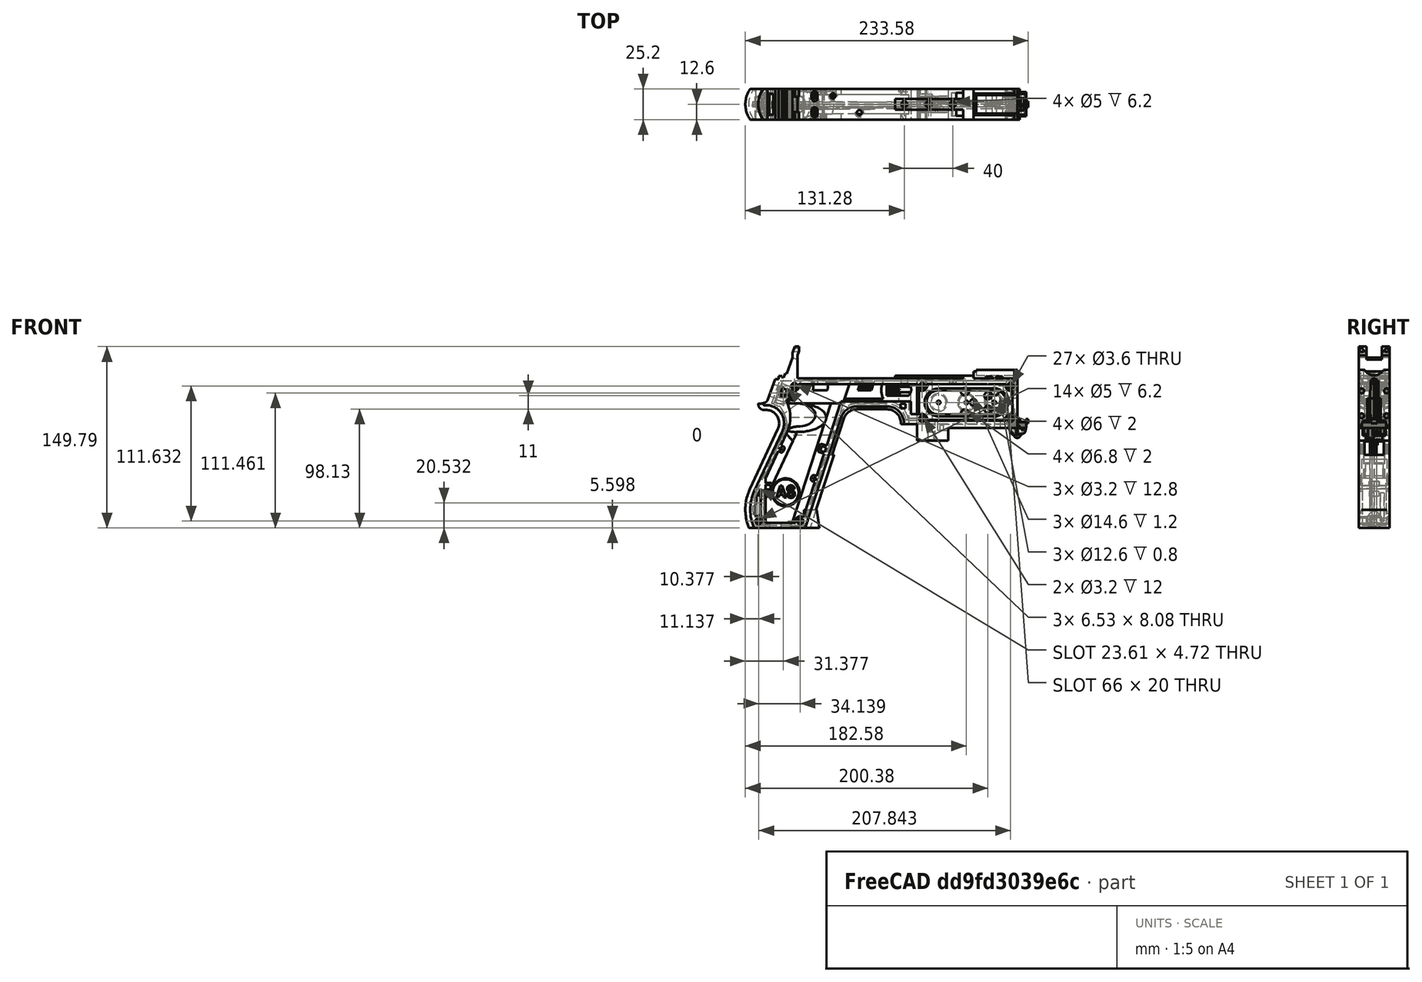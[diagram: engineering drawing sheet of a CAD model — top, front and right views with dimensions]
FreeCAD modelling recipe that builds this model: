
FCSTD DOCUMENT  (FreeCAD 1.0R39319 (Git))
Label: PICON-OF_ver_34
License: All rights reserved
LicenseURL: https://en.wikipedia.org/wiki/All_rights_reserved
objects: Sketcher::SketchObject×119, Part::Extrusion×75, Part::Cut×47, PartDesign::Pad×19, PartDesign::Pocket×14, PartDesign::Chamfer×14, PartDesign::Body×8, Part::MultiFuse×6, PartDesign::Fillet×6, PartDesign::SubtractivePipe×4, Part::Part2DObjectPython×4, PartDesign::SubtractiveLoft×4, PartDesign::Plane×2, PartDesign::SubShapeBinder×2, Part::Sweep×1, PartDesign::ShapeBinder×1, PartDesign::FeatureBase×1, Part::Cone×1, Part::Chamfer×1, Mesh::Feature×1, +1 more types
note: 572 computed .brp shape members not serialized (recipe doc carries the construction recipe); baked Part::Feature solids carry a one-line shape summary decoded from their .brp

FEATURE [Sketcher::SketchObject] Sketch  label="corpo principale"
  ArcFitTolerance = 1e-06
  AttacherType = Attacher::AttachEngine3D
  AttachmentSupport = -> [XZ_Plane]
  FullyConstrained = true
  MakeInternals = false
  MapMode = 5
  Placement = pos=(0,0,0) rot=(1,0,0;1.5708rad)
  sketch-geometry (65):
    g0: LineSegment StartX=0 StartY=0 StartZ=0 EndX=-57.2 EndY=0 EndZ=0
    g1: LineSegment StartX=-57.2 StartY=0 StartZ=0 EndX=-57.2 EndY=-10.4 EndZ=0
    g2: LineSegment StartX=-57.2 StartY=-10.4 StartZ=0 EndX=-82.8 EndY=-10.4 EndZ=0
    g3: LineSegment StartX=-82.8 StartY=-10.4 StartZ=0 EndX=-82.8 EndY=3.2 EndZ=0
    g4: LineSegment StartX=-82.8 StartY=3.2 StartZ=0 EndX=-93.6 EndY=3.2 EndZ=0
    g5: LineSegment StartX=-93.6 StartY=3.2 StartZ=0 EndX=-93.6 EndY=4 EndZ=0
    g6: LineSegment StartX=-107.6 StartY=18 StartZ=0 EndX=-132.428 EndY=18 EndZ=0
    g7: LineSegment StartX=-145.743 StartY=8.32624 StartZ=0 EndX=-175.232 EndY=-82.4316 EndZ=0
    g8: LineSegment StartX=-175.232 StartY=-82.4316 StartZ=0 EndX=-217.232 EndY=-82.4316 EndZ=0
    g9: LineSegment StartX=-217.232 StartY=-52.1862 StartZ=0 EndX=-193.988 EndY=-2.33927 EndZ=0
    g10: LineSegment StartX=-206.196 StartY=23.0857 StartZ=0 EndX=-199.861 EndY=40.4914 EndZ=0
    g11: LineSegment StartX=-199.861 StartY=40.4914 StartZ=0 EndX=-197.061 EndY=40.4914 EndZ=0
    g12: LineSegment StartX=-197.061 StartY=40.4914 StartZ=0 EndX=-197.061 EndY=42.8914 EndZ=0
    g13: LineSegment StartX=-197.061 StartY=42.8914 StartZ=0 EndX=-194.261 EndY=42.8914 EndZ=0
    g14: LineSegment StartX=-194.261 StartY=42.8914 StartZ=0 EndX=-194.535 EndY=42.1397 EndZ=0
    g15: LineSegment StartX=-194.535 StartY=42.1397 StartZ=0 EndX=-193.031 EndY=41.5924 EndZ=0
    g16: LineSegment StartX=-193.031 StartY=41.5924 StartZ=0 EndX=-191.663 EndY=45.3512 EndZ=0
    g17: LineSegment StartX=-191.663 StartY=45.3512 StartZ=0 EndX=-190.536 EndY=44.9408 EndZ=0
    g18: LineSegment StartX=-190.536 StartY=44.9408 StartZ=0 EndX=-185.747 EndY=58.0965 EndZ=0
    g19: LineSegment StartX=-185.747 StartY=58.0965 StartZ=0 EndX=-185.747 EndY=62.0965 EndZ=0
    g20: LineSegment StartX=-185.747 StartY=62.0965 StartZ=0 EndX=-183.832 EndY=67.3588 EndZ=0
    g21: LineSegment StartX=-183.832 StartY=67.3588 StartZ=0 EndX=-180.232 EndY=67.3588 EndZ=0
    g22: LineSegment StartX=-180.232 StartY=67.3588 StartZ=0 EndX=-180.232 EndY=63.7588 EndZ=0
    g23: LineSegment StartX=-180.232 StartY=63.7588 StartZ=0 EndX=-181.6 EndY=60 EndZ=0
    g24: LineSegment StartX=-181.6 StartY=60 StartZ=0 EndX=-181.6 EndY=41.2 EndZ=0
    g25: LineSegment StartX=-181.6 StartY=41.2 StartZ=0 EndX=-100.8 EndY=41.2 EndZ=0
    g26: LineSegment StartX=-36 StartY=43.2 StartZ=0 EndX=-36 EndY=41.2 EndZ=0
    g27: LineSegment StartX=0 StartY=48 StartZ=0 EndX=0 EndY=0 EndZ=0
    g28: LineSegment StartX=-209.901 StartY=19.85 StartZ=0 EndX=-209.901 EndY=20.1 EndZ=0
    g29: LineSegment StartX=-208.001 StartY=22 StartZ=0 EndX=-207.747 EndY=22 EndZ=0
    g30: LineSegment StartX=-207.583 StartY=19 StartZ=0 EndX=-209.051 EndY=19 EndZ=0
    g31: ArcOfCircle CenterX=-208.001 CenterY=20.1 CenterZ=0 NormalX=0 NormalY=0 NormalZ=1 AngleXU=0 Radius=1.9 StartAngle=1.5708 EndAngle=3.14159
    g32: GeomPoint [constr] X=-209.901 Y=22 Z=0
    g33: ArcOfCircle CenterX=-209.051 CenterY=19.85 CenterZ=0 NormalX=0 NormalY=0 NormalZ=1 AngleXU=0 Radius=0.85 StartAngle=3.14159 EndAngle=4.71239
    g34: GeomPoint [constr] X=-209.901 Y=19 Z=0
    g35: ArcOfCircle CenterX=-207.747 CenterY=23.65 CenterZ=0 NormalX=0 NormalY=0 NormalZ=1 AngleXU=0 Radius=1.65 StartAngle=4.71239 EndAngle=5.93412
    g36: GeomPoint [constr] X=-206.591 Y=22 Z=0
    g37: LineSegment StartX=-4 StartY=6 StartZ=0 EndX=-4 EndY=36.4 EndZ=0
    g38: LineSegment StartX=-4 StartY=36.4 StartZ=0 EndX=-185.2 EndY=36.4 EndZ=0
    g39: LineSegment StartX=-185.2 StartY=36.4 StartZ=0 EndX=-190.441 EndY=22 EndZ=0
    g40: LineSegment StartX=-214.575 StartY=-78.4316 StartZ=0 EndX=-178.142 EndY=-78.4316 EndZ=0
    g41: LineSegment StartX=-178.142 StartY=-78.4316 StartZ=0 EndX=-145.51 EndY=22 EndZ=0
    g42: LineSegment StartX=-145.51 StartY=22 StartZ=0 EndX=-87.91 EndY=22 EndZ=0
    g43: LineSegment StartX=-87.91 StartY=22 StartZ=0 EndX=-87.91 EndY=11.6 EndZ=0
    g44: LineSegment StartX=-87.91 StartY=11.6 StartZ=0 EndX=-80.11 EndY=11.6 EndZ=0
    g45: LineSegment StartX=-80.11 StartY=11.6 StartZ=0 EndX=-80.11 EndY=6 EndZ=0
    g46: LineSegment StartX=-80.11 StartY=6 StartZ=0 EndX=-4 EndY=6 EndZ=0
    g47: LineSegment StartX=-190.363 StartY=-4.02975 StartZ=0 EndX=-213.607 EndY=-53.8767 EndZ=0
    g48: ArcOfCircle CenterX=-132.428 CenterY=4 CenterZ=0 NormalX=0 NormalY=0 NormalZ=1 AngleXU=0 Radius=14 StartAngle=1.5708 EndAngle=2.82743
    g49: GeomPoint [constr] X=-142.6 Y=18 Z=0
    g50: ArcOfCircle CenterX=-107.6 CenterY=4 CenterZ=0 NormalX=0 NormalY=0 NormalZ=1 AngleXU=0 Radius=14 StartAngle=0 EndAngle=1.5708
    g51: GeomPoint [constr] X=-93.6 Y=18 Z=0
    g52: ArcOfCircle CenterX=-184.801 CenterY=-67.3089 CenterZ=0 NormalX=0 NormalY=0 NormalZ=1 AngleXU=0 Radius=35.7833 StartAngle=2.70526 EndAngle=3.57792
    g53: ArcOfCircle CenterX=-207.583 CenterY=4 CenterZ=0 NormalX=0 NormalY=0 NormalZ=1 AngleXU=0 Radius=15 StartAngle=5.84685 EndAngle=7.85398
    g54: LineSegment [constr] StartX=-213.607 StartY=-53.8767 StartZ=0 EndX=-217.232 EndY=-52.1862 EndZ=0
    g55: ArcOfCircle CenterX=-184.801 CenterY=-67.3089 CenterZ=0 NormalX=0 NormalY=0 NormalZ=1 AngleXU=0 Radius=31.7833 StartAngle=2.70526 EndAngle=3.49911
    g56: ArcOfCircle CenterX=-218.095 CenterY=8.90192 CenterZ=0 NormalX=0 NormalY=0 NormalZ=1 AngleXU=0 Radius=30.5989 StartAngle=5.84685 EndAngle=6.72553
    g57: LineSegment StartX=-44.6 StartY=43.2 StartZ=0 EndX=-36 EndY=43.2 EndZ=0
    g58: LineSegment StartX=-100.8 StartY=41.2 StartZ=0 EndX=-44.6 EndY=41.2 EndZ=0
    g59: LineSegment StartX=-44.6 StartY=41.2 StartZ=0 EndX=-44.6 EndY=43.2 EndZ=0
    g60: LineSegment StartX=-2.4 StartY=48 StartZ=0 EndX=0 EndY=48 EndZ=0
    g61: LineSegment StartX=-36 StartY=41.2 StartZ=0 EndX=-2.4 EndY=41.2 EndZ=0
    g62: LineSegment StartX=-2.4 StartY=41.2 StartZ=0 EndX=-2.4 EndY=48 EndZ=0
    g63: LineSegment [constr] StartX=-181.6 StartY=36.4 StartZ=0 EndX=-152.209 EndY=36.4 EndZ=0
    g64: LineSegment [constr] StartX=-181.6 StartY=36.4 StartZ=0 EndX=-130.41 EndY=36.4 EndZ=0
  constraints (183):
    c: Coincident(g-1,g0)
    c: PointOnObject(g0,g-1)
    c: Coincident(g0,g1)
    c: Vertical(g1)
    c: Coincident(g1,g2)
    c: Horizontal(g2)
    c: Coincident(g2,g3)
    c: Vertical(g3)
    c: Coincident(g3,g4)
    c: Coincident(g4,g5)
    c: Vertical(g5)
    c: Horizontal(g6)
    c: Coincident(g7,g8)
    c: Horizontal(g8)
    c: Coincident(g10,g11)
    c: Horizontal(g11)
    c: Coincident(g11,g12)
    c: Vertical(g12)
    c: Coincident(g12,g13)
    c: Horizontal(g13)
    c: Coincident(g13,g14)
    c: Coincident(g14,g15)
    c: Coincident(g15,g16)
    c: Coincident(g16,g17)
    c: Coincident(g17,g18)
    c: Coincident(g18,g19)
    c: Vertical(g19)
    c: Coincident(g19,g20)
    c: Coincident(g20,g21)
    c: Horizontal(g21)
    c: Coincident(g21,g22)
    c: Vertical(g22)
    c: Coincident(g22,g23)
    c: Coincident(g23,g24)
    c: Vertical(g24)
    c: Coincident(g24,g25)
    c: Horizontal(g25)
    c: Coincident(g57,g26)
    c: Vertical(g26)
    c: Coincident(g26,g61)
    c: PointOnObject(g60,g-2)
    c: Coincident(g60,g27)
    c: Coincident(g27,g0)
    c: DistanceY(g27,g27) = 48
    c: DistanceY(g1,g1) = 10.4
    c: DistanceX(g0,g0) = 57.2
    c: DistanceX(g2,g2) = 25.6
    c: Horizontal(g4)
    c: DistanceY(g3,g3) = 13.6
    c: DistanceX(g4,g4) = 10.8
    c: DistanceY(g5,g51) = 14.8
    c: DistanceX(g49,g51) = 49
    c: Distance(g7,g49) = 105.6
    c: DistanceX(g61,g60) = 36
    c: DistanceX(g25,g25) = 80.8
    c: DistanceY(g24,g24) = 18.8
    c: DistanceY(g22,g22) = 3.6
    c: Distance(g23) = 4
    c: Angle(g-1,g23) = 1.22173
    c: DistanceX(g21,g21) = 3.6
    c: Distance(g20) = 5.6
    c: Angle(g-1,g20) = 1.22173
    c: DistanceY(g19,g19) = 4
    c: Distance(g18) = 14
    c: Angle(g-1,g18) = 1.22173
    c: Distance(g17) = 1.2
    c: Distance(g16) = 4
    c: Angle(g16) = 1.22173
    c: Perpendicular(g18,g17)
    c: Distance(g15) = 1.6
    c: Perpendicular(g16,g15)
    c: Distance(g14) = 0.8
    c: DistanceX(g13,g13) = 2.8
    c: Perpendicular(g15,g14)
    c: DistanceY(g12,g12) = 2.4
    c: DistanceX(g11,g11) = 2.8
    c: Distance(g9) = 55
    c: Angle(g9,g-1) = 2.00713
    c: Horizontal(g29)
    c: Vertical(g28)
    c: Horizontal(g30)
    c: PointOnObject(g32,g29)
    c: PointOnObject(g32,g28)
    c: Tangent(g29,g31) = 1.5708
    c: Tangent(g28,g31) = 1.5708
    c: PointOnObject(g34,g28)
    c: PointOnObject(g34,g30)
    c: Tangent(g28,g33) = 1.5708
    c: Tangent(g30,g33) = 1.5708
    c: PointOnObject(g36,g29)
    c: PointOnObject(g36,g10)
    c: Tangent(g29,g35) = -1.5708
    c: Tangent(g10,g35) = -1.5708
    c: Angle(g-1,g10) = 1.22173
    c: Radius(g35) = 1.65
    c: Vertical(g37)
    c: Coincident(g37,g38)
    c: Horizontal(g38)
    c: Coincident(g38,g39)
    c: Horizontal(g40)
    c: Coincident(g40,g41)
    c: Coincident(g41,g42)
    c: Horizontal(g42)
    c: Coincident(g42,g43)
    c: Vertical(g43)
    c: Coincident(g43,g44)
    c: Horizontal(g44)
    c: Coincident(g44,g45)
    c: Vertical(g45)
    c: Coincident(g45,g46)
    c: Coincident(g46,g37)
    c: Horizontal(g46)
    c: DistanceY(g0,g37) = 6
    c: DistanceX(g37,g0) = 4
    c: DistanceY(g37,g25) = 4.8
    c: DistanceX(g38,g38) = 181.2
    c: DistanceX(g42,g42) = 57.6
    c: DistanceY(g49,g41) = 4
    c: DistanceX(g41,g49) = 2.91
    c: DistanceY(g43,g43) = 10.4
    c: DistanceX(g44,g44) = 7.8
    c: DistanceY(g7,g40) = 4
    c: Distance(g47) = 55
    c: Angle(g-1,g39) = 1.22173
    c: PointOnObject(g49,g7)
    c: PointOnObject(g49,g6)
    c: Tangent(g7,g48) = -1.5708
    c: Tangent(g6,g48) = -1.5708
    c: PointOnObject(g51,g5)
    c: PointOnObject(g51,g6)
    c: Tangent(g5,g50) = -1.5708
    c: Tangent(g6,g50) = -1.5708
    c: Radius(g50) = 14
    c: Radius(g48) = 14
    c: DistanceX(g8,g8) = 42
    c: Angle(g7,g-1) = 1.88496
    c: Parallel(g41,g7)
    c: Parallel(g47,g9)
    c: Coincident(g52,g8)
    c: Tangent(g52,g9) = 1.5708
    c: DistanceX(g9,g8) = 0
    c: Tangent(g53,g9) = -1.5708
    c: Tangent(g53,g30) = -1.5708
    c: Diameter(g53) = 30
    c: DistanceY(g53,g0) = -4
    c: Coincident(g54,g47)
    c: Distance(g54) = 4
    c: Coincident(g54,g9)
    c: Coincident(g55,g40)
    c: Tangent(g55,g47) = -1.5708
    c: Coincident(g52,g55)
    c: Coincident(g56,g39)
    c: Tangent(g56,g47) = 1.5708
    c: Horizontal(g57)
    c: DistanceX(g57,g57) = 8.6
    c: Coincident(g58,g25)
    c: Horizontal(g58)
    c: Coincident(g59,g58)
    c: Vertical(g59)
    c: DistanceY(g58,g57) = 2
    c: DistanceX(g58,g58) = 56.2
    c: Coincident(g59,g57)
    c: DistanceY(g41,g36) = 0
    c: DistanceY(g36,g39) = 0
    c: DistanceY(g28,g28) = 0.25
    c: DistanceX(g30,g36) = 2.46
    c: DistanceX(g28,g29) = 1.9
    c: Coincident(g62,g60)
    c: Horizontal(g60)
    c: DistanceX(g62,g27) = 2.4
    c: Coincident(g61,g62)
    c: DistanceY(g26,g26) = 2
    c: Vertical(g62)
    c: DistanceY(g61,g60) = 6.8
    c: Horizontal(g61)
    c: Distance(g63) = 29.391
    c: PointOnObject(g63,g38)
    c: PointOnObject(g63,g38)
    c: Distance(g64) = 51.19
    c: PointOnObject(g64,g38)
    c: PointOnObject(g64,g38)
    c: DistanceX(g24,g63) = 0
    c: DistanceX(g24,g64) = 0
FEATURE [Part::Extrusion] Extrude  label="Extrude corpo principale"
  Base = -> Sketch
  Dir = (0,-1,2e-16)
  DirMode = 2
  FaceMakerClass = Part::FaceMakerBullseye
  FaceMakerMode = 3
  LengthFwd = 25.2
  LengthRev = 12.6
  Solid = true
  Symmetric = true
FEATURE [Sketcher::SketchObject] Sketch002  label="scavo grilletto"
  ArcFitTolerance = 1e-06
  AttachmentSupport = -> [XZ_Plane]
  ExternalGeometry = -> [Sketch]
  FullyConstrained = true
  MakeInternals = false
  MapMode = 5
  Placement = pos=(0,0,0) rot=(1,0,0;1.5708rad)
  sketch-geometry (4):
    g0: LineSegment StartX=-89.51 StartY=22 StartZ=0 EndX=-152.71 EndY=22 EndZ=0
    g1: LineSegment StartX=-152.71 StartY=22 StartZ=0 EndX=-167.006 EndY=-22 EndZ=0
    g2: LineSegment StartX=-167.006 StartY=-22 StartZ=0 EndX=-89.51 EndY=-22 EndZ=0
    g3: LineSegment StartX=-89.51 StartY=-22 StartZ=0 EndX=-89.51 EndY=22 EndZ=0
  constraints (12):
    c: Horizontal(g0)
    c: Coincident(g0,g1)
    c: Coincident(g1,g2)
    c: Horizontal(g2)
    c: Coincident(g2,g3)
    c: Coincident(g3,g0)
    c: Vertical(g3)
    c: Angle(g1,g0) = 1.88496
    c: DistanceY(g3,g3) = 44
    c: DistanceX(g0,g0) = 63.2
    c: DistanceX(g0,g-3) = 1.6
    c: DistanceY(g-3,g0) = 0
FEATURE [Sketcher::SketchObject] Sketch004  label="traiettoria arrotondamento impugnatura anteriore"
  ArcFitTolerance = 1e-06
  AttachmentSupport = -> [XZ_Plane]
  ExternalGeometry = -> [Sketch]
  FullyConstrained = true
  MakeInternals = false
  MapMode = 5
  Placement = pos=(0,0,0) rot=(1,0,0;1.5708rad)
  sketch-geometry (13):
    g0: LineSegment StartX=-175.232 StartY=-82.4316 StartZ=0 EndX=-145.743 EndY=8.32624 EndZ=0
    g1: LineSegment StartX=-93.6 StartY=3.2 StartZ=0 EndX=-93.6 EndY=4 EndZ=0
    g2: LineSegment StartX=-132.428 StartY=18 StartZ=0 EndX=-107.6 EndY=18 EndZ=0
    g3: ArcOfCircle CenterX=-132.428 CenterY=4 CenterZ=0 NormalX=0 NormalY=0 NormalZ=1 AngleXU=0 Radius=14 StartAngle=1.5708 EndAngle=2.82743
    g4: ArcOfCircle CenterX=-107.6 CenterY=4 CenterZ=0 NormalX=0 NormalY=0 NormalZ=1 AngleXU=0 Radius=14 StartAngle=0 EndAngle=1.5708
    g5: LineSegment StartX=-175.232 StartY=-82.4316 StartZ=0 EndX=-217.232 EndY=-82.4316 EndZ=0
    g6: LineSegment StartX=-217.232 StartY=-52.1862 StartZ=0 EndX=-193.988 EndY=-2.33927 EndZ=0
    g7: LineSegment StartX=-209.051 StartY=19 StartZ=0 EndX=-207.583 EndY=19 EndZ=0
    g8: LineSegment StartX=-209.901 StartY=20.1 StartZ=0 EndX=-209.901 EndY=19.85 EndZ=0
    g9: ArcOfCircle CenterX=-184.801 CenterY=-67.3089 CenterZ=0 NormalX=0 NormalY=0 NormalZ=1 AngleXU=0 Radius=35.7833 StartAngle=2.70526 EndAngle=3.57792
    g10: ArcOfCircle CenterX=-207.583 CenterY=4 CenterZ=0 NormalX=0 NormalY=0 NormalZ=1 AngleXU=0 Radius=15 StartAngle=5.84685 EndAngle=7.85398
    g11: ArcOfCircle CenterX=-209.051 CenterY=19.85 CenterZ=0 NormalX=0 NormalY=0 NormalZ=1 AngleXU=0 Radius=0.85 StartAngle=3.14159 EndAngle=4.71239
    g12: ArcOfCircle CenterX=-208.001 CenterY=20.1 CenterZ=0 NormalX=0 NormalY=0 NormalZ=1 AngleXU=0 Radius=1.9 StartAngle=1.5708 EndAngle=3.14159
  constraints (26):
    c: Coincident(g0,g-3)
    c: Coincident(g0,g-6)
    c: Coincident(g1,g-8)
    c: Coincident(g1,g-7)
    c: Coincident(g2,g-5)
    c: Coincident(g2,g-4)
    c: Coincident(g3,g2)
    c: Tangent(g3,g0) = 1.5708
    c: Coincident(g4,g1)
    c: Tangent(g4,g2) = 1.5708
    c: Coincident(g5,g0)
    c: Coincident(g5,g-9)
    c: Coincident(g6,g-12)
    c: Coincident(g6,g-11)
    c: Coincident(g7,g-15)
    c: Coincident(g7,g-14)
    c: Coincident(g8,g-16)
    c: Coincident(g8,g-17)
    c: Tangent(g9,g6) = 1.5708
    c: Coincident(g9,g5)
    c: Coincident(g10,g7)
    c: Tangent(g10,g6) = -1.5708
    c: Tangent(g11,g7) = -1.5708
    c: Coincident(g11,g8)
    c: Tangent(g12,g8) = -1.5708
    c: Coincident(g12,g-17)
FEATURE [PartDesign::Plane] DatumPlane  label="Piano per disegno arrotondamento impugnatura"
  AttachmentSupport = -> [Sketch]
  Length = 68.5841
  MapMode = 7
  Placement = pos=(-145.743,1.8e-15,8.32624) rot=(0.154555,0.154555,0.97582;1.59527rad)
  ResizeMode = 0
  Width = 191.269
FEATURE [Sketcher::SketchObject] Sketch005  label="forma arrotondamento impugnatura anteriore"
  ArcFitTolerance = 1e-06
  AttachmentSupport = -> [DatumPlane]
  FullyConstrained = true
  MakeInternals = false
  MapMode = 5
  Placement = pos=(-145.743,1.8e-15,8.32624) rot=(0.154555,0.154555,0.97582;1.59527rad)
  sketch-geometry (5):
    g0: GeomPoint [constr] X=0 Y=-4 Z=0
    g1: GeomPoint [constr] X=-12.6 Y=7.1e-15 Z=0
    g2: GeomPoint [constr] X=12.6 Y=4.97e-14 Z=0
    g3: LineSegment StartX=-12.6 StartY=7.1e-15 StartZ=0 EndX=12.6 EndY=4.97e-14 EndZ=0
    g4: ArcOfCircle CenterX=-3.88e-14 CenterY=17.845 CenterZ=0 NormalX=0 NormalY=0 NormalZ=1 AngleXU=0 Radius=21.845 StartAngle=4.09759 EndAngle=5.32718
  constraints (11):
    c: DistanceY(g0,g-1) = 4
    c: DistanceX(g-1,g0) = 0
    c: DistanceX(g1,g-1) = 12.6
    c: DistanceX(g-1,g2) = 12.6
    c: DistanceY(g-1,g2) = 0
    c: DistanceY(g-1,g1) = 0
    c: Coincident(g3,g1)
    c: Coincident(g3,g2)
    c: Coincident(g4,g1)
    c: Coincident(g4,g2)
    c: PointOnObject(g0,g4)
FEATURE [Part::Sweep] Sweep  label="Sweep impugnatura"
  Frenet = true
  Sections = -> [Sketch005]
  Solid = true
  Spine = -> Sketch [Edge32,Edge33,Edge34,Edge35,Edge36,Edge37,Edge38,Edge39,Edge40,Edge41,Edge42,Edge43,Edge44]
  Transition = 1
FEATURE [Sketcher::SketchObject] Sketch008  label="buchi e pulizie varie"
  ArcFitTolerance = 1e-06
  AttachmentSupport = -> [XZ_Plane]
  ExternalGeometry = -> [Sketch]
  FullyConstrained = true
  MakeInternals = false
  MapMode = 5
  Placement = pos=(0,0,0) rot=(1,0,0;1.5708rad)
  sketch-geometry (26):
    g0: LineSegment StartX=-96.278 StartY=20.155 StartZ=0 EndX=-92.278 EndY=20.155 EndZ=0
    g1: LineSegment StartX=-92.278 StartY=20.155 StartZ=0 EndX=-92.278 EndY=16.155 EndZ=0
    g2: LineSegment StartX=-92.278 StartY=16.155 StartZ=0 EndX=-96.278 EndY=16.155 EndZ=0
    g3: LineSegment StartX=-96.278 StartY=16.155 StartZ=0 EndX=-96.278 EndY=20.155 EndZ=0
    g4: LineSegment StartX=-222.232 StartY=-82.4316 StartZ=0 EndX=-170.232 EndY=-82.4316 EndZ=0
    g5: LineSegment StartX=-170.232 StartY=-82.4316 StartZ=0 EndX=-170.232 EndY=-86.4316 EndZ=0
    g6: LineSegment StartX=-170.232 StartY=-86.4316 StartZ=0 EndX=-222.232 EndY=-86.4316 EndZ=0
    g7: LineSegment StartX=-222.232 StartY=-86.4316 StartZ=0 EndX=-222.232 EndY=-82.4316 EndZ=0
    g8: LineSegment StartX=-213.901 StartY=20.1 StartZ=0 EndX=-213.901 EndY=26 EndZ=0
    g9: LineSegment StartX=-213.901 StartY=26 StartZ=0 EndX=-206.196 EndY=26 EndZ=0
    g10: LineSegment StartX=-17.4 StartY=42.8 StartZ=0 EndX=-12.4 EndY=42.8 EndZ=0
    g11: LineSegment StartX=-12.4 StartY=42.8 StartZ=0 EndX=-12.4 EndY=41.2 EndZ=0
    g12: LineSegment StartX=-12.4 StartY=41.2 StartZ=0 EndX=-17.4 EndY=41.2 EndZ=0
    g13: LineSegment StartX=-17.4 StartY=41.2 StartZ=0 EndX=-17.4 EndY=42.8 EndZ=0
    g14: LineSegment StartX=-25.9 StartY=42.8 StartZ=0 EndX=-20.9 EndY=42.8 EndZ=0
    g15: LineSegment StartX=-20.9 StartY=42.8 StartZ=0 EndX=-20.9 EndY=41.2 EndZ=0
    g16: LineSegment StartX=-20.9 StartY=41.2 StartZ=0 EndX=-25.9 EndY=41.2 EndZ=0
    g17: LineSegment StartX=-25.9 StartY=41.2 StartZ=0 EndX=-25.9 EndY=42.8 EndZ=0
    g18: GeomPoint [constr] X=-206.196 Y=23.0857 Z=0
    g19: GeomPoint [constr] X=-213.901 Y=20.1 Z=0
    g20: BSplineCurve PolesCount=4 KnotsCount=2 Degree=3 IsPeriodic=0
    g21-g24: Circle [constr] x4 (B-spline internal-alignment scaffolding for g20; pole/knot coordinates omitted)
    g25: LineSegment StartX=-206.196 StartY=26 StartZ=0 EndX=-206.196 EndY=23.0857 EndZ=0
  constraints (73):
    c: Horizontal(g0)
    c: Coincident(g1,g0)
    c: Vertical(g1)
    c: Coincident(g2,g1)
    c: Horizontal(g2)
    c: Coincident(g3,g2)
    c: Coincident(g3,g0)
    c: Vertical(g3)
    c: DistanceX(g0,g-4) = 4.368
    c: DistanceY(g0,g-4) = 1.845
    c: DistanceY(g1,g1) = 4
    c: DistanceX(g2,g2) = 4
    c: Horizontal(g4)
    c: Coincident(g5,g4)
    c: Vertical(g5)
    c: Coincident(g6,g5)
    c: Horizontal(g6)
    c: Coincident(g7,g6)
    c: Coincident(g7,g4)
    c: Vertical(g7)
    c: DistanceY(g7,g7) = 4
    c: DistanceX(g4,g-5) = 5
    c: DistanceX(g-5,g4) = 5
    c: DistanceY(g4,g-5) = 0
    c: Coincident(g9,g8)
    c: Parallel(g9,g-6)
    c: DistanceX(g8,g-8) = 4
    c: Horizontal(g10)
    c: Coincident(g11,g10)
    c: Vertical(g11)
    c: Coincident(g12,g11)
    c: Horizontal(g12)
    c: Coincident(g13,g12)
    c: Coincident(g13,g10)
    c: Vertical(g13)
    c: Horizontal(g14)
    c: Coincident(g15,g14)
    c: Vertical(g15)
    c: Coincident(g16,g15)
    c: Horizontal(g16)
    c: Coincident(g17,g16)
    c: Coincident(g17,g14)
    c: Vertical(g17)
    c: DistanceY(g11,g10) = 1.6
    c: DistanceX(g10,g10) = 5
    c: DistanceY(g15,g14) = 1.6
    c: DistanceX(g14,g14) = 5
    c: DistanceX(g15,g12) = 3.5
    c: DistanceX(g11,g-9) = 10
    c: DistanceY(g-9,g11) = 0
    c: DistanceY(g-9,g15) = 0
    c: Perpendicular(g8,g9)
    c: DistanceY(g-7,g9) = 4
    c: DistanceY(g8,g-8) = 0
    c: InternalAlignment(g18,g20)
    c: InternalAlignment(g19,g20)
    c: InternalAlignment(g21,g20)
    c: Weight(g21) = 1
    c: InternalAlignment(g22,g20)
    c: Equal(g22,g21)
    c: InternalAlignment(g23,g20)
    c: Equal(g23,g21)
    c: InternalAlignment(g24,g20)
    c: Equal(g24,g21)
    c: Coincident(g18,g-12)
    c: Coincident(g19,g8)
    c: Coincident(g25,g9)
    c: Coincident(g25,g20)
    c: Vertical(g25)
    c: DistanceY(g20,g23) = 0
    c: DistanceY(g22,g18) = 2.26
    c: DistanceX(g22,g18) = 0.93
    c: DistanceX(g20,g23) = 2.9
FEATURE [Part::Extrusion] Extrude004  label="Extrude Buchi e pulizie varie"
  Base = -> Sketch008
  Dir = (0,-1,2e-16)
  DirMode = 2
  FaceMakerClass = Part::FaceMakerBullseye
  FaceMakerMode = 3
  LengthFwd = 25.2
  LengthRev = 0
  Solid = true
  Symmetric = true
FEATURE [Sketcher::SketchObject] Sketch009  label="rinforzi"
  ArcFitTolerance = 1e-06
  AttachmentSupport = -> [XZ_Plane]
  ExternalGeometry = -> [Sketch]
  FullyConstrained = true
  MakeInternals = false
  MapMode = 5
  Placement = pos=(0,0,0) rot=(1,0,0;1.5708rad)
  sketch-geometry (9):
    g0: LineSegment StartX=-87.91 StartY=22 StartZ=0 EndX=-87.91 EndY=36.4 EndZ=0
    g1: LineSegment StartX=-87.91 StartY=36.4 StartZ=0 EndX=-97.91 EndY=36.4 EndZ=0
    g2: LineSegment StartX=-97.91 StartY=36.4 StartZ=0 EndX=-97.91 EndY=22 EndZ=0
    g3: LineSegment StartX=-97.91 StartY=22 StartZ=0 EndX=-87.91 EndY=22 EndZ=0
    g4: LineSegment StartX=-149.713 StartY=9.06563 StartZ=0 EndX=-154.586 EndY=-5.93437 EndZ=0
    g5: LineSegment StartX=-154.586 StartY=-5.93437 StartZ=0 EndX=-191.863 EndY=-5.93437 EndZ=0
    g6: LineSegment StartX=-191.863 StartY=-5.93437 StartZ=0 EndX=-191.863 EndY=9.06563 EndZ=0
    g7: LineSegment StartX=-191.863 StartY=9.06563 StartZ=0 EndX=-149.713 EndY=9.06563 EndZ=0
    g8: LineSegment [constr] StartX=-145.51 StartY=22 StartZ=0 EndX=-149.713 EndY=9.06563 EndZ=0
  constraints (25):
    c: Vertical(g0)
    c: Coincident(g1,g0)
    c: Horizontal(g1)
    c: Coincident(g2,g1)
    c: Vertical(g2)
    c: Coincident(g3,g2)
    c: Coincident(g3,g0)
    c: Horizontal(g3)
    c: Coincident(g0,g-4)
    c: DistanceX(g3,g3) = 10
    c: DistanceY(g0,g-3) = 0
    c: Coincident(g5,g4)
    c: Horizontal(g5)
    c: Coincident(g6,g5)
    c: Vertical(g6)
    c: Coincident(g7,g6)
    c: Coincident(g7,g4)
    c: Horizontal(g7)
    c: Distance(g8) = 13.6
    c: Parallel(g-6,g8)
    c: Coincident(g-6,g8)
    c: Parallel(g4,g-6)
    c: DistanceY(g4,g4) = 15
    c: Coincident(g4,g8)
    c: DistanceX(g-5,g5) = -1.5
FEATURE [Part::Extrusion] Extrude001  label="Extrude scavo grilletto"
  Base = -> Sketch002
  Dir = (0,-1,2e-16)
  DirMode = 2
  FaceMakerClass = Part::FaceMakerBullseye
  FaceMakerMode = 3
  LengthFwd = 16
  LengthRev = 0
  Solid = true
  Symmetric = true
FEATURE [Part::Extrusion] Extrude005  label="Extrude Rinforzi"
  Base = -> Sketch009
  Dir = (0,-1,2e-16)
  DirMode = 2
  FaceMakerClass = Part::FaceMakerBullseye
  FaceMakerMode = 3
  LengthFwd = 2
  LengthRev = 0
  Placement = pos=(0,12.6,0) rot=(0,0,1;0rad)
  Solid = true
  Symmetric = false
FEATURE [PartDesign::ShapeBinder] CopyCut
  TraceSupport = false
FEATURE [PartDesign::Plane] DatumPlane001
  AttachmentSupport = -> [CopyCut]
  Length = 60
  MapMode = 5
  Placement = pos=(0,12.6,0) rot=(0,0.707107,0.707107;3.14159rad)
  ResizeMode = 0
  Width = 60
FEATURE [Sketcher::SketchObject] Sketch010  label="buco neopixel"
  ArcFitTolerance = 1e-06
  AttachmentSupport = -> [XZ_Plane]
  ExternalGeometry = -> [Sketch]
  FullyConstrained = true
  MakeInternals = false
  MapMode = 5
  Placement = pos=(0,0,0) rot=(1,0,0;1.5708rad)
  sketch-geometry (5):
    g0: LineSegment [constr] StartX=-199.861 StartY=40.4914 StartZ=0 EndX=-201.368 EndY=36.3521 EndZ=0
    g1: LineSegment StartX=-201.368 StartY=36.3521 StartZ=0 EndX=-204.932 EndY=26.5605 EndZ=0
    g2: LineSegment StartX=-201.368 StartY=36.3521 StartZ=0 EndX=-180.2 EndY=28.6477 EndZ=0
    g3: LineSegment StartX=-180.2 StartY=28.6477 StartZ=0 EndX=-183.764 EndY=18.8561 EndZ=0
    g4: LineSegment StartX=-183.764 StartY=18.8561 StartZ=0 EndX=-204.932 EndY=26.5605 EndZ=0
  constraints (14):
    c: Parallel(g0,g-3)
    c: Distance(g0) = 4.405
    c: Coincident(g0,g-3)
    c: Coincident(g2,g1)
    c: Coincident(g3,g2)
    c: Coincident(g4,g3)
    c: Coincident(g4,g1)
    c: Parallel(g1,g-3)
    c: Distance(g1) = 10.42
    c: Coincident(g1,g0)
    c: Parallel(g2,g4)
    c: Perpendicular(g1,g2)
    c: DistanceX(g-4,g2) = 5
    c: Parallel(g3,g1)
FEATURE [Part::Extrusion] Extrude006  label="Extrude buco neopixel"
  Base = -> Sketch010
  Dir = (0,-1,2e-16)
  DirMode = 2
  FaceMakerClass = Part::FaceMakerBullseye
  FaceMakerMode = 3
  LengthFwd = 17.2
  LengthRev = 0
  Solid = true
  Symmetric = true
FEATURE [Sketcher::SketchObject] Sketch011  label="fermo grilletto"
  ArcFitTolerance = 1e-06
  AttachmentSupport = -> [XZ_Plane]
  ExternalGeometry = -> [Sketch]
  FullyConstrained = true
  MakeInternals = false
  MapMode = 5
  Placement = pos=(0,0,0) rot=(1,0,0;1.5708rad)
  sketch-geometry (18):
    g0: LineSegment [constr] StartX=-145.51 StartY=22 StartZ=0 EndX=-157.347 EndY=-14.4293 EndZ=0
    g1: LineSegment [constr] StartX=-157.347 StartY=-14.4293 StartZ=0 EndX=-157.841 EndY=-15.951 EndZ=0
    g2: LineSegment StartX=-161.151 StartY=-13.1932 StartZ=0 EndX=-155.825 EndY=-14.9237 EndZ=0
    g3: LineSegment StartX=-163.167 StartY=-14.2205 StartZ=0 EndX=-164.403 EndY=-18.0247 EndZ=0
    g4: LineSegment StartX=-163.376 StartY=-20.0408 StartZ=0 EndX=-158.05 EndY=-21.7713 EndZ=0
    g5: LineSegment StartX=-158.05 StartY=-21.7713 StartZ=0 EndX=-155.825 EndY=-14.9237 EndZ=0
    g6: LineSegment StartX=-161.645 StartY=-14.7149 StartZ=0 EndX=-157.841 EndY=-15.951 EndZ=0
    g7: LineSegment StartX=-157.841 StartY=-15.951 StartZ=0 EndX=-159.077 EndY=-19.7552 EndZ=0
    g8: LineSegment StartX=-159.077 StartY=-19.7552 StartZ=0 EndX=-162.881 EndY=-18.5191 EndZ=0
    g9: LineSegment StartX=-162.881 StartY=-18.5191 StartZ=0 EndX=-161.645 EndY=-14.7149 EndZ=0
    g10: LineSegment [constr] StartX=-161.645 StartY=-14.7149 StartZ=0 EndX=-161.151 EndY=-13.1932 EndZ=0
    g11: LineSegment [constr] StartX=-159.077 StartY=-19.7552 StartZ=0 EndX=-157.555 EndY=-20.2496 EndZ=0
    g12: LineSegment [constr] StartX=-159.077 StartY=-19.7552 StartZ=0 EndX=-159.572 EndY=-21.2769 EndZ=0
    g13: LineSegment [constr] StartX=-161.645 StartY=-14.7149 StartZ=0 EndX=-163.167 EndY=-14.2205 EndZ=0
    g14: ArcOfCircle CenterX=-161.645 CenterY=-14.7149 CenterZ=0 NormalX=0 NormalY=0 NormalZ=1 AngleXU=0 Radius=1.6 StartAngle=1.25664 EndAngle=2.82743
    g15: GeomPoint [constr] X=-162.673 Y=-12.6988 Z=0
    g16: ArcOfCircle CenterX=-162.881 CenterY=-18.5191 CenterZ=0 NormalX=0 NormalY=0 NormalZ=1 AngleXU=0 Radius=1.6 StartAngle=2.82743 EndAngle=4.39823
    g17: GeomPoint [constr] X=-164.897 Y=-19.5464 Z=0
  constraints (48):
    c: Parallel(g0,g-3)
    c: Distance(g0) = 38.304
    c: Coincident(g0,g-3)
    c: Parallel(g1,g-3)
    c: Distance(g1) = 1.6
    c: Coincident(g1,g0)
    c: Coincident(g5,g4)
    c: Coincident(g5,g2)
    c: Coincident(g7,g6)
    c: Coincident(g8,g7)
    c: Coincident(g9,g8)
    c: Coincident(g9,g6)
    c: Parallel(g7,g-3)
    c: Parallel(g9,g7)
    c: Perpendicular(g6,g7)
    c: Parallel(g6,g8)
    c: Distance(g6) = 4
    c: Distance(g9) = 4
    c: Parallel(g5,g7)
    c: Parallel(g9,g3)
    c: Parallel(g2,g6)
    c: Parallel(g4,g8)
    c: Parallel(g13,g6)
    c: Parallel(g10,g9)
    c: Parallel(g11,g8)
    c: Parallel(g12,g7)
    c: Distance(g10) = 1.6
    c: Distance(g13) = 1.6
    c: Distance(g12) = 1.6
    c: Distance(g11) = 1.6
    c: Coincident(g10,g6)
    c: Coincident(g13,g6)
    c: Coincident(g12,g7)
    c: Coincident(g11,g7)
    c: Distance(g10,g15) = 1.6
    c: Distance(g15,g13) = 1.6
    c: Distance(g4,g12) = 1.6
    c: Distance(g4,g11) = 1.6
    c: PointOnObject(g15,g2)
    c: Tangent(g3,g14) = -1.5708
    c: Tangent(g2,g14) = 1.5708
    c: PointOnObject(g17,g4)
    c: PointOnObject(g17,g3)
    c: Tangent(g4,g16) = -1.5708
    c: Tangent(g3,g16) = -1.5708
    c: Equal(g16,g14)
    c: Coincident(g16,g8)
    c: Coincident(g6,g1)
FEATURE [Part::Extrusion] Extrude007  label="Extrude fermo grilletto"
  Base = -> Sketch011
  Dir = (0,-1,2e-16)
  DirMode = 2
  FaceMakerClass = Part::FaceMakerBullseye
  FaceMakerMode = 3
  LengthFwd = 25.2
  LengthRev = 0
  Solid = true
  Symmetric = true
FEATURE [Sketcher::SketchObject] Sketch012  label="buco oled"
  ArcFitTolerance = 1e-06
  AttachmentSupport = -> [XZ_Plane]
  ExternalGeometry = -> [Sketch]
  FullyConstrained = true
  MakeInternals = false
  MapMode = 5
  Placement = pos=(0,0,0) rot=(1,0,0;1.5708rad)
  sketch-geometry (4):
    g0: LineSegment StartX=-185.747 StartY=58.0965 StartZ=0 EndX=-180.232 EndY=56.0891 EndZ=0
    g1: LineSegment StartX=-185.747 StartY=58.0965 StartZ=0 EndX=-185.747 EndY=67.3588 EndZ=0
    g2: LineSegment StartX=-185.747 StartY=67.3588 StartZ=0 EndX=-180.232 EndY=67.3588 EndZ=0
    g3: LineSegment StartX=-180.232 StartY=67.3588 StartZ=0 EndX=-180.232 EndY=56.0891 EndZ=0
  constraints (10):
    c: Coincident(g1,g0)
    c: Coincident(g2,g1)
    c: Coincident(g3,g2)
    c: Coincident(g3,g0)
    c: Parallel(g1,g-5)
    c: Perpendicular(g-3,g0)
    c: Parallel(g2,g-6)
    c: Parallel(g3,g-4)
    c: Coincident(g0,g-5)
    c: Coincident(g2,g-6)
FEATURE [Part::Extrusion] Extrude008  label="Extrude buco oled"
  Base = -> Sketch012
  Dir = (0,-1,2e-16)
  DirMode = 2
  FaceMakerClass = Part::FaceMakerBullseye
  FaceMakerMode = 3
  LengthFwd = 12.8
  LengthRev = 0
  Solid = true
  Symmetric = true
FEATURE [Sketcher::SketchObject] Sketch013  label="buco pompa"
  ArcFitTolerance = 1e-06
  AttachmentSupport = -> [XZ_Plane]
  ExternalGeometry = -> [Sketch]
  FullyConstrained = true
  MakeInternals = false
  MapMode = 5
  Placement = pos=(0,0,0) rot=(1,0,0;1.5708rad)
  sketch-geometry (8):
    g0: LineSegment StartX=-82.8 StartY=-10.4 StartZ=0 EndX=-82.8 EndY=-9.6 EndZ=0
    g1: LineSegment StartX=-82.8 StartY=-9.6 StartZ=0 EndX=-67.9 EndY=-9.6 EndZ=0
    g2: LineSegment StartX=-67.9 StartY=-9.6 StartZ=0 EndX=-67.9 EndY=6 EndZ=0
    g3: LineSegment StartX=-67.9 StartY=6 StartZ=0 EndX=-65.9 EndY=6 EndZ=0
    g4: LineSegment StartX=-65.9 StartY=6 StartZ=0 EndX=-65.9 EndY=-1.7 EndZ=0
    g5: LineSegment StartX=-65.9 StartY=-1.7 StartZ=0 EndX=-57.2 EndY=-1.7 EndZ=0
    g6: LineSegment StartX=-57.2 StartY=-1.7 StartZ=0 EndX=-57.2 EndY=-10.4 EndZ=0
    g7: LineSegment StartX=-57.2 StartY=-10.4 StartZ=0 EndX=-82.8 EndY=-10.4 EndZ=0
  constraints (22):
    c: Vertical(g0)
    c: Coincident(g1,g0)
    c: Horizontal(g1)
    c: Coincident(g2,g1)
    c: Vertical(g2)
    c: Coincident(g3,g2)
    c: Horizontal(g3)
    c: Coincident(g4,g3)
    c: Vertical(g4)
    c: Coincident(g5,g4)
    c: Horizontal(g5)
    c: Coincident(g6,g5)
    c: Vertical(g6)
    c: Coincident(g7,g6)
    c: Coincident(g7,g0)
    c: DistanceY(g0,g0) = 0.8
    c: DistanceY(g6,g6) = 8.7
    c: DistanceX(g1,g1) = 14.9
    c: DistanceX(g3,g3) = 2
    c: Coincident(g0,g-4)
    c: DistanceY(g2,g-6) = 0
    c: Coincident(g6,g-5)
FEATURE [Part::Extrusion] Extrude009  label="Extrude buco pompa"
  Base = -> Sketch013
  Dir = (0,-1,2e-16)
  DirMode = 2
  FaceMakerClass = Part::FaceMakerBullseye
  FaceMakerMode = 3
  LengthFwd = 13.2
  LengthRev = 0
  Solid = true
  Symmetric = true
FEATURE [Sketcher::SketchObject] Sketch014  label="buco frontale"
  ArcFitTolerance = 1e-06
  AttachmentSupport = -> [XZ_Plane]
  ExternalGeometry = -> [Sketch]
  FullyConstrained = true
  MakeInternals = false
  MapMode = 5
  Placement = pos=(0,0,0) rot=(1,0,0;1.5708rad)
  sketch-geometry (10):
    g0: LineSegment StartX=0 StartY=0 StartZ=0 EndX=0 EndY=24.671 EndZ=0
    g1: LineSegment StartX=0 StartY=24.671 StartZ=0 EndX=-4 EndY=24.671 EndZ=0
    g2: LineSegment StartX=-4 StartY=24.671 StartZ=0 EndX=-4 EndY=16 EndZ=0
    g3: LineSegment StartX=-4 StartY=16 StartZ=0 EndX=-2.4 EndY=16 EndZ=0
    g4: LineSegment StartX=-2.4 StartY=16 StartZ=0 EndX=-2.4 EndY=10 EndZ=0
    g5: LineSegment StartX=-2.4 StartY=10 StartZ=0 EndX=-12 EndY=10 EndZ=0
    g6: LineSegment StartX=-12 StartY=10 StartZ=0 EndX=-12 EndY=6 EndZ=0
    g7: LineSegment StartX=-12 StartY=6 StartZ=0 EndX=-2.4 EndY=6 EndZ=0
    g8: LineSegment StartX=-2.4 StartY=6 StartZ=0 EndX=-2.4 EndY=0 EndZ=0
    g9: LineSegment StartX=-2.4 StartY=0 StartZ=0 EndX=0 EndY=0 EndZ=0
  constraints (29):
    c: Vertical(g0)
    c: Coincident(g1,g0)
    c: Horizontal(g1)
    c: Coincident(g2,g1)
    c: Vertical(g2)
    c: Coincident(g3,g2)
    c: Horizontal(g3)
    c: Coincident(g4,g3)
    c: Vertical(g4)
    c: Coincident(g5,g4)
    c: Horizontal(g5)
    c: Coincident(g6,g5)
    c: Vertical(g6)
    c: Coincident(g7,g6)
    c: Coincident(g8,g7)
    c: Vertical(g8)
    c: Coincident(g9,g8)
    c: Coincident(g9,g0)
    c: Horizontal(g9)
    c: DistanceY(g0,g0) = 24.671
    c: Horizontal(g7)
    c: DistanceY(g6,g6) = 4
    c: DistanceY(g4,g4) = 6
    c: DistanceX(g9,g9) = 2.4
    c: Coincident(g0,g-1)
    c: DistanceY(g-3,g7) = 0
    c: DistanceX(g8,g4) = 0
    c: DistanceX(g-3,g1) = 0
    c: DistanceX(g6,g-3) = 8
FEATURE [Part::Extrusion] Extrude010  label="Extrude buco frontale"
  Base = -> Sketch014
  Dir = (0,-1,2e-16)
  DirMode = 2
  FaceMakerClass = Part::FaceMakerBullseye
  FaceMakerMode = 3
  LengthFwd = 11.2
  LengthRev = 0
  Solid = true
  Symmetric = true
FEATURE [Sketcher::SketchObject] Sketch015  label="guida rail"
  ArcFitTolerance = 1e-06
  AttachmentSupport = -> [XZ_Plane]
  ExternalGeometry = -> [Sketch]
  FullyConstrained = true
  MakeInternals = false
  MapMode = 5
  Placement = pos=(0,0,0) rot=(1,0,0;1.5708rad)
  sketch-geometry (4):
    g0: LineSegment StartX=-100.8 StartY=43.2 StartZ=0 EndX=-44.6 EndY=43.2 EndZ=0
    g1: LineSegment StartX=-44.6 StartY=43.2 StartZ=0 EndX=-44.6 EndY=41.2 EndZ=0
    g2: LineSegment StartX=-44.6 StartY=41.2 StartZ=0 EndX=-100.8 EndY=41.2 EndZ=0
    g3: LineSegment StartX=-100.8 StartY=41.2 StartZ=0 EndX=-100.8 EndY=43.2 EndZ=0
  constraints (9):
    c: Horizontal(g0)
    c: Coincident(g1,g0)
    c: Coincident(g2,g1)
    c: Coincident(g3,g2)
    c: Coincident(g3,g0)
    c: Vertical(g3)
    c: Coincident(g2,g-3)
    c: Coincident(g1,g-3)
    c: Coincident(g0,g-4)
FEATURE [Part::Extrusion] Extrude011  label="Extrude guida rail"
  Base = -> Sketch015
  Dir = (0,-1,2e-16)
  DirMode = 2
  FaceMakerClass = Part::FaceMakerBullseye
  FaceMakerMode = 3
  LengthFwd = 9
  LengthRev = 0
  Solid = true
  Symmetric = true
FEATURE [Sketcher::SketchObject] Sketch016  label="guide per coperture laterali"
  ArcFitTolerance = 1e-06
  AttachmentSupport = -> [XZ_Plane]
  ExternalGeometry = -> [Sketch]
  FullyConstrained = true
  MakeInternals = false
  MapMode = 5
  Placement = pos=(0,0,0) rot=(1,0,0;1.5708rad)
  sketch-geometry (14):
    g0: Circle CenterX=-5.6 CenterY=7.6 CenterZ=0 NormalX=0 NormalY=0 NormalZ=1 AngleXU=0 Radius=1.6
    g1: Circle CenterX=-5.6 CenterY=7.6 CenterZ=0 NormalX=0 NormalY=0 NormalZ=1 AngleXU=0 Radius=4
    g2: Circle CenterX=-5.6 CenterY=34.8 CenterZ=0 NormalX=0 NormalY=0 NormalZ=1 AngleXU=0 Radius=1.6
    g3: Circle CenterX=-5.6 CenterY=34.8 CenterZ=0 NormalX=0 NormalY=0 NormalZ=1 AngleXU=0 Radius=4
    g4: Circle CenterX=-184.08 CenterY=34.8 CenterZ=0 NormalX=0 NormalY=0 NormalZ=1 AngleXU=0 Radius=1.6
    g5: Circle CenterX=-184.08 CenterY=34.8 CenterZ=0 NormalX=0 NormalY=0 NormalZ=1 AngleXU=0 Radius=4
    g6: Circle CenterX=-179.305 CenterY=-76.8316 CenterZ=0 NormalX=0 NormalY=0 NormalZ=1 AngleXU=0 Radius=1.6
    g7: Circle CenterX=-179.305 CenterY=-76.8316 CenterZ=0 NormalX=0 NormalY=0 NormalZ=1 AngleXU=0 Radius=4
    g8: Circle CenterX=-213.443 CenterY=-76.8316 CenterZ=0 NormalX=0 NormalY=0 NormalZ=1 AngleXU=0 Radius=1.6
    g9: Circle CenterX=-213.443 CenterY=-76.8316 CenterZ=0 NormalX=0 NormalY=0 NormalZ=1 AngleXU=0 Radius=4
    g10: Circle CenterX=-78.51 CenterY=7.6 CenterZ=0 NormalX=0 NormalY=0 NormalZ=1 AngleXU=0 Radius=1.6
    g11: Circle CenterX=-78.51 CenterY=7.6 CenterZ=0 NormalX=0 NormalY=0 NormalZ=1 AngleXU=0 Radius=4
    g12: Circle CenterX=-78.51 CenterY=34.8 CenterZ=0 NormalX=0 NormalY=0 NormalZ=1 AngleXU=0 Radius=1.6
    g13: Circle CenterX=-78.51 CenterY=34.8 CenterZ=0 NormalX=0 NormalY=0 NormalZ=1 AngleXU=0 Radius=4
  constraints (35):
    c: Diameter(g0) = 3.2
    c: Diameter(g1) = 8
    c: Coincident(g0,g1)
    c: Diameter(g2) = 3.2
    c: Diameter(g3) = 8
    c: Coincident(g3,g2)
    c: Tangent(g2,g-7)
    c: Diameter(g4) = 3.2
    c: Diameter(g5) = 8
    c: Coincident(g5,g4)
    c: Tangent(g4,g-7)
    c: Tangent(g4,g-8)
    c: Diameter(g6) = 3.2
    c: Diameter(g7) = 8
    c: Coincident(g7,g6)
    c: Tangent(g6,g-9)
    c: Tangent(g6,g-10)
    c: Diameter(g8) = 3.2
    c: Diameter(g9) = 8
    c: Coincident(g9,g8)
    c: Tangent(g8,g-10)
    c: Tangent(g8,g-11)
    c: Diameter(g10) = 3.2
    c: Diameter(g11) = 8
    c: Diameter(g12) = 3.2
    c: Diameter(g13) = 8
    c: Coincident(g12,g13)
    c: Coincident(g10,g11)
    c: Tangent(g12,g-7)
    c: DistanceX(g12,g10) = 0
    c: Tangent(g2,g-6)
    c: Tangent(g0,g-6)
    c: Tangent(g0,g-3)
    c: Tangent(g10,g-3)
    c: Tangent(g10,g-4)
FEATURE [Part::Extrusion] Extrude012  label="extrude guide per coperture laterali"
  Base = -> Sketch016
  Dir = (0,-1,2e-16)
  DirMode = 2
  FaceMakerClass = Part::FaceMakerBullseye
  FaceMakerMode = 3
  LengthFwd = 25.2
  LengthRev = 0
  Solid = true
  Symmetric = true
FEATURE [Sketcher::SketchObject] Sketch017  label="supporto CAM"
  ArcFitTolerance = 1e-06
  AttachmentSupport = -> [XZ_Plane]
  ExternalGeometry = -> [Sketch]
  FullyConstrained = true
  MakeInternals = false
  MapMode = 5
  Placement = pos=(0,0,0) rot=(1,0,0;1.5708rad)
  sketch-geometry (6):
    g0: LineSegment StartX=-2.4 StartY=48 StartZ=0 EndX=-2.4 EndY=41.2 EndZ=0
    g1: LineSegment StartX=-2.4 StartY=48 StartZ=0 EndX=-34 EndY=48 EndZ=0
    g2: LineSegment StartX=-34 StartY=48 StartZ=0 EndX=-34 EndY=46.72 EndZ=0
    g3: LineSegment StartX=-34 StartY=46.72 StartZ=0 EndX=-36 EndY=46.72 EndZ=0
    g4: LineSegment StartX=-36 StartY=46.72 StartZ=0 EndX=-36 EndY=41.2 EndZ=0
    g5: LineSegment StartX=-36 StartY=41.2 StartZ=0 EndX=-2.4 EndY=41.2 EndZ=0
  constraints (15):
    c: Coincident(g1,g0)
    c: Horizontal(g1)
    c: Coincident(g2,g1)
    c: Vertical(g2)
    c: Coincident(g3,g2)
    c: Horizontal(g3)
    c: Coincident(g4,g3)
    c: Coincident(g5,g4)
    c: DistanceX(g1,g0) = 31.6
    c: Coincident(g5,g0)
    c: Vertical(g4)
    c: DistanceY(g2,g1) = 1.28
    c: Coincident(g0,g-3)
    c: Coincident(g0,g-3)
    c: Coincident(g4,g-4)
FEATURE [Part::Extrusion] Extrude013  label="Extrude supporto CAM"
  Base = -> Sketch017
  Dir = (0,-1,2e-16)
  DirMode = 2
  FaceMakerClass = Part::FaceMakerBullseye
  FaceMakerMode = 3
  LengthFwd = 17.8
  LengthRev = 0
  Solid = true
  Symmetric = true
FEATURE [Sketcher::SketchObject] Sketch018  label="Scavo CAM"
  ArcFitTolerance = 1e-06
  AttachmentSupport = -> [YZ_Plane]
  ExternalGeometry = -> [Sketch]
  FullyConstrained = true
  MakeInternals = false
  MapMode = 5
  Placement = pos=(0,0,0) rot=(0.57735,0.57735,0.57735;2.0944rad)
  sketch-geometry (4):
    g0: LineSegment StartX=-7.73 StartY=48 StartZ=0 EndX=7.73 EndY=48 EndZ=0
    g1: LineSegment [constr] StartX=1.07e-14 StartY=48 StartZ=0 EndX=0 EndY=43.5155 EndZ=0
    g2: ArcOfCircle CenterX=9e-15 CenterY=52.42 CenterZ=0 NormalX=0 NormalY=0 NormalZ=1 AngleXU=0 Radius=8.90445 StartAngle=3.66102 EndAngle=5.76376
    g3: Circle [constr] CenterX=9e-15 CenterY=52.42 CenterZ=0 NormalX=0 NormalY=0 NormalZ=1 AngleXU=0 Radius=8.9
  constraints (13):
    c: Horizontal(g0)
    c: DistanceY(g-3,g0) = 0
    c: DistanceX(g0,g0) = 15.46
    c: DistanceX(g0,g-3) = 7.73
    c: DistanceX(g-3) = 0
    c: Coincident(g1,g-3)
    c: PointOnObject(g1,g-2)
    c: Coincident(g2,g0)
    c: Coincident(g2,g0)
    c: PointOnObject(g1,g2)
    c: Diameter(g3) = 17.8
    c: DistanceY(g1,g3) = 4.42
    c: Coincident(g2,g3)
FEATURE [Part::Extrusion] Extrude014  label="Extrude Scavo CAM"
  Base = -> Sketch018
  Dir = (1,0,0)
  DirMode = 2
  FaceMakerClass = Part::FaceMakerBullseye
  FaceMakerMode = 3
  LengthFwd = -34
  LengthRev = 0
  Solid = true
  Symmetric = false
FEATURE [Sketcher::SketchObject] Sketch019  label="scavo rumble"
  ArcFitTolerance = 1e-06
  AttachmentSupport = -> [XZ_Plane]
  ExternalGeometry = -> [Sketch]
  FullyConstrained = true
  MakeInternals = false
  MapMode = 5
  Placement = pos=(0,0,0) rot=(1,0,0;1.5708rad)
  sketch-geometry (6):
    g0: LineSegment StartX=-164.575 StartY=-24.3786 StartZ=0 EndX=-159.439 EndY=-26.0473 EndZ=0
    g1: LineSegment StartX=-159.439 StartY=-26.0473 StartZ=0 EndX=-166.547 EndY=-47.9216 EndZ=0
    g2: LineSegment StartX=-166.547 StartY=-47.9216 StartZ=0 EndX=-171.682 EndY=-46.2529 EndZ=0
    g3: LineSegment StartX=-171.682 StartY=-46.2529 StartZ=0 EndX=-164.575 EndY=-24.3786 EndZ=0
    g4: LineSegment [constr] StartX=-145.51 StartY=22 StartZ=0 EndX=-160.961 EndY=-25.5528 EndZ=0
    g5: LineSegment [constr] StartX=-159.439 StartY=-26.0473 StartZ=0 EndX=-160.961 EndY=-25.5528 EndZ=0
  constraints (17):
    c: Coincident(g1,g0)
    c: Coincident(g2,g1)
    c: Coincident(g3,g2)
    c: Coincident(g3,g0)
    c: Parallel(g3,g-3)
    c: Parallel(g3,g1)
    c: Perpendicular(g3,g0)
    c: Perpendicular(g2,g3)
    c: Distance(g2,g0) = 23
    c: Parallel(g4,g-3)
    c: Distance(g4) = 50
    c: Coincident(g4,g-3)
    c: Parallel(g5,g0)
    c: Distance(g5) = 1.6
    c: Coincident(g5,g0)
    c: Distance(g5,g0) = 3.8
    c: Coincident(g5,g4)
FEATURE [Part::Extrusion] Extrude015  label="scavo rumble001"
  Base = -> Sketch019
  Dir = (0,-1,2e-16)
  DirMode = 2
  FaceMakerClass = Part::FaceMakerBullseye
  FaceMakerMode = 3
  LengthFwd = 21
  LengthRev = 0
  Solid = true
  Symmetric = true
FEATURE [Sketcher::SketchObject] Sketch020  label="fermo rumble"
  ArcFitTolerance = 1e-06
  AttachmentSupport = -> [XZ_Plane]
  ExternalGeometry = -> [Sketch019,Sketch]
  FullyConstrained = true
  MakeInternals = false
  MapMode = 5
  Placement = pos=(0,0,0) rot=(1,0,0;1.5708rad)
  sketch-geometry (16):
    g0: LineSegment [constr] StartX=-166.709 StartY=-43.2425 StartZ=0 EndX=-168.068 EndY=-47.4271 EndZ=0
    g1: LineSegment [constr] StartX=-168.068 StartY=-47.4271 StartZ=0 EndX=-166.547 EndY=-47.9216 EndZ=0
    g2: LineSegment StartX=-168.121 StartY=-40.4703 StartZ=0 EndX=-166.029 EndY=-41.1502 EndZ=0
    g3: LineSegment StartX=-166.029 StartY=-41.1502 StartZ=0 EndX=-166.709 EndY=-43.2425 EndZ=0
    g4: LineSegment StartX=-166.709 StartY=-43.2425 StartZ=0 EndX=-168.801 EndY=-42.5626 EndZ=0
    g5: LineSegment StartX=-168.801 StartY=-42.5626 StartZ=0 EndX=-168.121 EndY=-40.4703 EndZ=0
    g6: LineSegment StartX=-167.627 StartY=-38.9486 StartZ=0 EndX=-164.203 EndY=-40.0611 EndZ=0
    g7: LineSegment StartX=-164.203 StartY=-40.0611 StartZ=0 EndX=-165.81 EndY=-45.0066 EndZ=0
    g8: LineSegment StartX=-165.81 StartY=-45.0066 StartZ=0 EndX=-169.234 EndY=-43.8941 EndZ=0
    g9: LineSegment StartX=-170.261 StartY=-41.878 StartZ=0 EndX=-169.643 EndY=-39.9759 EndZ=0
    g10: LineSegment [constr] StartX=-169.643 StartY=-39.9759 StartZ=0 EndX=-169.148 EndY=-38.4542 EndZ=0
    g11: LineSegment [constr] StartX=-169.148 StartY=-38.4542 StartZ=0 EndX=-167.627 EndY=-38.9486 EndZ=0
    g12: ArcOfCircle CenterX=-168.739 CenterY=-42.3724 CenterZ=0 NormalX=0 NormalY=0 NormalZ=1 AngleXU=0 Radius=1.6 StartAngle=2.82743 EndAngle=4.39823
    g13: GeomPoint [constr] X=-170.755 Y=-43.3997 Z=0
    g14: ArcOfCircle CenterX=-168.121 CenterY=-40.4703 CenterZ=0 NormalX=0 NormalY=0 NormalZ=1 AngleXU=0 Radius=1.6 StartAngle=1.25664 EndAngle=2.82743
    g15: GeomPoint [constr] X=-169.148 Y=-38.4542 Z=0
  constraints (42):
    c: Parallel(g0,g-4)
    c: Distance(g0) = 4.4
    c: Coincident(g1,g0)
    c: Perpendicular(g0,g1)
    c: Distance(g1) = 1.6
    c: Coincident(g1,g-5)
    c: Coincident(g3,g2)
    c: Coincident(g4,g3)
    c: Coincident(g5,g4)
    c: Coincident(g5,g2)
    c: Parallel(g3,g-4)
    c: Parallel(g3,g5)
    c: Perpendicular(g2,g3)
    c: Parallel(g4,g2)
    c: Distance(g2) = 2.2
    c: Distance(g3) = 2.2
    c: Coincident(g7,g6)
    c: Coincident(g8,g7)
    c: Parallel(g7,g-4)
    c: Parallel(g7,g9)
    c: Perpendicular(g6,g7)
    c: Parallel(g6,g8)
    c: Distance(g6,g15) = 5.2
    c: Distance(g7) = 5.2
    c: Coincident(g11,g10)
    c: Parallel(g10,g9)
    c: Parallel(g11,g6)
    c: Distance(g10) = 1.6
    c: Distance(g11) = 1.6
    c: Coincident(g10,g15)
    c: Distance(g11,g2) = 1.6
    c: Distance(g2,g10) = 1.6
    c: PointOnObject(g13,g8)
    c: PointOnObject(g13,g9)
    c: Tangent(g8,g12) = 1.5708
    c: Tangent(g9,g12) = 1.5708
    c: PointOnObject(g15,g9)
    c: Tangent(g6,g14) = 1.5708
    c: Tangent(g9,g14) = 1.5708
    c: Equal(g12,g14)
    c: Coincident(g6,g11)
    c: Coincident(g3,g0)
FEATURE [Part::Extrusion] Extrude016  label="Extrude fermo rumble"
  Base = -> Sketch020
  Dir = (0,-1,2e-16)
  DirMode = 2
  FaceMakerClass = Part::FaceMakerBullseye
  FaceMakerMode = 3
  LengthFwd = 25.2
  LengthRev = 0
  Solid = true
  Symmetric = true
FEATURE [Sketcher::SketchObject] Sketch021  label="perno fermo rumble001"
  ArcFitTolerance = 1e-06
  AttachmentSupport = -> [XZ_Plane001]
  FullyConstrained = true
  MakeInternals = false
  MapMode = 5
  Placement = pos=(0,0,0) rot=(1,0,0;1.5708rad)
  sketch-geometry (16):
    g0: LineSegment StartX=0 StartY=0.45 StartZ=0 EndX=0 EndY=1.55 EndZ=0
    g1: LineSegment StartX=0.45 StartY=2 StartZ=0 EndX=1.55 EndY=2 EndZ=0
    g2: LineSegment StartX=2 StartY=1.55 StartZ=0 EndX=2 EndY=0.45 EndZ=0
    g3: LineSegment StartX=1.55 StartY=0 StartZ=0 EndX=0.45 EndY=0 EndZ=0
    g4: ArcOfCircle [constr] CenterX=0.45 CenterY=1.55 CenterZ=0 NormalX=0 NormalY=0 NormalZ=1 AngleXU=0 Radius=0.45 StartAngle=1.5708 EndAngle=3.14159
    g5: GeomPoint [constr] X=0 Y=2 Z=0
    g6: LineSegment StartX=0.45 StartY=2 StartZ=0 EndX=0 EndY=1.55 EndZ=0
    g7: ArcOfCircle [constr] CenterX=1.55 CenterY=1.55 CenterZ=0 NormalX=0 NormalY=0 NormalZ=1 AngleXU=0 Radius=0.45 StartAngle=0 EndAngle=1.5708
    g8: GeomPoint [constr] X=2 Y=2 Z=0
    g9: LineSegment StartX=2 StartY=1.55 StartZ=0 EndX=1.55 EndY=2 EndZ=0
    g10: ArcOfCircle [constr] CenterX=1.55 CenterY=0.45 CenterZ=0 NormalX=0 NormalY=0 NormalZ=1 AngleXU=0 Radius=0.45 StartAngle=4.71239 EndAngle=6.28319
    g11: GeomPoint [constr] X=2 Y=0 Z=0
    g12: LineSegment StartX=1.55 StartY=0 StartZ=0 EndX=2 EndY=0.45 EndZ=0
    g13: ArcOfCircle [constr] CenterX=0.45 CenterY=0.45 CenterZ=0 NormalX=0 NormalY=0 NormalZ=1 AngleXU=0 Radius=0.45 StartAngle=3.14159 EndAngle=4.71239
    g14: GeomPoint [constr] X=0 Y=0 Z=0
    g15: LineSegment StartX=0 StartY=0.45 StartZ=0 EndX=0.45 EndY=0 EndZ=0
  constraints (35):
    c: Coincident(g14,g-1)
    c: PointOnObject(g5,g-2)
    c: Horizontal(g1)
    c: Vertical(g2)
    c: Horizontal(g3)
    c: DistanceX(g5,g8) = 2
    c: DistanceY(g11,g8) = 2
    c: PointOnObject(g5,g0)
    c: PointOnObject(g5,g1)
    c: Tangent(g0,g4) = 1.5708
    c: Tangent(g1,g4) = 1.5708
    c: Coincident(g6,g0)
    c: Coincident(g6,g1)
    c: PointOnObject(g8,g2)
    c: PointOnObject(g8,g1)
    c: Tangent(g2,g7) = 1.5708
    c: Tangent(g1,g7) = 1.5708
    c: Coincident(g9,g2)
    c: Coincident(g9,g1)
    c: PointOnObject(g11,g2)
    c: PointOnObject(g11,g3)
    c: Tangent(g2,g10) = 1.5708
    c: Tangent(g3,g10) = 1.5708
    c: Coincident(g12,g2)
    c: Coincident(g12,g3)
    c: PointOnObject(g14,g0)
    c: PointOnObject(g14,g3)
    c: Tangent(g0,g13) = 1.5708
    c: Tangent(g3,g13) = 1.5708
    c: Coincident(g15,g0)
    c: Coincident(g15,g3)
    c: Equal(g6,g9)
    c: Equal(g9,g12)
    c: Equal(g12,g15)
    c: DistanceX(g14,g3) = 0.45
FEATURE [Part::Extrusion] Extrude017  label="Extrude perno fermo rumble"
  Base = -> Sketch021
  Dir = (0,-1,2e-16)
  DirMode = 2
  FaceMakerClass = Part::FaceMakerBullseye
  FaceMakerMode = 3
  LengthFwd = 25.2
  LengthRev = 0
  Solid = true
  Symmetric = true
FEATURE [Sketcher::SketchObject] Sketch022  label="fori per M3x5(OD)x6(L)"
  ArcFitTolerance = 1e-06
  AttachmentSupport = -> [XZ_Plane]
  ExternalGeometry = -> [Sketch016]
  FullyConstrained = true
  MakeInternals = false
  MapMode = 5
  Placement = pos=(0,0,0) rot=(1,0,0;1.5708rad)
  sketch-geometry (7):
    g0: Circle CenterX=-5.6 CenterY=34.8 CenterZ=0 NormalX=0 NormalY=0 NormalZ=1 AngleXU=0 Radius=2.5
    g1: Circle CenterX=-5.6 CenterY=7.6 CenterZ=0 NormalX=0 NormalY=0 NormalZ=1 AngleXU=0 Radius=2.5
    g2: Circle CenterX=-78.51 CenterY=34.8 CenterZ=0 NormalX=0 NormalY=0 NormalZ=1 AngleXU=0 Radius=2.5
    g3: Circle CenterX=-78.51 CenterY=7.6 CenterZ=0 NormalX=0 NormalY=0 NormalZ=1 AngleXU=0 Radius=2.5
    g4: Circle CenterX=-184.08 CenterY=34.8 CenterZ=0 NormalX=0 NormalY=0 NormalZ=1 AngleXU=0 Radius=2.5
    g5: Circle CenterX=-179.305 CenterY=-76.8316 CenterZ=0 NormalX=0 NormalY=0 NormalZ=1 AngleXU=0 Radius=2.5
    g6: Circle CenterX=-213.443 CenterY=-76.8316 CenterZ=0 NormalX=0 NormalY=0 NormalZ=1 AngleXU=0 Radius=2.5
  constraints (14):
    c: Diameter(g0) = 5
    c: Diameter(g1) = 5
    c: Diameter(g2) = 5
    c: Diameter(g3) = 5
    c: Diameter(g4) = 5
    c: Diameter(g5) = 5
    c: Diameter(g6) = 5
    c: Coincident(g0,g-8)
    c: Coincident(g1,g-9)
    c: Coincident(g2,g-6)
    c: Coincident(g3,g-7)
    c: Coincident(g4,g-5)
    c: Coincident(g5,g-4)
    c: Coincident(g6,g-3)
FEATURE [Part::Extrusion] Extrude018  label="Extrude fori M3x5x6 - dx"
  Base = -> Sketch022
  Dir = (0,-1,2e-16)
  DirMode = 2
  FaceMakerClass = Part::FaceMakerBullseye
  FaceMakerMode = 3
  LengthFwd = 6.2
  LengthRev = 0
  Placement = pos=(0,-9.5,0) rot=(0,0,1;0rad)
  Solid = true
  Symmetric = true
FEATURE [Part::Extrusion] Extrude019  label="Extrude fori M3x5x6 - sx"
  Base = -> Sketch022
  Dir = (0,-1,2e-16)
  DirMode = 2
  FaceMakerClass = Part::FaceMakerBullseye
  FaceMakerMode = 3
  LengthFwd = 6.2
  LengthRev = 0
  Placement = pos=(0,9.5,0) rot=(0,0,1;0rad)
  Solid = true
  Symmetric = true
FEATURE [Sketcher::SketchObject] Sketch023  label="foro anteriore M3x5x6"
  ArcFitTolerance = 1e-06
  AttachmentSupport = -> [YZ_Plane]
  FullyConstrained = true
  MakeInternals = false
  MapMode = 5
  Placement = pos=(0,0,0) rot=(0.57735,0.57735,0.57735;2.0944rad)
  sketch-geometry (2):
    g0: LineSegment [constr] StartX=0 StartY=0 StartZ=0 EndX=0 EndY=38.6 EndZ=0
    g1: Circle CenterX=0 CenterY=38.6 CenterZ=0 NormalX=0 NormalY=0 NormalZ=1 AngleXU=0 Radius=2.5
  constraints (5):
    c: Coincident(g0,g-1)
    c: PointOnObject(g0,g-2)
    c: DistanceY(g0,g0) = 38.6
    c: Diameter(g1) = 5
    c: Coincident(g1,g0)
FEATURE [Part::Extrusion] Extrude020  label="Extrude foro anteriore M3x5x6"
  Base = -> Sketch023
  Dir = (1,0,0)
  DirMode = 2
  FaceMakerClass = Part::FaceMakerBullseye
  FaceMakerMode = 3
  LengthFwd = -6.2
  LengthRev = 0
  Solid = true
  Symmetric = false
FEATURE [Sketcher::SketchObject] Sketch024  label="fori per viti frontale"
  ArcFitTolerance = 1e-06
  AttachmentSupport = -> [YZ_Plane]
  FullyConstrained = true
  MakeInternals = false
  MapMode = 5
  Placement = pos=(0,0,0) rot=(0.57735,0.57735,0.57735;2.0944rad)
  sketch-geometry (9):
    g0: LineSegment [constr] StartX=-10.3 StartY=30.721 StartZ=0 EndX=10.3 EndY=30.721 EndZ=0
    g1: LineSegment [constr] StartX=10.3 StartY=30.721 StartZ=0 EndX=10.3 EndY=10.121 EndZ=0
    g2: LineSegment [constr] StartX=10.3 StartY=10.121 StartZ=0 EndX=-10.3 EndY=10.121 EndZ=0
    g3: LineSegment [constr] StartX=-10.3 StartY=10.121 StartZ=0 EndX=-10.3 EndY=30.721 EndZ=0
    g4: LineSegment [constr] StartX=0 StartY=0 StartZ=0 EndX=0 EndY=10.121 EndZ=0
    g5: Circle CenterX=-10.3 CenterY=30.721 CenterZ=0 NormalX=0 NormalY=0 NormalZ=1 AngleXU=0 Radius=2
    g6: Circle CenterX=10.3 CenterY=30.721 CenterZ=0 NormalX=0 NormalY=0 NormalZ=1 AngleXU=0 Radius=2
    g7: Circle CenterX=-10.3 CenterY=10.121 CenterZ=0 NormalX=0 NormalY=0 NormalZ=1 AngleXU=0 Radius=2
    g8: Circle CenterX=10.3 CenterY=10.121 CenterZ=0 NormalX=0 NormalY=0 NormalZ=1 AngleXU=0 Radius=2
  constraints (22):
    c: Horizontal(g0)
    c: Coincident(g1,g0)
    c: Vertical(g1)
    c: Coincident(g2,g1)
    c: Horizontal(g2)
    c: Coincident(g3,g2)
    c: Coincident(g3,g0)
    c: Vertical(g3)
    c: DistanceX(g0,g0) = 20.6
    c: DistanceY(g3,g3) = 20.6
    c: Coincident(g4,g-1)
    c: PointOnObject(g4,g-2)
    c: DistanceY(g4,g4) = 10.121
    c: Symmetric(g2,g2,g4)
    c: Diameter(g5) = 4
    c: Diameter(g6) = 4
    c: Diameter(g7) = 4
    c: Diameter(g8) = 4
    c: Coincident(g5,g0)
    c: Coincident(g6,g0)
    c: Coincident(g7,g2)
    c: Coincident(g8,g1)
FEATURE [Part::Extrusion] Extrude021  label="Extrude fori per viti frontale"
  Base = -> Sketch024
  Dir = (1,0,0)
  DirMode = 2
  FaceMakerClass = Part::FaceMakerBullseye
  FaceMakerMode = 3
  LengthFwd = -2.4
  LengthRev = 0
  Solid = true
  Symmetric = false
FEATURE [Sketcher::SketchObject] Sketch025  label="foro per filo CAM"
  ArcFitTolerance = 1e-06
  AttachmentSupport = -> [XZ_Plane]
  ExternalGeometry = -> [Sketch]
  FullyConstrained = true
  MakeInternals = false
  MapMode = 5
  Placement = pos=(0,0,0) rot=(1,0,0;1.5708rad)
  sketch-geometry (4):
    g0: LineSegment StartX=-44.6 StartY=41.2 StartZ=0 EndX=-44.6 EndY=36.4 EndZ=0
    g1: LineSegment StartX=-44.6 StartY=36.4 StartZ=0 EndX=-54.6 EndY=36.4 EndZ=0
    g2: LineSegment StartX=-54.6 StartY=36.4 StartZ=0 EndX=-50.4 EndY=41.2 EndZ=0
    g3: LineSegment StartX=-50.4 StartY=41.2 StartZ=0 EndX=-44.6 EndY=41.2 EndZ=0
  constraints (11):
    c: Vertical(g0)
    c: Coincident(g1,g0)
    c: Horizontal(g1)
    c: Coincident(g2,g1)
    c: Coincident(g3,g2)
    c: Coincident(g3,g0)
    c: Horizontal(g3)
    c: Coincident(g0,g-3)
    c: DistanceY(g0,g-4) = 0
    c: DistanceX(g3,g3) = 5.8
    c: DistanceX(g1,g1) = 10
FEATURE [Part::Extrusion] Extrude022  label="Extrude foro per filo CAM dx"
  Base = -> Sketch025
  Dir = (0,-1,2e-16)
  DirMode = 2
  FaceMakerClass = Part::FaceMakerBullseye
  FaceMakerMode = 3
  LengthFwd = 4.9
  LengthRev = 0
  Placement = pos=(0,6.95,0) rot=(0,0,1;0rad)
  Solid = true
  Symmetric = true
FEATURE [Part::Extrusion] Extrude023  label="Extrude foro per filo CAM sx"
  Base = -> Sketch025
  Dir = (0,-1,2e-16)
  DirMode = 2
  FaceMakerClass = Part::FaceMakerBullseye
  FaceMakerMode = 3
  LengthFwd = 4.9
  LengthRev = 0
  Placement = pos=(0,-6.95,0) rot=(0,0,1;0rad)
  Solid = true
  Symmetric = true
FEATURE [Sketcher::SketchObject] Sketch026  label="foro sotto anteriore M3x5x6"
  ArcFitTolerance = 1e-06
  AttachmentSupport = -> [XY_Plane]
  FullyConstrained = true
  MakeInternals = false
  MapMode = 5
  sketch-geometry (2):
    g0: LineSegment [constr] StartX=0 StartY=0 StartZ=0 EndX=-16.5 EndY=0 EndZ=0
    g1: Circle CenterX=-16.5 CenterY=0 CenterZ=0 NormalX=0 NormalY=0 NormalZ=1 AngleXU=0 Radius=2.5
  constraints (5):
    c: Distance(g0) = 16.5
    c: Coincident(g0,g-1)
    c: PointOnObject(g0,g-1)
    c: Diameter(g1) = 5
    c: Coincident(g0,g1)
FEATURE [Sketcher::SketchObject] Sketch027  label="foro sotto posteriore M3x5x6"
  ArcFitTolerance = 1e-06
  AttachmentSupport = -> [XY_Plane]
  ExternalGeometry = -> [Sketch]
  FullyConstrained = true
  MakeInternals = false
  MapMode = 5
  sketch-geometry (2):
    g0: LineSegment [constr] StartX=-82.8 StartY=2e-16 StartZ=0 EndX=-71.3 EndY=2e-16 EndZ=0
    g1: Circle CenterX=-71.3 CenterY=2e-16 CenterZ=0 NormalX=0 NormalY=0 NormalZ=1 AngleXU=0 Radius=2.5
  constraints (5):
    c: Distance(g0) = 11.5
    c: Coincident(g0,g-3)
    c: PointOnObject(g0,g-3)
    c: Diameter(g1) = 5
    c: Coincident(g1,g0)
FEATURE [Sketcher::SketchObject] Sketch029  label="fori sotto impugnatura"
  ArcFitTolerance = 1e-06
  AttachmentSupport = -> [XY_Plane]
  ExternalGeometry = -> [Sketch]
  FullyConstrained = true
  MakeInternals = false
  MapMode = 5
  sketch-geometry (15):
    g0: LineSegment [constr] StartX=-175.232 StartY=-1.83e-14 StartZ=0 EndX=-191.232 EndY=0 EndZ=0
    g1: Circle CenterX=-191.232 CenterY=0 CenterZ=0 NormalX=0 NormalY=0 NormalZ=1 AngleXU=0 Radius=3.95
    g2: LineSegment [constr] StartX=-175.232 StartY=-1.83e-14 StartZ=0 EndX=-204.275 EndY=0 EndZ=0
    g3: LineSegment StartX=-204.275 StartY=3.525 StartZ=0 EndX=-204.275 EndY=-3.525 EndZ=0
    g4: LineSegment StartX=-205.4 StartY=-4.65 StartZ=0 EndX=-206.65 EndY=-4.65 EndZ=0
    g5: LineSegment StartX=-207.775 StartY=-3.525 StartZ=0 EndX=-207.775 EndY=3.525 EndZ=0
    g6: LineSegment StartX=-206.65 StartY=4.65 StartZ=0 EndX=-205.4 EndY=4.65 EndZ=0
    g7: ArcOfCircle CenterX=-206.65 CenterY=3.525 CenterZ=0 NormalX=0 NormalY=0 NormalZ=1 AngleXU=0 Radius=1.125 StartAngle=1.5708 EndAngle=3.14159
    g8: GeomPoint [constr] X=-207.775 Y=4.65 Z=0
    g9: ArcOfCircle CenterX=-205.4 CenterY=3.525 CenterZ=0 NormalX=0 NormalY=0 NormalZ=1 AngleXU=0 Radius=1.125 StartAngle=0 EndAngle=1.5708
    g10: GeomPoint [constr] X=-204.275 Y=4.65 Z=0
    g11: ArcOfCircle CenterX=-205.4 CenterY=-3.525 CenterZ=0 NormalX=0 NormalY=0 NormalZ=1 AngleXU=0 Radius=1.125 StartAngle=4.71239 EndAngle=6.28319
    g12: GeomPoint [constr] X=-204.275 Y=-4.65 Z=0
    g13: ArcOfCircle CenterX=-206.65 CenterY=-3.525 CenterZ=0 NormalX=0 NormalY=0 NormalZ=1 AngleXU=0 Radius=1.125 StartAngle=3.14159 EndAngle=4.71239
    g14: GeomPoint [constr] X=-207.775 Y=-4.65 Z=0
  constraints (35):
    c: Distance(g0) = 16
    c: Coincident(g0,g-3)
    c: PointOnObject(g0,g-1)
    c: Diameter(g1) = 7.9
    c: Coincident(g1,g0)
    c: Coincident(g2,g0)
    c: PointOnObject(g2,g-1)
    c: Vertical(g3)
    c: Horizontal(g4)
    c: Vertical(g5)
    c: Horizontal(g6)
    c: DistanceY(g12,g10) = 9.3
    c: DistanceX(g8,g10) = 3.5
    c: Symmetric(g10,g12,g2)
    c: PointOnObject(g8,g5)
    c: PointOnObject(g8,g6)
    c: Tangent(g5,g7) = 1.5708
    c: Tangent(g6,g7) = 1.5708
    c: PointOnObject(g10,g3)
    c: PointOnObject(g10,g6)
    c: Tangent(g3,g9) = 1.5708
    c: Tangent(g6,g9) = 1.5708
    c: PointOnObject(g12,g3)
    c: PointOnObject(g12,g4)
    c: Tangent(g3,g11) = 1.5708
    c: Tangent(g4,g11) = 1.5708
    c: PointOnObject(g14,g4)
    c: PointOnObject(g14,g5)
    c: Tangent(g4,g13) = 1.5708
    c: Tangent(g5,g13) = 1.5708
    c: Equal(g7,g9)
    c: Equal(g9,g11)
    c: Equal(g11,g13)
    c: DistanceX(g6,g6) = 1.25
    c: DistanceX(g-5,g5) = 6.8
FEATURE [Sketcher::SketchObject] Sketch030  label="fori superiori per solenoide e oled"
  ArcFitTolerance = 1e-06
  AttachmentSupport = -> [XY_Plane]
  ExternalGeometry = -> [Sketch]
  FullyConstrained = true
  MakeInternals = false
  MapMode = 5
  sketch-geometry (33):
    g0: LineSegment [constr] StartX=-181.6 StartY=1.12e-14 StartZ=0 EndX=-169.91 EndY=0 EndZ=0
    g1: LineSegment [constr] StartX=-169.91 StartY=0 StartZ=0 EndX=-169.91 EndY=-2.6 EndZ=0
    g2: LineSegment [constr] StartX=-169.91 StartY=0 StartZ=0 EndX=-169.91 EndY=2.6 EndZ=0
    g3: LineSegment StartX=-169.91 StartY=4.975 StartZ=0 EndX=-169.91 EndY=8.225 EndZ=0
    g4: LineSegment StartX=-167.535 StartY=10.6 StartZ=0 EndX=-167.285 EndY=10.6 EndZ=0
    g5: LineSegment StartX=-164.91 StartY=8.225 StartZ=0 EndX=-164.91 EndY=4.975 EndZ=0
    g6: LineSegment StartX=-167.285 StartY=2.6 StartZ=0 EndX=-167.535 EndY=2.6 EndZ=0
    g7: LineSegment StartX=-169.91 StartY=-4.975 StartZ=0 EndX=-169.91 EndY=-8.225 EndZ=0
    g8: LineSegment StartX=-167.535 StartY=-10.6 StartZ=0 EndX=-167.285 EndY=-10.6 EndZ=0
    g9: LineSegment StartX=-164.91 StartY=-8.225 StartZ=0 EndX=-164.91 EndY=-4.975 EndZ=0
    g10: LineSegment StartX=-167.285 StartY=-2.6 StartZ=0 EndX=-167.535 EndY=-2.6 EndZ=0
    g11: ArcOfCircle CenterX=-167.535 CenterY=8.225 CenterZ=0 NormalX=0 NormalY=0 NormalZ=1 AngleXU=0 Radius=2.375 StartAngle=1.5708 EndAngle=3.14159
    g12: GeomPoint [constr] X=-169.91 Y=10.6 Z=0
    g13: ArcOfCircle CenterX=-167.285 CenterY=8.225 CenterZ=0 NormalX=0 NormalY=0 NormalZ=1 AngleXU=0 Radius=2.375 StartAngle=0 EndAngle=1.5708
    g14: GeomPoint [constr] X=-164.91 Y=10.6 Z=0
    g15: ArcOfCircle CenterX=-167.285 CenterY=4.975 CenterZ=0 NormalX=0 NormalY=0 NormalZ=1 AngleXU=0 Radius=2.375 StartAngle=4.71239 EndAngle=6.28319
    g16: GeomPoint [constr] X=-164.91 Y=2.6 Z=0
    g17: ArcOfCircle CenterX=-167.535 CenterY=4.975 CenterZ=0 NormalX=0 NormalY=0 NormalZ=1 AngleXU=0 Radius=2.375 StartAngle=3.14159 EndAngle=4.71239
    g18: GeomPoint [constr] X=-169.91 Y=2.6 Z=0
    g19: ArcOfCircle CenterX=-167.535 CenterY=-4.975 CenterZ=0 NormalX=0 NormalY=0 NormalZ=1 AngleXU=0 Radius=2.375 StartAngle=1.5708 EndAngle=3.14159
    g20: GeomPoint [constr] X=-169.91 Y=-2.6 Z=0
    g21: ArcOfCircle CenterX=-167.285 CenterY=-4.975 CenterZ=0 NormalX=0 NormalY=0 NormalZ=1 AngleXU=0 Radius=2.375 StartAngle=0 EndAngle=1.5708
    g22: GeomPoint [constr] X=-164.91 Y=-2.6 Z=0
    g23: ArcOfCircle CenterX=-167.285 CenterY=-8.225 CenterZ=0 NormalX=0 NormalY=0 NormalZ=1 AngleXU=0 Radius=2.375 StartAngle=4.71239 EndAngle=6.28319
    g24: GeomPoint [constr] X=-164.91 Y=-10.6 Z=0
    g25: ArcOfCircle CenterX=-167.535 CenterY=-8.225 CenterZ=0 NormalX=0 NormalY=0 NormalZ=1 AngleXU=0 Radius=2.375 StartAngle=3.14159 EndAngle=4.71239
    g26: GeomPoint [constr] X=-169.91 Y=-10.6 Z=0
    g27: LineSegment [constr] StartX=-181.6 StartY=1.12e-14 StartZ=0 EndX=-152.209 EndY=0 EndZ=0
    g28: LineSegment [constr] StartX=-181.6 StartY=1.12e-14 StartZ=0 EndX=-130.41 EndY=0 EndZ=0
    g29: LineSegment [constr] StartX=-152.209 StartY=0 StartZ=0 EndX=-152.209 EndY=6.95 EndZ=0
    g30: LineSegment [constr] StartX=-130.41 StartY=0 StartZ=0 EndX=-130.41 EndY=-6.95 EndZ=0
    g31: Circle CenterX=-152.209 CenterY=6.95 CenterZ=0 NormalX=0 NormalY=0 NormalZ=1 AngleXU=0 Radius=2.1
    g32: Circle CenterX=-130.41 CenterY=-6.95 CenterZ=0 NormalX=0 NormalY=0 NormalZ=1 AngleXU=0 Radius=2.1
  constraints (79):
    c: Distance(g0) = 11.69
    c: PointOnObject(g0,g-1)
    c: Coincident(g-4,g0)
    c: Distance(g1) = 2.6
    c: Coincident(g1,g0)
    c: Vertical(g1)
    c: Distance(g2) = 2.6
    c: Coincident(g2,g0)
    c: Vertical(g2)
    c: Distance(g18,g12) = 8
    c: Coincident(g18,g2)
    c: Vertical(g3)
    c: Distance(g14,g12) = 5
    c: Horizontal(g4)
    c: Distance(g16,g14) = 8
    c: Vertical(g5)
    c: Distance(g26,g20) = 8
    c: Coincident(g20,g1)
    c: Vertical(g7)
    c: Distance(g26,g24) = 5
    c: Horizontal(g8)
    c: Distance(g24,g22) = 8
    c: Vertical(g9)
    c: PointOnObject(g12,g3)
    c: PointOnObject(g12,g4)
    c: Tangent(g3,g11) = 1.5708
    c: Tangent(g4,g11) = 1.5708
    c: PointOnObject(g14,g5)
    c: PointOnObject(g14,g4)
    c: Tangent(g5,g13) = 1.5708
    c: Tangent(g4,g13) = 1.5708
    c: PointOnObject(g16,g5)
    c: PointOnObject(g16,g6)
    c: Tangent(g5,g15) = 1.5708
    c: Tangent(g6,g15) = 1.5708
    c: PointOnObject(g18,g3)
    c: PointOnObject(g18,g6)
    c: Tangent(g3,g17) = 1.5708
    c: Tangent(g6,g17) = 1.5708
    c: Equal(g11,g13)
    c: Equal(g13,g15)
    c: Equal(g15,g17)
    c: DistanceX(g4,g4) = 0.25
    c: PointOnObject(g20,g7)
    c: PointOnObject(g20,g10)
    c: Tangent(g7,g19) = -1.5708
    c: Tangent(g10,g19) = -1.5708
    c: PointOnObject(g22,g9)
    c: PointOnObject(g22,g10)
    c: Tangent(g9,g21) = -1.5708
    c: Tangent(g10,g21) = -1.5708
    c: PointOnObject(g24,g9)
    c: PointOnObject(g24,g8)
    c: Tangent(g9,g23) = -1.5708
    c: Tangent(g8,g23) = -1.5708
    c: PointOnObject(g26,g8)
    c: PointOnObject(g26,g7)
    c: Tangent(g8,g25) = -1.5708
    c: Tangent(g7,g25) = -1.5708
    c: Equal(g19,g21)
    c: Equal(g21,g23)
    c: Equal(g23,g25)
    c: DistanceX(g10,g10) = 0.25
    c: Distance(g27) = 29.391
    c: Coincident(g27,g0)
    c: PointOnObject(g27,g-1)
    c: Distance(g28) = 51.19
    c: Coincident(g28,g0)
    c: PointOnObject(g28,g-1)
    c: Distance(g29) = 6.95
    c: Coincident(g29,g27)
    c: Vertical(g29)
    c: Distance(g30) = 6.95
    c: Coincident(g30,g28)
    c: Vertical(g30)
    c: Diameter(g31) = 4.2
    c: Diameter(g32) = 4.2
    c: Coincident(g32,g30)
    c: Coincident(g31,g29)
FEATURE [Sketcher::SketchObject] Sketch031  label="fori inferiori switch pompa"
  ArcFitTolerance = 1e-06
  AttachmentSupport = -> [XY_Plane]
  ExternalGeometry = -> [Sketch]
  FullyConstrained = true
  MakeInternals = false
  MapMode = 5
  sketch-geometry (4):
    g0: LineSegment [constr] StartX=-57.2 StartY=1.9e-15 StartZ=0 EndX=-62.45 EndY=1.9e-15 EndZ=0
    g1: LineSegment [constr] StartX=-62.45 StartY=3.25 StartZ=0 EndX=-62.45 EndY=-3.25 EndZ=0
    g2: Circle CenterX=-62.45 CenterY=3.25 CenterZ=0 NormalX=0 NormalY=0 NormalZ=1 AngleXU=0 Radius=1.6
    g3: Circle CenterX=-62.45 CenterY=-3.25 CenterZ=0 NormalX=0 NormalY=0 NormalZ=1 AngleXU=0 Radius=1.6
  constraints (10):
    c: Distance(g0) = 5.25
    c: Coincident(g0,g-3)
    c: PointOnObject(g0,g-3)
    c: Vertical(g1)
    c: DistanceY(g1,g1) = 6.5
    c: Symmetric(g1,g1,g0)
    c: Diameter(g2) = 3.2
    c: Diameter(g3) = 3.2
    c: Coincident(g2,g1)
    c: Coincident(g3,g1)
FEATURE [Sketcher::SketchObject] Sketch032  label="spazio per PILA 18650"
  ArcFitTolerance = 1e-06
  AttachmentSupport = -> [XY_Plane]
  ExternalGeometry = -> [Sketch]
  FullyConstrained = true
  MakeInternals = false
  MapMode = 5
  sketch-geometry (2):
    g0: LineSegment [constr] StartX=-178.142 StartY=-1.74e-14 StartZ=0 EndX=-190.142 EndY=-1.83e-14 EndZ=0
    g1: Circle CenterX=-190.142 CenterY=-1.83e-14 CenterZ=0 NormalX=0 NormalY=0 NormalZ=1 AngleXU=0 Radius=9.25
  constraints (5):
    c: Distance(g0) = 12
    c: Coincident(g0,g-3)
    c: PointOnObject(g0,g-4)
    c: Diameter(g1) = 18.5
    c: Coincident(g1,g0)
FEATURE [Part::Extrusion] Extrude030  label="Extrude spazio per PILA 18650"
  Base = -> Sketch032
  Dir = (0,0,1)
  DirLink = -> Sketch [Edge45]
  DirMode = 2
  FaceMakerClass = Part::FaceMakerBullseye
  FaceMakerMode = 3
  LengthFwd = 68
  LengthRev = 0
  Placement = pos=(6,0,-72.7) rot=(0,0,1;0rad)
  Solid = true
  Symmetric = false
FEATURE [Sketcher::SketchObject] Sketch033  label="fermo per scheda micro"
  ArcFitTolerance = 1e-06
  AttachmentSupport = -> [XZ_Plane]
  ExternalGeometry = -> [Sketch]
  FullyConstrained = true
  MakeInternals = false
  MapMode = 5
  Placement = pos=(0,0,0) rot=(1,0,0;1.5708rad)
  sketch-geometry (12):
    g0: LineSegment StartX=-11.6 StartY=6 StartZ=0 EndX=-4 EndY=6 EndZ=0
    g1: LineSegment StartX=-4 StartY=6 StartZ=0 EndX=-4 EndY=36.4 EndZ=0
    g2: LineSegment StartX=-4 StartY=36.4 StartZ=0 EndX=-11.6 EndY=36.4 EndZ=0
    g3: LineSegment StartX=-11.6 StartY=36.4 StartZ=0 EndX=-11.6 EndY=6 EndZ=0
    g4: LineSegment StartX=-80.11 StartY=11.6 StartZ=0 EndX=-70.51 EndY=11.6 EndZ=0
    g5: LineSegment StartX=-70.51 StartY=11.6 StartZ=0 EndX=-70.51 EndY=6 EndZ=0
    g6: LineSegment StartX=-70.51 StartY=6 StartZ=0 EndX=-80.11 EndY=6 EndZ=0
    g7: LineSegment StartX=-80.11 StartY=6 StartZ=0 EndX=-80.11 EndY=11.6 EndZ=0
    g8: LineSegment StartX=-78.51 StartY=36.4 StartZ=0 EndX=-70.51 EndY=36.4 EndZ=0
    g9: LineSegment StartX=-70.51 StartY=36.4 StartZ=0 EndX=-70.51 EndY=30.8 EndZ=0
    g10: LineSegment StartX=-70.51 StartY=30.8 StartZ=0 EndX=-78.51 EndY=30.8 EndZ=0
    g11: LineSegment StartX=-78.51 StartY=30.8 StartZ=0 EndX=-78.51 EndY=36.4 EndZ=0
  constraints (33):
    c: Horizontal(g0)
    c: Coincident(g1,g0)
    c: Coincident(g2,g1)
    c: Horizontal(g2)
    c: Coincident(g3,g2)
    c: Coincident(g3,g0)
    c: Vertical(g3)
    c: DistanceX(g2,g2) = 7.6
    c: Coincident(g1,g-3)
    c: Coincident(g0,g-3)
    c: Horizontal(g4)
    c: Coincident(g5,g4)
    c: Vertical(g5)
    c: Coincident(g6,g5)
    c: Horizontal(g6)
    c: Coincident(g7,g6)
    c: Coincident(g7,g4)
    c: Vertical(g7)
    c: DistanceY(g5,g5) = 5.6
    c: DistanceX(g4,g4) = 9.6
    c: Coincident(g9,g8)
    c: Vertical(g9)
    c: Coincident(g10,g9)
    c: Horizontal(g10)
    c: Coincident(g11,g10)
    c: Coincident(g11,g8)
    c: Vertical(g11)
    c: DistanceY(g9,g9) = 5.6
    c: DistanceX(g10,g10) = 8
    c: Coincident(g4,g-4)
    c: DistanceX(g4,g10) = 1.6
    c: Horizontal(g8)
    c: DistanceY(g8,g1) = 0
FEATURE [Sketcher::SketchObject] Sketch034  label="buchi guida rail"
  ArcFitTolerance = 1e-06
  AttachmentSupport = -> [XY_Plane]
  ExternalGeometry = -> [Sketch]
  FullyConstrained = true
  MakeInternals = false
  MapMode = 5
  sketch-geometry (6):
    g0: LineSegment [constr] StartX=-100.8 StartY=9.1e-15 StartZ=0 EndX=-93.3 EndY=0 EndZ=0
    g1: LineSegment [constr] StartX=-93.3 StartY=0 StartZ=0 EndX=-73.3 EndY=0 EndZ=0
    g2: LineSegment [constr] StartX=-73.3 StartY=0 StartZ=0 EndX=-53.3 EndY=0 EndZ=0
    g3: Circle CenterX=-93.3 CenterY=0 CenterZ=0 NormalX=0 NormalY=0 NormalZ=1 AngleXU=0 Radius=2.5
    g4: Circle CenterX=-73.3 CenterY=0 CenterZ=0 NormalX=0 NormalY=0 NormalZ=1 AngleXU=0 Radius=2.5
    g5: Circle CenterX=-53.3 CenterY=0 CenterZ=0 NormalX=0 NormalY=0 NormalZ=1 AngleXU=0 Radius=2.5
  constraints (15):
    c: Distance(g0) = 7.5
    c: Coincident(g0,g-3)
    c: PointOnObject(g0,g-1)
    c: Distance(g1) = 20
    c: Coincident(g1,g0)
    c: PointOnObject(g1,g-1)
    c: Distance(g2) = 20
    c: Coincident(g2,g1)
    c: PointOnObject(g2,g-1)
    c: Diameter(g3) = 5
    c: Diameter(g4) = 5
    c: Diameter(g5) = 5
    c: Coincident(g3,g0)
    c: Coincident(g4,g1)
    c: Coincident(g5,g2)
FEATURE [PartDesign::FeatureBase] BaseFeature
  BaseFeature = -> Extrude017
  Suppressed = false
FEATURE [PartDesign::Body] Body001  label="perno fermo rumble"
  AllowCompound = false
  BaseFeature = -> Extrude017
  Group = -> [BaseFeature,Sketch021]
  Origin = -> Origin001
  Tip = -> BaseFeature
FEATURE [Part::Extrusion] Extrude032  label="Extrude buchi guida rail"
  Base = -> Sketch034
  Dir = (0,0,1)
  DirMode = 2
  FaceMakerClass = Part::FaceMakerBullseye
  FaceMakerMode = 3
  LengthFwd = -6.2
  LengthRev = 0
  Placement = pos=(0,0,43.2) rot=(0,0,1;0rad)
  Solid = true
  Symmetric = false
FEATURE [Part::Extrusion] Extrude033  label="Extrude fori superiori per solenoide e oled001"
  Base = -> Sketch030
  Dir = (0,0,1)
  DirMode = 2
  FaceMakerClass = Part::FaceMakerBullseye
  FaceMakerMode = 3
  LengthFwd = -4.8
  LengthRev = 0
  Placement = pos=(0,0,41.2) rot=(0,0,1;0rad)
  Solid = true
  Symmetric = false
FEATURE [Part::Extrusion] Extrude034  label="Extrude fori sotto impugnatura001"
  Base = -> Sketch029
  Dir = (0,0,1)
  DirMode = 2
  FaceMakerClass = Part::FaceMakerBullseye
  FaceMakerMode = 3
  LengthFwd = 5
  LengthRev = 0
  Placement = pos=(0,0,-83) rot=(0,0,1;0rad)
  Solid = true
  Symmetric = false
FEATURE [Part::Extrusion] Extrude035  label="Extrude fori inferiori switch pompa001"
  Base = -> Sketch031
  Dir = (0,0,1)
  DirMode = 2
  FaceMakerClass = Part::FaceMakerBullseye
  FaceMakerMode = 3
  LengthFwd = 4
  LengthRev = 0
  Placement = pos=(0,0,-1.7) rot=(0,0,1;0rad)
  Solid = true
  Symmetric = false
FEATURE [Part::Extrusion] Extrude036  label="Extrude foro sotto posteriore M3x5x007"
  Base = -> Sketch027
  Dir = (0,0,1)
  DirMode = 2
  FaceMakerClass = Part::FaceMakerBullseye
  FaceMakerMode = 3
  LengthFwd = 6.2
  LengthRev = 0
  Placement = pos=(0,0,-9.6) rot=(0,0,1;0rad)
  Solid = true
  Symmetric = false
FEATURE [Part::Extrusion] Extrude037  label="Extrude foro sotto anteriore M3x5x007"
  Base = -> Sketch026
  Dir = (0,0,1)
  DirMode = 2
  FaceMakerClass = Part::FaceMakerBullseye
  FaceMakerMode = 3
  LengthFwd = 6.2
  LengthRev = 0
  Solid = true
  Symmetric = false
FEATURE [Sketcher::SketchObject] Sketch035  label="foro per fissaggio micro"
  ArcFitTolerance = 1e-06
  AttachmentSupport = -> [XZ_Plane]
  ExternalGeometry = -> [Sketch,Sketch033]
  FullyConstrained = true
  MakeInternals = false
  MapMode = 5
  Placement = pos=(0,0,0) rot=(1,0,0;1.5708rad)
  sketch-geometry (3):
    g0: Circle CenterX=-7.8 CenterY=21.2 CenterZ=0 NormalX=0 NormalY=0 NormalZ=1 AngleXU=0 Radius=1.6
    g1: GeomPoint [constr] X=-4 Y=21.2 Z=0
    g2: LineSegment [constr] StartX=-4 StartY=21.2 StartZ=0 EndX=-11.6 EndY=21.2 EndZ=0
  constraints (6):
    c: Diameter(g0) = 3.2
    c: Symmetric(g-3,g-3,g1)
    c: Coincident(g2,g1)
    c: Horizontal(g2)
    c: DistanceX(g-4,g2) = 0
    c: Symmetric(g2,g1,g0)
FEATURE [Part::Extrusion] Extrude038  label="Extrude foro per fissaggio micro"
  Base = -> Sketch035
  Dir = (0,-1,2e-16)
  DirMode = 2
  FaceMakerClass = Part::FaceMakerBullseye
  FaceMakerMode = 3
  LengthFwd = 3
  LengthRev = 0
  Placement = pos=(0,8.6,0) rot=(0,0,1;0rad)
  Solid = true
  Symmetric = false
FEATURE [Sketcher::SketchObject] Sketch036  label="supporto per alimentatore"
  ArcFitTolerance = 1e-06
  AttachmentSupport = -> [XZ_Plane]
  ExternalGeometry = -> [Sketch,Sketch016,Sketch022]
  FullyConstrained = true
  MakeInternals = false
  MapMode = 5
  Placement = pos=(0,0,0) rot=(1,0,0;1.5708rad)
  sketch-geometry (5):
    g0: LineSegment StartX=-211.843 StartY=-50.0944 StartZ=0 EndX=-211.843 EndY=-80.4316 EndZ=0
    g1: LineSegment StartX=-211.843 StartY=-50.0944 StartZ=0 EndX=-207.775 EndY=-41.3701 EndZ=0
    g2: LineSegment [constr] StartX=-209.443 StartY=-50.0944 StartZ=0 EndX=-209.443 EndY=-80.4316 EndZ=0
    g3: LineSegment StartX=-207.775 StartY=-41.3701 StartZ=0 EndX=-207.775 EndY=-80.4316 EndZ=0
    g4: LineSegment StartX=-211.843 StartY=-80.4316 StartZ=0 EndX=-207.775 EndY=-80.4316 EndZ=0
  constraints (15):
    c: Vertical(g0)
    c: Coincident(g1,g0)
    c: Vertical(g2)
    c: Tangent(g2,g-5)
    c: Coincident(g3,g1)
    c: Vertical(g3)
    c: DistanceY(g-3,g3) = -2
    c: Tangent(g1,g-8)
    c: DistanceY(g-3,g0) = -2
    c: Coincident(g4,g0)
    c: Coincident(g4,g3)
    c: Tangent(g0,g-6)
    c: DistanceY(g-3,g2) = -2
    c: DistanceY(g2,g0) = 0
    c: DistanceX(g-3,g3) = 6.8
FEATURE [Part::Extrusion] Extrude039  label="Extrude039 supporto alimentatore"
  Base = -> Sketch036
  Dir = (0,-1,2e-16)
  DirMode = 2
  FaceMakerClass = Part::FaceMakerBullseye
  FaceMakerMode = 3
  LengthFwd = 25.2
  LengthRev = 0
  Solid = true
  Symmetric = true
FEATURE [Sketcher::SketchObject] Sketch037  label="scavo per alimentatore"
  ArcFitTolerance = 1e-06
  AttachmentSupport = -> [XZ_Plane]
  ExternalGeometry = -> [Sketch036]
  FullyConstrained = true
  MakeInternals = false
  MapMode = 5
  Placement = pos=(0,0,0) rot=(1,0,0;1.5708rad)
  sketch-geometry (4):
    g0: LineSegment StartX=-209.575 StartY=-50.4316 StartZ=0 EndX=-209.575 EndY=-80.4316 EndZ=0
    g1: LineSegment StartX=-209.575 StartY=-50.4316 StartZ=0 EndX=-207.775 EndY=-50.4316 EndZ=0
    g2: LineSegment StartX=-207.775 StartY=-50.4316 StartZ=0 EndX=-207.775 EndY=-80.4316 EndZ=0
    g3: LineSegment StartX=-207.775 StartY=-80.4316 StartZ=0 EndX=-209.575 EndY=-80.4316 EndZ=0
  constraints (11):
    c: Vertical(g0)
    c: Coincident(g1,g0)
    c: Horizontal(g1)
    c: Coincident(g2,g1)
    c: Vertical(g2)
    c: Coincident(g3,g2)
    c: Coincident(g3,g0)
    c: Horizontal(g3)
    c: DistanceX(g1,g1) = 1.8
    c: Coincident(g2,g-3)
    c: DistanceY(g2,g2) = 30
FEATURE [Part::Extrusion] Extrude040  label="Extrude040 scavo alimentatore"
  Base = -> Sketch037
  Dir = (0,-1,2e-16)
  DirMode = 2
  FaceMakerClass = Part::FaceMakerBullseye
  FaceMakerMode = 3
  LengthFwd = 19.5
  LengthRev = 0
  Solid = true
  Symmetric = true
FEATURE [Part::Extrusion] Extrude031  label="Extrude fermo per scheda micro"
  Base = -> Sketch033
  Dir = (0,-1,2e-16)
  DirMode = 2
  FaceMakerClass = Part::FaceMakerBullseye
  FaceMakerMode = 3
  LengthFwd = 3
  LengthRev = 0
  Placement = pos=(0,8.6,0) rot=(0,0,1;0rad)
  Solid = true
  Symmetric = false
FEATURE [Sketcher::SketchObject] Sketch038  label="scavo driver solenoide"
  ArcFitTolerance = 1e-06
  AttachmentSupport = -> [XZ_Plane]
  ExternalGeometry = -> [Sketch,Sketch036]
  FullyConstrained = true
  MakeInternals = false
  MapMode = 5
  Placement = pos=(0,0,0) rot=(1,0,0;1.5708rad)
  sketch-geometry (7):
    g0: LineSegment StartX=-193.66 StartY=-11.0994 StartZ=0 EndX=-195.11 EndY=-10.4232 EndZ=0
    g1: LineSegment StartX=-195.11 StartY=-10.4232 StartZ=0 EndX=-209.225 EndY=-40.6939 EndZ=0
    g2: LineSegment StartX=-193.66 StartY=-11.0994 StartZ=0 EndX=-190.216 EndY=-12.7054 EndZ=0
    g3: LineSegment StartX=-190.216 StartY=-12.7054 StartZ=0 EndX=-204.331 EndY=-42.9761 EndZ=0
    g4: LineSegment StartX=-204.331 StartY=-42.9761 StartZ=0 EndX=-207.775 EndY=-41.3701 EndZ=0
    g5: LineSegment [constr] StartX=-209.225 StartY=-40.6939 StartZ=0 EndX=-207.775 EndY=-41.3701 EndZ=0
    g6: LineSegment StartX=-209.225 StartY=-40.6939 StartZ=0 EndX=-207.775 EndY=-41.3701 EndZ=0
  constraints (19):
    c: Coincident(g1,g0)
    c: Coincident(g3,g2)
    c: Coincident(g4,g3)
    c: Distance(g2) = 3.8
    c: Distance(g1) = 33.4
    c: Coincident(g5,g1)
    c: Distance(g5) = 1.6
    c: Coincident(g-4,g5)
    c: Perpendicular(g5,g-3)
    c: Parallel(g1,g-3)
    c: Perpendicular(g1,g0)
    c: Distance(g0) = 1.6
    c: Coincident(g6,g1)
    c: Coincident(g6,g5)
    c: Parallel(g3,g-3)
    c: Perpendicular(g3,g4)
    c: Perpendicular(g2,g3)
    c: Coincident(g2,g0)
    c: Coincident(g4,g5)
FEATURE [Part::Extrusion] Extrude041  label="Extrude scavo driver solenoide"
  Base = -> Sketch038
  Dir = (0,-1,2e-16)
  DirMode = 2
  FaceMakerClass = Part::FaceMakerBullseye
  FaceMakerMode = 3
  LengthFwd = 17
  LengthRev = 0
  Solid = true
  Symmetric = true
FEATURE [Sketcher::SketchObject] Sketch039  label="scavo per cavo usb per micro"
  ArcFitTolerance = 1e-06
  AttachmentSupport = -> [XZ_Plane]
  ExternalGeometry = -> [Sketch,Sketch016]
  FullyConstrained = true
  MakeInternals = false
  MapMode = 5
  Placement = pos=(0,0,0) rot=(1,0,0;1.5708rad)
  sketch-geometry (4):
    g0: LineSegment StartX=-82.51 StartY=36.4 StartZ=0 EndX=-74.51 EndY=36.4 EndZ=0
    g1: LineSegment StartX=-74.51 StartY=36.4 StartZ=0 EndX=-74.51 EndY=30.8 EndZ=0
    g2: LineSegment StartX=-74.51 StartY=30.8 StartZ=0 EndX=-82.51 EndY=30.8 EndZ=0
    g3: LineSegment StartX=-82.51 StartY=30.8 StartZ=0 EndX=-82.51 EndY=36.4 EndZ=0
  constraints (11):
    c: Coincident(g1,g0)
    c: Vertical(g1)
    c: Coincident(g2,g1)
    c: Horizontal(g2)
    c: Coincident(g3,g2)
    c: Coincident(g3,g0)
    c: Vertical(g3)
    c: Tangent(g0,g-3)
    c: Tangent(g2,g-4)
    c: Tangent(g3,g-4)
    c: Tangent(g1,g-4)
FEATURE [Part::Extrusion] Extrude042  label="Extrude scavo per cavo usb per micro"
  Base = -> Sketch039
  Dir = (0,-1,2e-16)
  DirMode = 2
  FaceMakerClass = Part::FaceMakerBullseye
  FaceMakerMode = 3
  LengthFwd = 11.2
  LengthRev = 0
  Solid = true
  Symmetric = true
FEATURE [Sketcher::SketchObject] Sketch040  label="scavo saldature alimentatore connettore 5v"
  ArcFitTolerance = 1e-06
  AttachmentSupport = -> [XZ_Plane]
  ExternalGeometry = -> [Sketch037]
  FullyConstrained = true
  MakeInternals = false
  MapMode = 5
  Placement = pos=(0,0,0) rot=(1,0,0;1.5708rad)
  sketch-geometry (4):
    g0: LineSegment StartX=-211.175 StartY=-52.4316 StartZ=0 EndX=-211.175 EndY=-56.4316 EndZ=0
    g1: LineSegment StartX=-211.175 StartY=-52.4316 StartZ=0 EndX=-209.575 EndY=-52.4316 EndZ=0
    g2: LineSegment StartX=-209.575 StartY=-52.4316 StartZ=0 EndX=-209.575 EndY=-56.4316 EndZ=0
    g3: LineSegment StartX=-209.575 StartY=-56.4316 StartZ=0 EndX=-211.175 EndY=-56.4316 EndZ=0
  constraints (11):
    c: Vertical(g0)
    c: Coincident(g1,g0)
    c: Horizontal(g1)
    c: Coincident(g2,g1)
    c: Coincident(g3,g2)
    c: Coincident(g3,g0)
    c: Horizontal(g3)
    c: DistanceX(g1,g1) = 1.6
    c: DistanceY(g2,g2) = 4
    c: Tangent(g2,g-3)
    c: DistanceY(g1,g-3) = 2
FEATURE [Part::Extrusion] Extrude043  label="Extrude scavo saldature alimentatore connettore 5v"
  Base = -> Sketch040
  Dir = (0,-1,2e-16)
  DirMode = 2
  FaceMakerClass = Part::FaceMakerBullseye
  FaceMakerMode = 3
  LengthFwd = 8
  LengthRev = 0
  Solid = true
  Symmetric = true
FEATURE [Sketcher::SketchObject] Sketch041  label="scavo saldature alimentatore connettore 5v verticali"
  ArcFitTolerance = 1e-06
  AttachmentSupport = -> [XZ_Plane]
  ExternalGeometry = -> [Sketch037]
  FullyConstrained = true
  MakeInternals = false
  MapMode = 5
  Placement = pos=(0,0,0) rot=(1,0,0;1.5708rad)
  sketch-geometry (4):
    g0: LineSegment StartX=-211.175 StartY=-53.6316 StartZ=0 EndX=-209.575 EndY=-53.6316 EndZ=0
    g1: LineSegment StartX=-209.575 StartY=-53.6316 StartZ=0 EndX=-209.575 EndY=-76.6316 EndZ=0
    g2: LineSegment StartX=-209.575 StartY=-76.6316 StartZ=0 EndX=-211.175 EndY=-76.6316 EndZ=0
    g3: LineSegment StartX=-211.175 StartY=-76.6316 StartZ=0 EndX=-211.175 EndY=-53.6316 EndZ=0
  constraints (11):
    c: Horizontal(g0)
    c: Coincident(g1,g0)
    c: Coincident(g2,g1)
    c: Horizontal(g2)
    c: Coincident(g3,g2)
    c: Coincident(g3,g0)
    c: Vertical(g3)
    c: DistanceY(g3,g3) = 23
    c: DistanceX(g0,g0) = 1.6
    c: Tangent(g1,g-3)
    c: DistanceY(g0,g-3) = 3.2
FEATURE [Part::Extrusion] Extrude044  label="Extrude scavo saldature alimentatore connettore 5v verticali"
  Base = -> Sketch041
  Dir = (0,-1,2e-16)
  DirMode = 2
  FaceMakerClass = Part::FaceMakerBullseye
  FaceMakerMode = 3
  LengthFwd = 3.2
  LengthRev = 0
  Placement = pos=(0,8.3,0) rot=(0,0,1;0rad)
  Solid = true
  Symmetric = false
FEATURE [Sketcher::SketchObject] Sketch042  label="fermi per driver solenoide e alimentatore"
  ArcFitTolerance = 1e-06
  AttachmentSupport = -> [XZ_Plane]
  ExternalGeometry = -> [Sketch036,Sketch037,Sketch,Sketch038]
  FullyConstrained = true
  MakeInternals = false
  MapMode = 5
  Placement = pos=(0,0,0) rot=(1,0,0;1.5708rad)
  sketch-geometry (27):
    g0: LineSegment StartX=-195.773 StartY=-15.631 StartZ=0 EndX=-196.702 EndY=-17.6249 EndZ=0
    g1: LineSegment StartX=-196.702 StartY=-17.6249 StartZ=0 EndX=-194.709 EndY=-18.5546 EndZ=0
    g2: LineSegment StartX=-194.709 StartY=-18.5546 StartZ=0 EndX=-193.779 EndY=-16.5607 EndZ=0
    g3: LineSegment StartX=-193.779 StartY=-16.5607 StartZ=0 EndX=-195.773 EndY=-15.631 EndZ=0
    g4: LineSegment StartX=-196.547 StartY=-13.5047 StartZ=0 EndX=-198.829 EndY=-18.3988 EndZ=0
    g5: LineSegment StartX=-198.829 StartY=-18.3988 StartZ=0 EndX=-195.385 EndY=-20.0047 EndZ=0
    g6: LineSegment StartX=-193.258 StartY=-19.2308 StartZ=0 EndX=-192.329 EndY=-17.2369 EndZ=0
    g7: LineSegment StartX=-193.103 StartY=-15.1106 StartZ=0 EndX=-196.547 EndY=-13.5047 EndZ=0
    g8: LineSegment [constr] StartX=-193.935 StartY=-20.6809 StartZ=0 EndX=-193.258 EndY=-19.2308 EndZ=0
    g9: LineSegment [constr] StartX=-193.935 StartY=-20.6809 StartZ=0 EndX=-195.385 EndY=-20.0047 EndZ=0
    g10: ArcOfCircle CenterX=-193.779 CenterY=-16.5607 CenterZ=0 NormalX=0 NormalY=0 NormalZ=1 AngleXU=0 Radius=1.6 StartAngle=5.84685 EndAngle=7.41765
    g11: GeomPoint [constr] X=-191.653 Y=-15.7868 Z=0
    g12: ArcOfCircle CenterX=-194.709 CenterY=-18.5546 CenterZ=0 NormalX=0 NormalY=0 NormalZ=1 AngleXU=0 Radius=1.6 StartAngle=4.27606 EndAngle=5.84685
    g13: GeomPoint [constr] X=-193.935 Y=-20.6809 Z=0
    g14: LineSegment StartX=-207.775 StartY=-46.8316 StartZ=0 EndX=-207.775 EndY=-50.8316 EndZ=0
    g15: LineSegment StartX=-207.775 StartY=-46.8316 StartZ=0 EndX=-203.775 EndY=-46.8316 EndZ=0
    g16: LineSegment StartX=-203.775 StartY=-46.8316 StartZ=0 EndX=-203.775 EndY=-50.8316 EndZ=0
    g17: LineSegment StartX=-207.775 StartY=-50.8316 StartZ=0 EndX=-203.775 EndY=-50.8316 EndZ=0
    g18: LineSegment StartX=-209.375 StartY=-52.4316 StartZ=0 EndX=-203.775 EndY=-52.4316 EndZ=0
    g19: LineSegment StartX=-202.175 StartY=-50.8316 StartZ=0 EndX=-202.175 EndY=-46.8316 EndZ=0
    g20: LineSegment StartX=-203.775 StartY=-45.2316 StartZ=0 EndX=-209.375 EndY=-45.2316 EndZ=0
    g21: LineSegment StartX=-209.375 StartY=-45.2316 StartZ=0 EndX=-209.375 EndY=-52.4316 EndZ=0
    g22: ArcOfCircle CenterX=-203.775 CenterY=-46.8316 CenterZ=0 NormalX=0 NormalY=0 NormalZ=1 AngleXU=0 Radius=1.6 StartAngle=1.8e-15 EndAngle=1.5708
    g23: GeomPoint [constr] X=-202.175 Y=-45.2316 Z=0
    g24: ArcOfCircle CenterX=-203.775 CenterY=-50.8316 CenterZ=0 NormalX=0 NormalY=0 NormalZ=1 AngleXU=0 Radius=1.6 StartAngle=4.71239 EndAngle=6.28319
    g25: GeomPoint [constr] X=-202.175 Y=-52.4316 Z=0
    g26: LineSegment [constr] StartX=-207.775 StartY=-50.4316 StartZ=0 EndX=-207.775 EndY=-50.8316 EndZ=0
  constraints (69):
    c: Coincident(g1,g0)
    c: Coincident(g2,g1)
    c: Coincident(g3,g2)
    c: Coincident(g3,g0)
    c: Parallel(g0,g2)
    c: Perpendicular(g3,g0)
    c: Perpendicular(g1,g0)
    c: Coincident(g5,g4)
    c: Coincident(g7,g4)
    c: Distance(g3) = 2.2
    c: Distance(g2) = 2.2
    c: Parallel(g6,g2)
    c: Parallel(g6,g4)
    c: Perpendicular(g5,g6)
    c: Perpendicular(g7,g6)
    c: Distance(g13,g11) = 5.4
    c: Distance(g5,g13) = 5.4
    c: Coincident(g9,g8)
    c: Distance(g8) = 1.6
    c: Distance(g9) = 1.6
    c: Perpendicular(g9,g8)
    c: Parallel(g8,g6)
    c: Coincident(g8,g13)
    c: Distance(g8,g1) = 1.6
    c: Distance(g9,g1) = 1.6
    c: Tangent(g0,g-5)
    c: Distance(g0,g-6) = 26.2
    c: PointOnObject(g11,g7)
    c: PointOnObject(g11,g6)
    c: Tangent(g7,g10) = -1.5708
    c: Tangent(g6,g10) = -1.5708
    c: PointOnObject(g13,g5)
    c: Tangent(g5,g12) = -1.5708
    c: Tangent(g6,g12) = -1.5708
    c: Equal(g10,g12)
    c: Coincident(g10,g2)
    c: Vertical(g14)
    c: Coincident(g15,g14)
    c: Horizontal(g15)
    c: Coincident(g16,g15)
    c: Vertical(g16)
    c: Coincident(g17,g14)
    c: Coincident(g17,g16)
    c: Horizontal(g17)
    c: Distance(g16) = 4
    c: Distance(g15) = 4
    c: Horizontal(g18)
    c: Vertical(g19)
    c: Horizontal(g20)
    c: Coincident(g21,g20)
    c: Coincident(g21,g18)
    c: Vertical(g21)
    c: Distance(g20,g23) = 7.2
    c: Distance(g25,g23) = 7.2
    c: DistanceY(g18,g14) = 1.6
    c: DistanceX(g18,g14) = 1.6
    c: PointOnObject(g23,g20)
    c: PointOnObject(g23,g19)
    c: Tangent(g20,g22) = -1.5708
    c: Tangent(g19,g22) = -1.5708
    c: PointOnObject(g25,g19)
    c: Tangent(g18,g24) = -1.5708
    c: Tangent(g19,g24) = -1.5708
    c: Equal(g22,g24)
    c: Coincident(g22,g15)
    c: Vertical(g26)
    c: Distance(g26) = 0.4
    c: Coincident(g26,g-4)
    c: Coincident(g14,g26)
FEATURE [Part::Extrusion] Extrude045  label="Extrude fermi per driver solenoide e alimentatore"
  Base = -> Sketch042
  Dir = (0,-1,2e-16)
  DirMode = 2
  FaceMakerClass = Part::FaceMakerBullseye
  FaceMakerMode = 3
  LengthFwd = 25.2
  LengthRev = 0
  Solid = true
  Symmetric = true
FEATURE [Sketcher::SketchObject] Sketch043  label="scavo pulizia fermo alimentatore"
  ArcFitTolerance = 1e-06
  AttachmentSupport = -> [XZ_Plane]
  ExternalGeometry = -> [Sketch042,Sketch036,Sketch037]
  FullyConstrained = true
  MakeInternals = false
  MapMode = 5
  Placement = pos=(0,0,0) rot=(1,0,0;1.5708rad)
  sketch-geometry (6):
    g0: LineSegment StartX=-209.375 StartY=-52.4316 StartZ=0 EndX=-209.375 EndY=-50.4316 EndZ=0
    g1: LineSegment StartX=-209.375 StartY=-50.4316 StartZ=0 EndX=-207.775 EndY=-50.4316 EndZ=0
    g2: LineSegment StartX=-207.775 StartY=-50.4316 StartZ=0 EndX=-207.775 EndY=-45.2316 EndZ=0
    g3: LineSegment StartX=-207.775 StartY=-45.2316 StartZ=0 EndX=-202.175 EndY=-45.2316 EndZ=0
    g4: LineSegment StartX=-202.175 StartY=-45.2316 StartZ=0 EndX=-202.175 EndY=-52.4316 EndZ=0
    g5: LineSegment StartX=-202.175 StartY=-52.4316 StartZ=0 EndX=-209.375 EndY=-52.4316 EndZ=0
  constraints (13):
    c: Vertical(g0)
    c: Coincident(g1,g0)
    c: Coincident(g2,g1)
    c: Coincident(g3,g2)
    c: Coincident(g4,g3)
    c: Coincident(g5,g4)
    c: Coincident(g5,g0)
    c: Horizontal(g5)
    c: Coincident(g0,g-6)
    c: Tangent(g1,g-8)
    c: Tangent(g2,g-4)
    c: Tangent(g3,g-7)
    c: Tangent(g4,g-3)
FEATURE [Part::Extrusion] Extrude046  label="Extrude scavo pulizia fermo alimentatore"
  Base = -> Sketch043
  Dir = (0,-1,2e-16)
  DirMode = 2
  FaceMakerClass = Part::FaceMakerBullseye
  FaceMakerMode = 3
  LengthFwd = 19.5
  LengthRev = 0
  Solid = true
  Symmetric = true
FEATURE [Sketcher::SketchObject] Sketch044  label="buchini per fissaggio oled"
  ArcFitTolerance = 1e-06
  AttachmentSupport = -> [YZ_Plane]
  ExternalGeometry = -> [Sketch]
  FullyConstrained = true
  MakeInternals = false
  MapMode = 5
  Placement = pos=(0,0,0) rot=(0.57735,0.57735,0.57735;2.0944rad)
  sketch-geometry (5):
    g0: LineSegment [constr] StartX=1.5e-14 StartY=67.3588 StartZ=0 EndX=0 EndY=64.3588 EndZ=0
    g1: LineSegment [constr] StartX=0 StartY=64.3588 StartZ=0 EndX=10.4 EndY=64.3588 EndZ=0
    g2: LineSegment [constr] StartX=0 StartY=64.3588 StartZ=0 EndX=-10.4 EndY=64.3588 EndZ=0
    g3: Circle CenterX=10.4 CenterY=64.3588 CenterZ=0 NormalX=0 NormalY=0 NormalZ=1 AngleXU=0 Radius=1.5
    g4: Circle CenterX=-10.4 CenterY=64.3588 CenterZ=0 NormalX=0 NormalY=0 NormalZ=1 AngleXU=0 Radius=1.5
  constraints (13):
    c: Distance(g0) = 3
    c: PointOnObject(g0,g-2)
    c: Coincident(g1,g0)
    c: Horizontal(g1)
    c: Coincident(g2,g0)
    c: Horizontal(g2)
    c: DistanceX(g1,g1) = 10.4
    c: Coincident(g3,g1)
    c: Diameter(g4) = 3
    c: Coincident(g4,g2)
    c: Coincident(g0,g-7)
    c: Equal(g1,g2)
    c: Equal(g4,g3)
FEATURE [Part::Extrusion] Extrude047  label="Extrude buchini per fissaggio oled"
  Base = -> Sketch044
  Dir = (1,0,0)
  DirMode = 2
  FaceMakerClass = Part::FaceMakerBullseye
  FaceMakerMode = 3
  LengthFwd = 10
  LengthRev = 0
  Placement = pos=(-186,0,0) rot=(0,0,1;0rad)
  Solid = true
  Symmetric = false
FEATURE [Sketcher::SketchObject] Sketch046  label="scavo 5x5 neopixel"
  ArcFitTolerance = 1e-06
  AttachmentSupport = -> [YZ_Plane002]
  FullyConstrained = true
  MakeInternals = false
  MapMode = 5
  Placement = pos=(0,0,0) rot=(0.57735,0.57735,0.57735;2.0944rad)
  sketch-geometry (4):
    g0: LineSegment StartX=-2.7 StartY=2.7 StartZ=0 EndX=2.7 EndY=2.7 EndZ=0
    g1: LineSegment StartX=2.7 StartY=2.7 StartZ=0 EndX=2.7 EndY=-2.7 EndZ=0
    g2: LineSegment StartX=2.7 StartY=-2.7 StartZ=0 EndX=-2.7 EndY=-2.7 EndZ=0
    g3: LineSegment StartX=-2.7 StartY=-2.7 StartZ=0 EndX=-2.7 EndY=2.7 EndZ=0
  constraints (11):
    c: Horizontal(g0)
    c: Coincident(g1,g0)
    c: Vertical(g1)
    c: Coincident(g2,g1)
    c: Horizontal(g2)
    c: Coincident(g3,g2)
    c: Coincident(g3,g0)
    c: Vertical(g3)
    c: DistanceX(g0,g0) = 5.4
    c: DistanceY(g1,g1) = 5.4
    c: Symmetric(g0,g1,g-1)
FEATURE [Part::Extrusion] Extrude049  label="Extrude scavo 5x5 neopixel"
  Base = -> Sketch046
  Dir = (1,0,0)
  DirMode = 2
  FaceMakerClass = Part::FaceMakerBullseye
  FaceMakerMode = 3
  LengthFwd = 1
  LengthRev = 0
  Solid = true
  Symmetric = false
FEATURE [Sketcher::SketchObject] Sketch047  label="scavo 10x10 neopixel corpo"
  ArcFitTolerance = 1e-06
  AttachmentSupport = -> [YZ_Plane002]
  FullyConstrained = true
  MakeInternals = false
  MapMode = 5
  Placement = pos=(0,0,0) rot=(0.57735,0.57735,0.57735;2.0944rad)
  sketch-geometry (4):
    g0: LineSegment StartX=-5 StartY=5.1 StartZ=0 EndX=5 EndY=5.1 EndZ=0
    g1: LineSegment StartX=5 StartY=5.1 StartZ=0 EndX=5 EndY=-5.1 EndZ=0
    g2: LineSegment StartX=5 StartY=-5.1 StartZ=0 EndX=-5 EndY=-5.1 EndZ=0
    g3: LineSegment StartX=-5 StartY=-5.1 StartZ=0 EndX=-5 EndY=5.1 EndZ=0
  constraints (11):
    c: Horizontal(g0)
    c: Coincident(g1,g0)
    c: Vertical(g1)
    c: Coincident(g2,g1)
    c: Horizontal(g2)
    c: Coincident(g3,g2)
    c: Coincident(g3,g0)
    c: Vertical(g3)
    c: DistanceX(g0,g0) = 10
    c: DistanceY(g1,g1) = 10.2
    c: Symmetric(g0,g2,g-1)
FEATURE [Part::Extrusion] Extrude050  label="Extrude scavo 10x10 neopixel corpo"
  Base = -> Sketch047
  Dir = (1,0,0)
  DirMode = 2
  FaceMakerClass = Part::FaceMakerBullseye
  FaceMakerMode = 3
  LengthFwd = 8
  LengthRev = 0
  Placement = pos=(1,0,0) rot=(0,0,1;0rad)
  Solid = true
  Symmetric = false
FEATURE [Sketcher::SketchObject] Sketch048  label="buco per perno blocco neopixel"
  ArcFitTolerance = 1e-06
  AttachmentSupport = -> [XZ_Plane002]
  FullyConstrained = true
  MakeInternals = false
  MapMode = 5
  Placement = pos=(0,0,0) rot=(1,0,0;1.5708rad)
  sketch-geometry (4):
    g0: LineSegment StartX=3 StartY=1.2 StartZ=0 EndX=3 EndY=-1.2 EndZ=0
    g1: LineSegment StartX=3 StartY=-1.2 StartZ=0 EndX=5.4 EndY=-1.2 EndZ=0
    g2: LineSegment StartX=5.4 StartY=-1.2 StartZ=0 EndX=5.4 EndY=1.2 EndZ=0
    g3: LineSegment StartX=5.4 StartY=1.2 StartZ=0 EndX=3 EndY=1.2 EndZ=0
  constraints (11):
    c: Coincident(g1,g0)
    c: Horizontal(g1)
    c: Coincident(g2,g1)
    c: Vertical(g2)
    c: Coincident(g3,g2)
    c: Coincident(g3,g0)
    c: Horizontal(g3)
    c: DistanceX(g1,g1) = 2.4
    c: DistanceY(g2,g2) = 2.4
    c: Symmetric(g0,g0,g-1)
    c: DistanceX(g-1,g0) = 3
FEATURE [Sketcher::SketchObject] Sketch045  label="blocco principale per neopixel"
  ArcFitTolerance = 1e-06
  AttachmentSupport = -> [XZ_Plane002]
  ExternalGeometry = -> [Sketch048]
  FullyConstrained = true
  MakeInternals = false
  MapMode = 5
  Placement = pos=(0,0,0) rot=(1,0,0;1.5708rad)
  sketch-geometry (6):
    g0: LineSegment StartX=0 StartY=5.1 StartZ=0 EndX=0 EndY=-5.1 EndZ=0
    g1: LineSegment StartX=0 StartY=-5.1 StartZ=0 EndX=3 EndY=-5.1 EndZ=0
    g2: LineSegment StartX=7 StartY=-1.1 StartZ=0 EndX=7 EndY=5.1 EndZ=0
    g3: LineSegment StartX=7 StartY=5.1 StartZ=0 EndX=0 EndY=5.1 EndZ=0
    g4: ArcOfCircle CenterX=3 CenterY=-1.1 CenterZ=0 NormalX=0 NormalY=0 NormalZ=1 AngleXU=0 Radius=4 StartAngle=4.71239 EndAngle=6.28319
    g5: GeomPoint [constr] X=7 Y=-5.1 Z=0
  constraints (15):
    c: Vertical(g0)
    c: Coincident(g1,g0)
    c: Horizontal(g1)
    c: Vertical(g2)
    c: Coincident(g3,g2)
    c: Coincident(g3,g0)
    c: Horizontal(g3)
    c: DistanceY(g0,g0) = 10.2
    c: Symmetric(g0,g0,g-1)
    c: DistanceX(g3,g3) = 7
    c: PointOnObject(g5,g2)
    c: PointOnObject(g5,g1)
    c: Tangent(g2,g4) = -1.5708
    c: Tangent(g1,g4) = -1.5708
    c: DistanceX(g-3,g1) = 0
FEATURE [Part::Extrusion] Extrude048  label="Extrude blocco principale per neopixel"
  Base = -> Sketch045
  Dir = (0,-1,2e-16)
  DirMode = 2
  FaceMakerClass = Part::FaceMakerBullseye
  FaceMakerMode = 3
  LengthFwd = 17
  LengthRev = 0
  Solid = true
  Symmetric = true
FEATURE [Part::Extrusion] Extrude051  label="Extrude buco per perno blocco neopixel"
  Base = -> Sketch048
  Dir = (0,-1,2e-16)
  DirMode = 2
  FaceMakerClass = Part::FaceMakerBullseye
  FaceMakerMode = 3
  LengthFwd = 17
  LengthRev = 0
  Solid = true
  Symmetric = true
FEATURE [Sketcher::SketchObject] Sketch049  label="rinforzi esterni per corpo neopoixel"
  ArcFitTolerance = 1e-06
  AttachmentSupport = -> [XZ_Plane002]
  ExternalGeometry = -> [Sketch045]
  FullyConstrained = true
  MakeInternals = false
  MapMode = 5
  Placement = pos=(0,0,0) rot=(1,0,0;1.5708rad)
  sketch-geometry (8):
    g0: LineSegment StartX=1 StartY=-4.1 StartZ=0 EndX=2 EndY=-4.1 EndZ=0
    g1: LineSegment StartX=2 StartY=-4.1 StartZ=0 EndX=2 EndY=-5.1 EndZ=0
    g2: LineSegment StartX=2 StartY=-5.1 StartZ=0 EndX=1 EndY=-5.1 EndZ=0
    g3: LineSegment StartX=1 StartY=-5.1 StartZ=0 EndX=1 EndY=-4.1 EndZ=0
    g4: LineSegment StartX=1 StartY=5.1 StartZ=0 EndX=2 EndY=5.1 EndZ=0
    g5: LineSegment StartX=2 StartY=5.1 StartZ=0 EndX=2 EndY=4.1 EndZ=0
    g6: LineSegment StartX=2 StartY=4.1 StartZ=0 EndX=1 EndY=4.1 EndZ=0
    g7: LineSegment StartX=1 StartY=4.1 StartZ=0 EndX=1 EndY=5.1 EndZ=0
  constraints (24):
    c: Horizontal(g0)
    c: Coincident(g1,g0)
    c: Vertical(g1)
    c: Coincident(g2,g1)
    c: Horizontal(g2)
    c: Coincident(g3,g2)
    c: Coincident(g3,g0)
    c: Vertical(g3)
    c: Horizontal(g4)
    c: Coincident(g5,g4)
    c: Vertical(g5)
    c: Coincident(g6,g5)
    c: Horizontal(g6)
    c: Coincident(g7,g6)
    c: Coincident(g7,g4)
    c: Vertical(g7)
    c: DistanceX(g4,g4) = 1
    c: DistanceY(g5,g5) = 1
    c: DistanceX(g0,g0) = 1
    c: DistanceY(g1,g1) = 1
    c: DistanceX(g-3,g4) = 1
    c: DistanceY(g-3,g4) = 0
    c: DistanceX(g-4,g2) = 1
    c: DistanceY(g2,g-4) = 0
FEATURE [Part::Extrusion] Extrude052  label="Extrude rinforzi esterni per corpo neopoixel"
  Base = -> Sketch049
  Dir = (0,-1,2e-16)
  DirMode = 2
  FaceMakerClass = Part::FaceMakerBullseye
  FaceMakerMode = 3
  LengthFwd = 17
  LengthRev = 0
  Solid = true
  Symmetric = true
FEATURE [Part::Cut] Cut030
  Base = -> Extrude048
  Refine = true
  Tool = -> Extrude050
FEATURE [Part::Cut] Cut031
  Base = -> Cut030
  Refine = true
  Tool = -> Extrude049
FEATURE [Part::Cut] Cut032
  Base = -> Cut031
  Refine = true
  Tool = -> Extrude051
FEATURE [Part::MultiFuse] Fusion001  label="fusion neopixel"
  Refine = true
  Shapes = -> [Cut032,Extrude052]
FEATURE [Sketcher::SketchObject] Sketch052  label="scavo saldature driver solenoide"
  ArcFitTolerance = 1e-06
  AttachmentSupport = -> [XZ_Plane]
  ExternalGeometry = -> [Sketch038]
  FullyConstrained = true
  MakeInternals = false
  MapMode = 5
  Placement = pos=(0,0,0) rot=(1,0,0;1.5708rad)
  sketch-geometry (4):
    g0: LineSegment StartX=-196.56 StartY=-9.74706 StartZ=0 EndX=-198.25 EndY=-13.3723 EndZ=0
    g1: LineSegment StartX=-198.25 StartY=-13.3723 StartZ=0 EndX=-196.8 EndY=-14.0485 EndZ=0
    g2: LineSegment StartX=-196.8 StartY=-14.0485 StartZ=0 EndX=-195.11 EndY=-10.4232 EndZ=0
    g3: LineSegment StartX=-195.11 StartY=-10.4232 StartZ=0 EndX=-196.56 EndY=-9.74706 EndZ=0
  constraints (11):
    c: Coincident(g1,g0)
    c: Coincident(g2,g1)
    c: Coincident(g3,g2)
    c: Coincident(g3,g0)
    c: Parallel(g2,g0)
    c: Perpendicular(g2,g3)
    c: Perpendicular(g1,g2,g1) = 1.5708
    c: Parallel(g2,g-3)
    c: Distance(g2) = 4
    c: Distance(g3) = 1.6
    c: Coincident(g2,g-3)
FEATURE [Part::Extrusion] Extrude055  label="Extrude scavo saldature driver solenoide"
  Base = -> Sketch052
  Dir = (0,-1,2e-16)
  DirMode = 2
  FaceMakerClass = Part::FaceMakerBullseye
  FaceMakerMode = 3
  LengthFwd = 6
  LengthRev = 0
  Solid = true
  Symmetric = true
FEATURE [Sketcher::SketchObject] Sketch053  label="scavo saldature rumble"
  ArcFitTolerance = 1e-06
  AttachmentSupport = -> [XZ_Plane]
  ExternalGeometry = -> [Sketch019]
  FullyConstrained = true
  MakeInternals = false
  MapMode = 5
  Placement = pos=(0,0,0) rot=(1,0,0;1.5708rad)
  sketch-geometry (4):
    g0: LineSegment StartX=-165.31 StartY=-44.1173 StartZ=0 EndX=-166.547 EndY=-47.9216 EndZ=0
    g1: LineSegment StartX=-166.547 StartY=-47.9216 StartZ=0 EndX=-165.405 EndY=-48.2924 EndZ=0
    g2: LineSegment StartX=-165.405 StartY=-48.2924 StartZ=0 EndX=-164.169 EndY=-44.4881 EndZ=0
    g3: LineSegment StartX=-164.169 StartY=-44.4881 StartZ=0 EndX=-165.31 EndY=-44.1173 EndZ=0
  constraints (11):
    c: Coincident(g1,g0)
    c: Coincident(g2,g1)
    c: Coincident(g3,g2)
    c: Coincident(g3,g0)
    c: Parallel(g0,g2)
    c: Perpendicular(g3,g0)
    c: Perpendicular(g1,g0)
    c: Parallel(g0,g-3)
    c: Distance(g0) = 4
    c: Distance(g1) = 1.2
    c: Coincident(g0,g-3)
FEATURE [Part::Extrusion] Extrude056  label="Extrude scavo saldature rumble"
  Base = -> Sketch053
  Dir = (0,-1,2e-16)
  DirMode = 2
  FaceMakerClass = Part::FaceMakerBullseye
  FaceMakerMode = 3
  LengthFwd = 8.4
  LengthRev = 0
  Solid = true
  Symmetric = true
FEATURE [Part::Cone] Cone  label="Cono"
  Angle = 180
  AttacherType = Attacher::AttachEngine3D
  Height = 15
  Placement = pos=(-176,0,-82.43) rot=(0,0,1;-1.5708rad)
  Radius1 = 12.6
  Radius2 = 10.5
FEATURE [Sketcher::SketchObject] Sketch054  label="scavo saldature alimentatore connettore USB"
  ArcFitTolerance = 1e-06
  AttachmentSupport = -> [XZ_Plane]
  ExternalGeometry = -> [Sketch037]
  FullyConstrained = true
  MakeInternals = false
  MapMode = 5
  Placement = pos=(0,0,0) rot=(1,0,0;1.5708rad)
  sketch-geometry (4):
    g0: LineSegment StartX=-209.575 StartY=-80.4316 StartZ=0 EndX=-210.375 EndY=-80.4316 EndZ=0
    g1: LineSegment StartX=-210.375 StartY=-80.4316 StartZ=0 EndX=-210.375 EndY=-72.4316 EndZ=0
    g2: LineSegment StartX=-210.375 StartY=-72.4316 StartZ=0 EndX=-209.575 EndY=-72.4316 EndZ=0
    g3: LineSegment StartX=-209.575 StartY=-72.4316 StartZ=0 EndX=-209.575 EndY=-80.4316 EndZ=0
  constraints (11):
    c: Horizontal(g0)
    c: Coincident(g1,g0)
    c: Vertical(g1)
    c: Coincident(g2,g1)
    c: Horizontal(g2)
    c: Coincident(g3,g2)
    c: Coincident(g3,g0)
    c: Vertical(g3)
    c: DistanceX(g0,g0) = 0.8
    c: DistanceY(g3,g3) = 8
    c: Coincident(g0,g-4)
FEATURE [Part::Extrusion] Extrude057  label="Extrude scavo saldature alimentatore connettore USB"
  Base = -> Sketch054
  Dir = (0,-1,2e-16)
  DirMode = 2
  FaceMakerClass = Part::FaceMakerBullseye
  FaceMakerMode = 3
  LengthFwd = 11
  LengthRev = 0
  Solid = true
  Symmetric = true
FEATURE [Sketcher::SketchObject] Sketch055  label="buco interno per micro switch"
  ArcFitTolerance = 1e-06
  AttachmentSupport = -> [XZ_Plane]
  ExternalGeometry = -> [Sketch]
  FullyConstrained = true
  MakeInternals = false
  MapMode = 5
  Placement = pos=(0,0,0) rot=(1,0,0;1.5708rad)
  sketch-geometry (11):
    g0: LineSegment [constr] StartX=-194.483 StartY=34.2854 StartZ=0 EndX=-196.022 EndY=30.0568 EndZ=0
    g1: LineSegment [constr] StartX=-196.022 StartY=30.0568 StartZ=0 EndX=-197.561 EndY=25.8282 EndZ=0
    g2: LineSegment [constr] StartX=-196.022 StartY=30.0568 StartZ=0 EndX=-194.143 EndY=29.3727 EndZ=0
    g3: LineSegment [constr] StartX=-196.022 StartY=30.0568 StartZ=0 EndX=-197.902 EndY=30.7408 EndZ=0
    g4: LineSegment StartX=-196.362 StartY=34.9694 StartZ=0 EndX=-192.604 EndY=33.6014 EndZ=0
    g5: LineSegment StartX=-199.441 StartY=26.5122 StartZ=0 EndX=-195.682 EndY=25.1441 EndZ=0
    g6: LineSegment StartX=-192.604 StartY=33.6014 StartZ=0 EndX=-195.682 EndY=25.1441 EndZ=0
    g7: LineSegment StartX=-196.362 StartY=34.9694 StartZ=0 EndX=-199.441 EndY=26.5122 EndZ=0
    g8: GeomPoint [constr] X=-187.821 Y=29.2 Z=0
    g9: LineSegment [constr] StartX=-188.505 StartY=27.3206 StartZ=0 EndX=-196.022 EndY=30.0568 EndZ=0
    g10: LineSegment [constr] StartX=-187.821 StartY=29.2 StartZ=0 EndX=-188.505 EndY=27.3206 EndZ=0
  constraints (27):
    c: Coincident(g2,g0)
    c: Parallel(g0,g-3)
    c: Tangent(g1,g0) = -1.5708
    c: Perpendicular(g0,g2)
    c: Tangent(g2,g3)
    c: Distance(g0,g1) = 9
    c: Equal(g0,g1)
    c: Distance(g3,g2) = 4
    c: Equal(g2,g3)
    c: Parallel(g3,g4)
    c: Symmetric(g4,g4,g0)
    c: Parallel(g6,g1)
    c: Parallel(g7,g1)
    c: Symmetric(g6,g6,g2)
    c: Symmetric(g5,g5,g1)
    c: Symmetric(g7,g7,g3)
    c: Coincident(g7,g4)
    c: Coincident(g6,g4)
    c: Coincident(g5,g6)
    c: Symmetric(g-3,g-3,g8)
    c: Perpendicular(g-3,g9)
    c: Distance(g9) = 8
    c: Coincident(g3,g9)
    c: Coincident(g10,g8)
    c: Parallel(g10,g-3)
    c: Distance(g10) = 2
    c: Coincident(g10,g9)
FEATURE [Part::Extrusion] Extrude058  label="Extrude buco interno per micro switch sinistro"
  Base = -> Sketch055
  Dir = (0,-1,2e-16)
  DirMode = 2
  FaceMakerClass = Part::FaceMakerBullseye
  FaceMakerMode = 3
  LengthFwd = 9
  LengthRev = 0
  Placement = pos=(0,10.6,0) rot=(0,0,1;0rad)
  Solid = true
  Symmetric = false
FEATURE [Sketcher::SketchObject] Sketch056  label="buco esterno per micro switch"
  ArcFitTolerance = 1e-06
  AttachmentSupport = -> [XZ_Plane]
  ExternalGeometry = -> [Sketch055]
  FullyConstrained = true
  MakeInternals = false
  MapMode = 5
  Placement = pos=(0,0,0) rot=(1,0,0;1.5708rad)
  sketch-geometry (17):
    g0: GeomPoint [constr] X=-194.143 Y=29.3727 Z=0
    g1: GeomPoint [constr] X=-194.483 Y=34.2854 Z=0
    g2: GeomPoint [constr] X=-197.902 Y=30.7408 Z=0
    g3: GeomPoint [constr] X=-197.561 Y=25.8282 Z=0
    g4: GeomPoint [constr] X=-196.022 Y=30.0568 Z=0
    g5: LineSegment [constr] StartX=-194.483 StartY=34.2854 StartZ=0 EndX=-196.022 EndY=30.0568 EndZ=0
    g6: LineSegment [constr] StartX=-196.022 StartY=30.0568 StartZ=0 EndX=-197.561 EndY=25.8282 EndZ=0
    g7: LineSegment [constr] StartX=-197.902 StartY=30.7408 StartZ=0 EndX=-196.022 EndY=30.0568 EndZ=0
    g8: LineSegment [constr] StartX=-196.022 StartY=30.0568 StartZ=0 EndX=-194.143 EndY=29.3727 EndZ=0
    g9: LineSegment [constr] StartX=-195.338 StartY=31.9362 StartZ=0 EndX=-196.022 EndY=30.0568 EndZ=0
    g10: LineSegment [constr] StartX=-196.022 StartY=30.0568 StartZ=0 EndX=-196.706 EndY=28.1774 EndZ=0
    g11: LineSegment [constr] StartX=-196.022 StartY=30.0568 StartZ=0 EndX=-196.821 EndY=30.3475 EndZ=0
    g12: LineSegment [constr] StartX=-196.022 StartY=30.0568 StartZ=0 EndX=-195.223 EndY=29.7661 EndZ=0
    g13: LineSegment StartX=-194.539 StartY=31.6454 StartZ=0 EndX=-195.907 EndY=27.8867 EndZ=0
    g14: LineSegment StartX=-196.137 StartY=32.2269 StartZ=0 EndX=-197.505 EndY=28.4681 EndZ=0
    g15: LineSegment StartX=-196.137 StartY=32.2269 StartZ=0 EndX=-194.539 EndY=31.6454 EndZ=0
    g16: LineSegment StartX=-197.505 StartY=28.4681 StartZ=0 EndX=-195.907 EndY=27.8867 EndZ=0
  constraints (34):
    c: Symmetric(g-5,g-5,g1)
    c: Symmetric(g-5,g-6,g0)
    c: Symmetric(g-6,g-6,g3)
    c: Symmetric(g-5,g-6,g2)
    c: Coincident(g5,g1)
    c: Coincident(g5,g4)
    c: Coincident(g6,g4)
    c: Coincident(g6,g3)
    c: Equal(g5,g6)
    c: Coincident(g7,g2)
    c: Coincident(g7,g4)
    c: Coincident(g8,g4)
    c: Coincident(g8,g0)
    c: Equal(g7,g8)
    c: Coincident(g11,g9)
    c: Coincident(g12,g9)
    c: Tangent(g10,g9) = -1.5708
    c: Perpendicular(g11,g9)
    c: Parallel(g9,g-4)
    c: Equal(g9,g10)
    c: Parallel(g12,g11)
    c: Equal(g11,g12)
    c: Distance(g11,g12) = 1.7
    c: Distance(g9,g10) = 4
    c: Symmetric(g13,g13,g12)
    c: Parallel(g13,g9)
    c: Symmetric(g14,g14,g11)
    c: Symmetric(g15,g15,g9)
    c: Parallel(g15,g11)
    c: Symmetric(g16,g16,g10)
    c: Coincident(g16,g14)
    c: Coincident(g15,g14)
    c: Coincident(g13,g15)
    c: Coincident(g9,g4)
FEATURE [Part::Extrusion] Extrude059  label="Extrude buco esterno per micro switch sinistro"
  Base = -> Sketch056
  Dir = (0,-1,2e-16)
  DirMode = 2
  FaceMakerClass = Part::FaceMakerBullseye
  FaceMakerMode = 3
  LengthFwd = 2
  LengthRev = 0
  Placement = pos=(0,12.6,0) rot=(0,0,1;0rad)
  Solid = true
  Symmetric = false
FEATURE [Sketcher::SketchObject] Sketch057  label="buco interno per SWITCH"
  ArcFitTolerance = 1e-06
  AttachmentSupport = -> [XZ_Plane]
  ExternalGeometry = -> [Sketch]
  FullyConstrained = true
  MakeInternals = false
  MapMode = 5
  Placement = pos=(0,0,0) rot=(1,0,0;1.5708rad)
  sketch-geometry (10):
    g0: GeomPoint [constr] X=-187.821 Y=29.2 Z=0
    g1: LineSegment [constr] StartX=-188.505 StartY=27.3206 StartZ=0 EndX=-193.203 EndY=29.0307 EndZ=0
    g2: LineSegment [constr] StartX=-190.809 StartY=35.6086 StartZ=0 EndX=-195.597 EndY=22.4529 EndZ=0
    g3: GeomPoint [constr] X=-193.203 Y=29.0307 Z=0
    g4: LineSegment [constr] StartX=-196.492 StartY=30.2278 StartZ=0 EndX=-189.914 EndY=27.8336 EndZ=0
    g5: LineSegment StartX=-194.098 StartY=36.8056 StartZ=0 EndX=-187.52 EndY=34.4115 EndZ=0
    g6: LineSegment StartX=-194.098 StartY=36.8056 StartZ=0 EndX=-198.886 EndY=23.6499 EndZ=0
    g7: LineSegment StartX=-187.52 StartY=34.4115 StartZ=0 EndX=-192.308 EndY=21.2558 EndZ=0
    g8: LineSegment StartX=-198.886 StartY=23.6499 StartZ=0 EndX=-192.308 EndY=21.2558 EndZ=0
    g9: LineSegment [constr] StartX=-187.821 StartY=29.2 StartZ=0 EndX=-188.505 EndY=27.3206 EndZ=0
  constraints (23):
    c: Symmetric(g-3,g-3,g0)
    c: Perpendicular(g1,g-3)
    c: Parallel(g2,g-3)
    c: Symmetric(g2,g2,g3)
    c: Perpendicular(g2,g4)
    c: Symmetric(g4,g4,g3)
    c: Distance(g2) = 14
    c: Distance(g4) = 7
    c: Distance(g1) = 5
    c: Parallel(g5,g4)
    c: Parallel(g7,g2)
    c: Symmetric(g5,g5,g2)
    c: Symmetric(g6,g6,g4)
    c: Symmetric(g7,g7,g4)
    c: Symmetric(g8,g8,g2)
    c: Coincident(g6,g5)
    c: Coincident(g7,g5)
    c: Coincident(g8,g7)
    c: Coincident(g3,g1)
    c: Coincident(g9,g0)
    c: Parallel(g9,g-3)
    c: Distance(g9) = 2
    c: Coincident(g1,g9)
FEATURE [Sketcher::SketchObject] Sketch058  label="buco esterno per SWITCH"
  ArcFitTolerance = 1e-06
  AttachmentSupport = -> [XZ_Plane]
  ExternalGeometry = -> [Sketch057]
  FullyConstrained = true
  MakeInternals = false
  MapMode = 5
  Placement = pos=(0,0,0) rot=(1,0,0;1.5708rad)
  sketch-geometry (12):
    g0: GeomPoint [constr] X=-190.809 Y=35.6086 Z=0
    g1: GeomPoint [constr] X=-196.492 Y=30.2278 Z=0
    g2: GeomPoint [constr] X=-189.914 Y=27.8336 Z=0
    g3: GeomPoint [constr] X=-195.597 Y=22.4529 Z=0
    g4: GeomPoint [constr] X=-193.203 Y=29.0307 Z=0
    g5: LineSegment [constr] StartX=-192.006 StartY=32.3196 StartZ=0 EndX=-194.4 EndY=25.7418 EndZ=0
    g6: GeomPoint [constr] X=-193.203 Y=29.0307 Z=0
    g7: LineSegment [constr] StartX=-195.082 StartY=29.7148 StartZ=0 EndX=-191.324 EndY=28.3467 EndZ=0
    g8: LineSegment StartX=-193.885 StartY=33.0037 StartZ=0 EndX=-190.127 EndY=31.6356 EndZ=0
    g9: LineSegment StartX=-190.127 StartY=31.6356 StartZ=0 EndX=-192.521 EndY=25.0578 EndZ=0
    g10: LineSegment StartX=-196.28 StartY=26.4258 StartZ=0 EndX=-192.521 EndY=25.0578 EndZ=0
    g11: LineSegment StartX=-193.885 StartY=33.0037 StartZ=0 EndX=-196.28 EndY=26.4258 EndZ=0
  constraints (21):
    c: Symmetric(g-6,g-6,g3)
    c: Symmetric(g-4,g-6,g2)
    c: Symmetric(g-5,g-4,g0)
    c: Symmetric(g-5,g-6,g1)
    c: Symmetric(g1,g2,g4)
    c: Parallel(g5,g-4)
    c: Symmetric(g5,g5,g6)
    c: Perpendicular(g7,g5)
    c: Symmetric(g7,g7,g6)
    c: Distance(g5) = 7
    c: Distance(g7) = 4
    c: Parallel(g8,g7)
    c: Parallel(g11,g5)
    c: Symmetric(g8,g8,g5)
    c: Symmetric(g9,g9,g7)
    c: Symmetric(g10,g10,g5)
    c: Symmetric(g11,g11,g7)
    c: Coincident(g11,g8)
    c: Coincident(g9,g8)
    c: Coincident(g9,g10)
    c: Coincident(g6,g4)
FEATURE [Part::Extrusion] Extrude060  label="Extrude buco interno per SWITCH destro"
  Base = -> Sketch057
  Dir = (0,-1,2e-16)
  DirMode = 2
  FaceMakerClass = Part::FaceMakerBullseye
  FaceMakerMode = 3
  LengthFwd = 13.2
  LengthRev = 0
  Placement = pos=(0,2.6,0) rot=(0,0,1;0rad)
  Solid = true
  Symmetric = false
FEATURE [Part::Extrusion] Extrude061  label="Extrude buco esterno per SWITCH destro"
  Base = -> Sketch058
  Dir = (0,-1,2e-16)
  DirMode = 2
  FaceMakerClass = Part::FaceMakerBullseye
  FaceMakerMode = 3
  LengthFwd = 2
  LengthRev = 0
  Placement = pos=(0,-10.6,0) rot=(0,0,1;0rad)
  Solid = true
  Symmetric = false
FEATURE [Sketcher::SketchObject] Sketch059  label="buco per spazio introduzione SWITCH"
  ArcFitTolerance = 1e-06
  AttachmentSupport = -> [XZ_Plane]
  ExternalGeometry = -> [Sketch057,Sketch010]
  FullyConstrained = true
  MakeInternals = false
  MapMode = 5
  Placement = pos=(0,0,0) rot=(1,0,0;1.5708rad)
  sketch-geometry (8):
    g0: LineSegment [constr] StartX=-201.368 StartY=36.3521 StartZ=0 EndX=-195.094 EndY=34.0687 EndZ=0
    g1: LineSegment [constr] StartX=-194.098 StartY=36.8056 StartZ=0 EndX=-195.094 EndY=34.0687 EndZ=0
    g2: LineSegment StartX=-198.658 StartY=24.2771 StartZ=0 EndX=-199.654 EndY=21.5401 EndZ=0
    g3: LineSegment StartX=-199.654 StartY=21.5401 StartZ=0 EndX=-181.196 EndY=14.822 EndZ=0
    g4: LineSegment StartX=-181.196 StartY=14.822 StartZ=0 EndX=-180.2 EndY=17.559 EndZ=0
    g5: LineSegment StartX=-180.2 StartY=17.559 StartZ=0 EndX=-198.658 EndY=24.2771 EndZ=0
    g6: LineSegment [constr] StartX=-204.932 StartY=26.5605 StartZ=0 EndX=-198.658 EndY=24.2771 EndZ=0
    g7: LineSegment [constr] StartX=-198.658 StartY=24.2771 StartZ=0 EndX=-199.654 EndY=21.5401 EndZ=0
  constraints (20):
    c: Parallel(g1,g-3)
    c: Parallel(g0,g-4)
    c: Coincident(g0,g-4)
    c: Coincident(g1,g-3)
    c: Coincident(g0,g1)
    c: Coincident(g3,g2)
    c: Coincident(g4,g3)
    c: Coincident(g5,g4)
    c: Coincident(g5,g2)
    c: Parallel(g5,g-5)
    c: Parallel(g3,g-5)
    c: Parallel(g4,g-6)
    c: DistanceX(g-6,g4) = 0
    c: Coincident(g6,g-5)
    c: Equal(g6,g0)
    c: Coincident(g7,g6)
    c: Equal(g7,g1)
    c: Tangent(g7,g-3)
    c: Coincident(g2,g6)
    c: Coincident(g2,g7)
FEATURE [Part::Extrusion] Extrude062  label="Extrude buco per spazio introduzione SWITCH"
  Base = -> Sketch059
  Dir = (0,-1,2e-16)
  DirMode = 2
  FaceMakerClass = Part::FaceMakerBullseye
  FaceMakerMode = 3
  LengthFwd = 13.2
  LengthRev = 0
  Solid = true
  Symmetric = true
FEATURE [Part::Extrusion] Extrude063  label="Extrude buco interno per SWITCH sinistro"
  Base = -> Sketch057
  Dir = (0,-1,2e-16)
  DirMode = 2
  FaceMakerClass = Part::FaceMakerBullseye
  FaceMakerMode = 3
  LengthFwd = 13.2
  LengthRev = 0
  Placement = pos=(0,10.6,0) rot=(0,0,1;0rad)
  Solid = true
  Symmetric = false
FEATURE [Part::Extrusion] Extrude064  label="Extrude buco esterno per SWITCH sinistro"
  Base = -> Sketch058
  Dir = (0,-1,2e-16)
  DirMode = 2
  FaceMakerClass = Part::FaceMakerBullseye
  FaceMakerMode = 3
  LengthFwd = 2
  LengthRev = 0
  Placement = pos=(0,12.6,0) rot=(0,0,1;0rad)
  Solid = true
  Symmetric = false
FEATURE [Sketcher::SketchObject] Sketch060  label="prova spazio switch"
  ArcFitTolerance = 1e-06
  AttachmentSupport = -> [XY_Plane003]
  FullyConstrained = true
  MakeInternals = false
  MapMode = 5
  sketch-geometry (12):
    g0: LineSegment StartX=-7.5 StartY=10 StartZ=0 EndX=-7.5 EndY=-10 EndZ=0
    g1: LineSegment StartX=-7.5 StartY=-10 StartZ=0 EndX=7.5 EndY=-10 EndZ=0
    g2: LineSegment StartX=7.5 StartY=-10 StartZ=0 EndX=7.5 EndY=10 EndZ=0
    g3: LineSegment StartX=7.5 StartY=10 StartZ=0 EndX=-7.5 EndY=10 EndZ=0
    g4: GeomPoint [constr] X=0 Y=0 Z=0
    g5: LineSegment StartX=-2.95 StartY=-5.55 StartZ=0 EndX=2.95 EndY=-5.55 EndZ=0
    g6: LineSegment StartX=2.95 StartY=-5.55 StartZ=0 EndX=2.95 EndY=5.55 EndZ=0
    g7: LineSegment StartX=2.95 StartY=5.55 StartZ=0 EndX=-2.95 EndY=5.55 EndZ=0
    g8: LineSegment StartX=-2.95 StartY=5.55 StartZ=0 EndX=-2.95 EndY=-5.55 EndZ=0
    g9: GeomPoint [constr] X=0 Y=0 Z=0
    g10: Circle CenterX=0 CenterY=7.75 CenterZ=0 NormalX=0 NormalY=0 NormalZ=1 AngleXU=0 Radius=1.6
    g11: Circle CenterX=0 CenterY=-7.75 CenterZ=0 NormalX=0 NormalY=0 NormalZ=1 AngleXU=0 Radius=1.6
  constraints (29):
    c: Coincident(g0,g1)
    c: Coincident(g1,g2)
    c: Coincident(g2,g3)
    c: Coincident(g3,g0)
    c: Vertical(g0)
    c: Vertical(g2)
    c: Horizontal(g1)
    c: Horizontal(g3)
    c: Symmetric(g2,g0,g4)
    c: Coincident(g4,g-1)
    c: Distance(g3) = 15
    c: Distance(g2) = 20
    c: Coincident(g5,g6)
    c: Coincident(g6,g7)
    c: Coincident(g7,g8)
    c: Coincident(g8,g5)
    c: Horizontal(g5)
    c: Horizontal(g7)
    c: Vertical(g6)
    c: Vertical(g8)
    c: Symmetric(g7,g5,g9)
    c: Coincident(g9,g4)
    c: Distance(g7) = 5.9
    c: Distance(g6) = 11.1
    c: Diameter(g10) = 3.2
    c: Equal(g10,g11)
    c: Symmetric(g10,g11,g-1)
    c: PointOnObject(g10,g-2)
    c: Distance(g10,g11) = 15.5
FEATURE [Part::Extrusion] Extrude065  label="Extrude prova spazio switch"
  Base = -> Sketch060
  Dir = (0,0,1)
  DirMode = 2
  FaceMakerClass = Part::FaceMakerBullseye
  FaceMakerMode = 3
  LengthFwd = 5
  LengthRev = 0
  Solid = true
  Symmetric = false
FEATURE [Sketcher::SketchObject] Sketch061  label="struttura esterna blocco switch"
  ArcFitTolerance = 1e-06
  AttachmentSupport = -> [XZ_Plane003]
  FullyConstrained = true
  MakeInternals = false
  MapMode = 5
  Placement = pos=(0,0,0) rot=(1,0,0;1.5708rad)
  sketch-geometry (5):
    g0: LineSegment StartX=-1 StartY=-5.1 StartZ=0 EndX=1 EndY=-5.1 EndZ=0
    g1: LineSegment StartX=1 StartY=-5.1 StartZ=0 EndX=1 EndY=5.1 EndZ=0
    g2: LineSegment StartX=1 StartY=5.1 StartZ=0 EndX=-1 EndY=5.1 EndZ=0
    g3: LineSegment StartX=-1 StartY=5.1 StartZ=0 EndX=-1 EndY=-5.1 EndZ=0
    g4: GeomPoint [constr] X=0 Y=0 Z=0
  constraints (12):
    c: Coincident(g0,g1)
    c: Coincident(g1,g2)
    c: Coincident(g2,g3)
    c: Coincident(g3,g0)
    c: Horizontal(g0)
    c: Horizontal(g2)
    c: Vertical(g1)
    c: Vertical(g3)
    c: Symmetric(g2,g0,g4)
    c: Distance(g1,g3) = 2
    c: Distance(g0,g2) = 10.2
    c: Coincident(g4,g-1)
FEATURE [Part::Extrusion] Extrude066  label="Extrude struttura esterna blocco switch"
  Base = -> Sketch061
  Dir = (0,-1,2e-16)
  DirMode = 2
  FaceMakerClass = Part::FaceMakerBullseye
  FaceMakerMode = 3
  LengthFwd = 16.8
  LengthRev = 0
  Solid = true
  Symmetric = true
FEATURE [Sketcher::SketchObject] Sketch062  label="struttura interna blocco switch"
  ArcFitTolerance = 1e-06
  AttachmentSupport = -> [XZ_Plane003]
  ExternalGeometry = -> [Sketch061]
  FullyConstrained = true
  MakeInternals = false
  MapMode = 5
  Placement = pos=(0,0,0) rot=(1,0,0;1.5708rad)
  sketch-geometry (5):
    g0: LineSegment StartX=-1 StartY=3.1 StartZ=0 EndX=-1 EndY=-3.1 EndZ=0
    g1: LineSegment StartX=-1 StartY=-3.1 StartZ=0 EndX=1 EndY=-3.1 EndZ=0
    g2: LineSegment StartX=1 StartY=-3.1 StartZ=0 EndX=1 EndY=3.1 EndZ=0
    g3: LineSegment StartX=1 StartY=3.1 StartZ=0 EndX=-1 EndY=3.1 EndZ=0
    g4: GeomPoint [constr] X=0 Y=0 Z=0
  constraints (12):
    c: Coincident(g0,g1)
    c: Coincident(g1,g2)
    c: Coincident(g2,g3)
    c: Coincident(g3,g0)
    c: Vertical(g0)
    c: Vertical(g2)
    c: Horizontal(g1)
    c: Horizontal(g3)
    c: Symmetric(g2,g0,g4)
    c: Coincident(g4,g-1)
    c: Distance(g0) = 6.2
    c: Equal(g3,g-3)
FEATURE [Part::Extrusion] Extrude067  label="Extrude struttura interna blocco switch"
  Base = -> Sketch062
  Dir = (0,-1,2e-16)
  DirMode = 2
  FaceMakerClass = Part::FaceMakerBullseye
  FaceMakerMode = 3
  LengthFwd = 12.8
  LengthRev = 0
  Solid = true
  Symmetric = true
FEATURE [Part::Cut] Cut036  label="struttura blocco switch"
  Base = -> Extrude066
  Refine = true
  Tool = -> Extrude067
FEATURE [Sketcher::SketchObject] Sketch063  label="blocchi tra switch"
  ArcFitTolerance = 1e-06
  AttachmentSupport = -> [XZ_Plane003]
  ExternalGeometry = -> [Sketch061,Sketch062]
  FullyConstrained = true
  MakeInternals = false
  MapMode = 5
  Placement = pos=(0,0,0) rot=(1,0,0;1.5708rad)
  sketch-geometry (8):
    g0: LineSegment StartX=-3 StartY=5.1 StartZ=0 EndX=-1 EndY=5.1 EndZ=0
    g1: LineSegment StartX=-1 StartY=5.1 StartZ=0 EndX=-1 EndY=3.1 EndZ=0
    g2: LineSegment StartX=-1 StartY=3.1 StartZ=0 EndX=-3 EndY=3.1 EndZ=0
    g3: LineSegment StartX=-3 StartY=3.1 StartZ=0 EndX=-3 EndY=5.1 EndZ=0
    g4: LineSegment StartX=-3 StartY=-3.1 StartZ=0 EndX=-1 EndY=-3.1 EndZ=0
    g5: LineSegment StartX=-1 StartY=-3.1 StartZ=0 EndX=-1 EndY=-5.1 EndZ=0
    g6: LineSegment StartX=-1 StartY=-5.1 StartZ=0 EndX=-3 EndY=-5.1 EndZ=0
    g7: LineSegment StartX=-3 StartY=-5.1 StartZ=0 EndX=-3 EndY=-3.1 EndZ=0
  constraints (20):
    c: Horizontal(g0)
    c: Coincident(g1,g0)
    c: Coincident(g2,g1)
    c: Horizontal(g2)
    c: Coincident(g3,g2)
    c: Coincident(g3,g0)
    c: Vertical(g3)
    c: Horizontal(g4)
    c: Coincident(g5,g4)
    c: Coincident(g6,g5)
    c: Horizontal(g6)
    c: Coincident(g7,g6)
    c: Coincident(g7,g4)
    c: Vertical(g7)
    c: Coincident(g0,g-4)
    c: Coincident(g1,g-5)
    c: Coincident(g4,g-6)
    c: Coincident(g5,g-7)
    c: Distance(g0) = 2
    c: Distance(g4) = 2
FEATURE [PartDesign::Body] Body003  label="blocco switch e neopixel"
  AllowCompound = false
  Group = -> [Sketch060,Sketch061,Sketch062,Sketch063]
  Origin = -> Origin003
FEATURE [Part::Extrusion] Extrude068  label="Extrude blocchi tra switch"
  Base = -> Sketch063
  Dir = (0,-1,2e-16)
  DirMode = 2
  FaceMakerClass = Part::FaceMakerBullseye
  FaceMakerMode = 3
  LengthFwd = 7.6
  LengthRev = 0
  Solid = true
  Symmetric = true
FEATURE [Part::MultiFuse] Fusion002  label="Fusion blocco switch"
  Refine = true
  Shapes = -> [Cut036,Extrude068]
FEATURE [Sketcher::SketchObject] Sketch066  label="piano per rampino"
  ArcFitTolerance = 1e-06
  AttachmentSupport = -> [XZ_Plane002]
  ExternalGeometry = -> [Sketch045]
  FullyConstrained = true
  MakeInternals = false
  MapMode = 5
  Placement = pos=(0,0,0) rot=(1,0,0;1.5708rad)
  sketch-geometry (4):
    g0: LineSegment StartX=5.4 StartY=5.1 StartZ=0 EndX=5.4 EndY=3.9 EndZ=0
    g1: LineSegment StartX=5.4 StartY=3.9 StartZ=0 EndX=7 EndY=3.9 EndZ=0
    g2: LineSegment StartX=7 StartY=3.9 StartZ=0 EndX=7 EndY=5.1 EndZ=0
    g3: LineSegment StartX=7 StartY=5.1 StartZ=0 EndX=5.4 EndY=5.1 EndZ=0
  constraints (11):
    c: Coincident(g0,g1)
    c: Coincident(g1,g2)
    c: Coincident(g2,g3)
    c: Coincident(g3,g0)
    c: Vertical(g0)
    c: Vertical(g2)
    c: Horizontal(g1)
    c: Horizontal(g3)
    c: Distance(g0,g2) = 1.6
    c: Distance(g1,g3) = 1.2
    c: Coincident(g2,g-3)
FEATURE [Sketcher::SketchObject] Sketch064  label="rampini_per_serraggio_struttura"
  ArcFitTolerance = 1e-06
  AttachmentSupport = -> [XZ_Plane002]
  ExternalGeometry = -> [Sketch066,Sketch045]
  FullyConstrained = true
  MakeInternals = false
  MapMode = 5
  Placement = pos=(0,0,0) rot=(1,0,0;1.5708rad)
  sketch-geometry (7):
    g0: LineSegment StartX=7 StartY=5.1 StartZ=0 EndX=7 EndY=3.9 EndZ=0
    g1: LineSegment StartX=7 StartY=3.9 StartZ=0 EndX=9 EndY=3.9 EndZ=0
    g2: LineSegment StartX=7 StartY=5.1 StartZ=0 EndX=7 EndY=5.1 EndZ=0
    g3: LineSegment StartX=7 StartY=5.1 StartZ=0 EndX=7 EndY=7.5 EndZ=0
    g4: LineSegment StartX=9 StartY=5.1 StartZ=0 EndX=9 EndY=3.9 EndZ=0
    g5: LineSegment StartX=7 StartY=7.5 StartZ=0 EndX=9 EndY=7.5 EndZ=0
    g6: LineSegment StartX=9 StartY=7.5 StartZ=0 EndX=9 EndY=5.1 EndZ=0
  constraints (20):
    c: Vertical(g0)
    c: Coincident(g1,g0)
    c: Horizontal(g1)
    c: Coincident(g2,g0)
    c: Horizontal(g2)
    c: Coincident(g3,g2)
    c: Vertical(g3)
    c: Coincident(g5,g3)
    c: Coincident(g4,g6)
    c: Coincident(g4,g1)
    c: Vertical(g4)
    c: Coincident(g0,g-3)
    c: DistanceY(g-4,g3) = 2.4
    c: DistanceX(g1,g1) = 2
    c: DistanceY(g2,g6) = 0
    c: DistanceX(g2,g2) = 0
    c: DistanceY(g0,g0) = 1.2
    c: Coincident(g5,g6)
    c: Horizontal(g5)
    c: Vertical(g6)
FEATURE [Part::Extrusion] Extrude070  label="Extrude piano per rampino"
  Base = -> Sketch066
  Dir = (0,-1,2e-16)
  DirMode = 2
  FaceMakerClass = Part::FaceMakerBullseye
  FaceMakerMode = 3
  LengthFwd = 17
  LengthRev = 0
  Solid = true
  Symmetric = true
FEATURE [Part::Extrusion] Extrude071  label="Extrude rampini_per_serraggio_struttura"
  Base = -> Sketch064
  Dir = (0,-1,2e-16)
  DirMode = 2
  FaceMakerClass = Part::FaceMakerBullseye
  FaceMakerMode = 3
  LengthFwd = 5
  LengthRev = 0
  Solid = true
  Symmetric = true
FEATURE [Part::MultiFuse] Fusion003  label="Fusion supporto neopixel completo"
  Refine = true
  Shapes = -> [Fusion001,Extrude070,Extrude071]
FEATURE [Sketcher::SketchObject] Sketch067  label="perno per blocco switch"
  ArcFitTolerance = 1e-06
  AttachmentSupport = -> [XZ_Plane]
  ExternalGeometry = -> [Sketch,Sketch010]
  FullyConstrained = true
  MakeInternals = false
  MapMode = 5
  Placement = pos=(0,0,0) rot=(1,0,0;1.5708rad)
  sketch-geometry (14):
    g0: LineSegment StartX=-191.073 StartY=24.9429 StartZ=0 EndX=-185.81 EndY=23.0276 EndZ=0
    g1: LineSegment StartX=-183.76 StartY=23.9839 StartZ=0 EndX=-182.392 EndY=27.7427 EndZ=0
    g2: LineSegment StartX=-183.348 StartY=29.7934 StartZ=0 EndX=-188.61 EndY=31.7087 EndZ=0
    g3: LineSegment StartX=-188.61 StartY=31.7087 StartZ=0 EndX=-191.073 EndY=24.9429 EndZ=0
    g4: GeomPoint [constr] X=-186.459 Y=27.0946 Z=0
    g5: LineSegment StartX=-189.022 StartY=25.8992 StartZ=0 EndX=-185.263 EndY=24.5311 EndZ=0
    g6: LineSegment StartX=-185.263 StartY=24.5311 StartZ=0 EndX=-183.895 EndY=28.2899 EndZ=0
    g7: LineSegment StartX=-183.895 StartY=28.2899 StartZ=0 EndX=-187.654 EndY=29.658 EndZ=0
    g8: LineSegment StartX=-187.654 StartY=29.658 StartZ=0 EndX=-189.022 EndY=25.8992 EndZ=0
    g9: GeomPoint [constr] X=-186.459 Y=27.0946 Z=0
    g10: ArcOfCircle CenterX=-185.263 CenterY=24.5311 CenterZ=0 NormalX=0 NormalY=0 NormalZ=1 AngleXU=0 Radius=1.6 StartAngle=4.36332 EndAngle=5.93412
    g11: GeomPoint [constr] X=-184.307 Y=22.4804 Z=0
    g12: ArcOfCircle CenterX=-183.895 CenterY=28.2899 CenterZ=0 NormalX=0 NormalY=0 NormalZ=1 AngleXU=0 Radius=1.6 StartAngle=5.93412 EndAngle=7.50492
    g13: GeomPoint [constr] X=-181.844 Y=29.2462 Z=0
  constraints (30):
    c: Coincident(g2,g3)
    c: Coincident(g3,g0)
    c: Symmetric(g13,g0,g4)
    c: Distance(g11,g3) = 7.2
    c: Distance(g0,g2) = 7.2
    c: Parallel(g3,g1)
    c: Parallel(g2,g0)
    c: Perpendicular(g2,g3)
    c: Coincident(g5,g6)
    c: Coincident(g6,g7)
    c: Coincident(g7,g8)
    c: Coincident(g8,g5)
    c: Symmetric(g7,g5,g9)
    c: Distance(g6,g8) = 4
    c: Distance(g5,g7) = 4
    c: Coincident(g9,g4)
    c: Parallel(g8,g6)
    c: Parallel(g7,g5)
    c: Perpendicular(g7,g8)
    c: Tangent(g8,g-3)
    c: Tangent(g2,g-4)
    c: PointOnObject(g11,g1)
    c: PointOnObject(g11,g0)
    c: Tangent(g1,g10) = -1.5708
    c: Tangent(g0,g10) = -1.5708
    c: PointOnObject(g13,g1)
    c: Tangent(g1,g12) = -1.5708
    c: Tangent(g2,g12) = -1.5708
    c: Equal(g10,g12)
    c: Coincident(g10,g5)
FEATURE [Part::Extrusion] Extrude072  label="Extrude perno per blocco switch"
  Base = -> Sketch067
  Dir = (0,-1,2e-16)
  DirMode = 2
  FaceMakerClass = Part::FaceMakerBullseye
  FaceMakerMode = 3
  LengthFwd = 25.2
  LengthRev = 0
  Solid = true
  Symmetric = true
FEATURE [Part::MultiFuse] Fusion
  Refine = true
  Shapes = -> [Extrude,Sweep,Extrude007,Extrude011,Extrude005,Extrude012,Extrude013,Extrude016,Extrude031,Extrude039,Extrude045,Extrude072]
FEATURE [Part::Cut] Cut
  Base = -> Fusion
  Refine = true
  Tool = -> Extrude001
FEATURE [Part::Cut] Cut001
  Base = -> Cut
  Refine = true
  Tool = -> Extrude004
FEATURE [Part::Cut] Cut002
  Base = -> Cut001
  Refine = true
  Tool = -> Extrude006
FEATURE [Part::Cut] Cut003
  Base = -> Cut002
  Refine = true
  Tool = -> Extrude008
FEATURE [Part::Cut] Cut004
  Base = -> Cut003
  Refine = true
  Tool = -> Extrude009
FEATURE [Part::Cut] Cut005
  Base = -> Cut004
  Refine = true
  Tool = -> Extrude010
FEATURE [Part::Cut] Cut006
  Base = -> Cut005
  Refine = true
  Tool = -> Extrude014
FEATURE [Part::Cut] Cut007
  Base = -> Cut006
  Refine = true
  Tool = -> Extrude015
FEATURE [Part::Cut] Cut008
  Base = -> Cut007
  Refine = true
  Tool = -> Extrude018
FEATURE [Part::Cut] Cut009
  Base = -> Cut008
  Refine = true
  Tool = -> Extrude019
FEATURE [Part::Cut] Cut010
  Base = -> Cut009
  Refine = true
  Tool = -> Extrude020
FEATURE [Part::Cut] Cut011
  Base = -> Cut010
  Refine = true
  Tool = -> Extrude021
FEATURE [Part::Cut] Cut012
  Base = -> Cut011
  Refine = true
  Tool = -> Extrude022
FEATURE [Part::Cut] Cut013
  Base = -> Cut012
  Refine = true
  Tool = -> Extrude023
FEATURE [Part::Cut] Cut014
  Base = -> Cut013
  Refine = true
  Tool = -> Extrude032
FEATURE [Part::Cut] Cut015
  Base = -> Cut014
  Refine = true
  Tool = -> Extrude033
FEATURE [Part::Cut] Cut016
  Base = -> Cut015
  Refine = true
  Tool = -> Extrude034
FEATURE [Part::Cut] Cut017
  Base = -> Cut016
  Refine = true
  Tool = -> Extrude035
FEATURE [Part::Cut] Cut018
  Base = -> Cut017
  Refine = true
  Tool = -> Extrude036
FEATURE [Part::Cut] Cut019
  Base = -> Cut018
  Refine = true
  Tool = -> Extrude037
FEATURE [Part::Cut] Cut020
  Base = -> Cut019
  Refine = true
  Tool = -> Extrude030
FEATURE [Part::Cut] Cut022
  Base = -> Cut020
  Refine = true
  Tool = -> Extrude038
FEATURE [Part::Cut] Cut023
  Base = -> Cut022
  Refine = true
  Tool = -> Extrude041
FEATURE [Part::Cut] Cut024
  Base = -> Cut023
  Refine = true
  Tool = -> Extrude040
FEATURE [Part::Cut] Cut025
  Base = -> Cut024
  Refine = true
  Tool = -> Extrude042
FEATURE [Part::Cut] Cut026
  Base = -> Cut025
  Refine = true
  Tool = -> Extrude043
FEATURE [Part::Cut] Cut027
  Base = -> Cut026
  Refine = true
  Tool = -> Extrude044
FEATURE [Part::Cut] Cut028
  Base = -> Cut027
  Refine = true
  Tool = -> Extrude046
FEATURE [Part::Cut] Cut029
  Base = -> Cut028
  Refine = true
  Tool = -> Extrude047
FEATURE [Part::Cut] Cut033
  Base = -> Cut029
  Refine = true
  Tool = -> Extrude055
FEATURE [Part::Cut] Cut034
  Base = -> Cut033
  Refine = true
  Tool = -> Extrude056
FEATURE [Part::Cut] Cut035
  Base = -> Cut034
  Refine = true
  Tool = -> Extrude057
FEATURE [Part::Cut] Cut037
  Base = -> Cut035
  Refine = true
  Tool = -> Extrude060
FEATURE [Part::Cut] Cut038
  Base = -> Cut037
  Refine = true
  Tool = -> Extrude061
FEATURE [Part::Cut] Cut039
  Base = -> Cut038
  Refine = true
  Tool = -> Extrude063
FEATURE [Part::Cut] Cut040
  Base = -> Cut039
  Refine = true
  Tool = -> Extrude064
FEATURE [Part::Cut] Cut041
  Base = -> Cut040
  Refine = true
  Tool = -> Extrude062
FEATURE [Sketcher::SketchObject] Sketch068  label="base con smusso sopra neopixel"
  ArcFitTolerance = 1e-06
  AttachmentSupport = -> [YZ_Plane002]
  FullyConstrained = true
  MakeInternals = false
  MapMode = 5
  Placement = pos=(0,0,0) rot=(0.57735,0.57735,0.57735;2.0944rad)
  sketch-geometry (5):
    g0: LineSegment StartX=-9.5 StartY=-6.1 StartZ=0 EndX=9.5 EndY=-6.1 EndZ=0
    g1: LineSegment StartX=9.5 StartY=-6.1 StartZ=0 EndX=9.5 EndY=6.1 EndZ=0
    g2: LineSegment StartX=9.5 StartY=6.1 StartZ=0 EndX=-9.5 EndY=6.1 EndZ=0
    g3: LineSegment StartX=-9.5 StartY=6.1 StartZ=0 EndX=-9.5 EndY=-6.1 EndZ=0
    g4: GeomPoint [constr] X=0 Y=0 Z=0
  constraints (12):
    c: Coincident(g0,g1)
    c: Coincident(g1,g2)
    c: Coincident(g2,g3)
    c: Coincident(g3,g0)
    c: Horizontal(g0)
    c: Horizontal(g2)
    c: Vertical(g1)
    c: Vertical(g3)
    c: Symmetric(g2,g0,g4)
    c: Distance(g1,g3) = 19
    c: Distance(g0,g2) = 12.2
    c: Coincident(g4,g-1)
FEATURE [PartDesign::Body] Body002  label="supporto per neopixel"
  AllowCompound = false
  Group = -> [Sketch045,Sketch046,Sketch047,Sketch048,Sketch049,Sketch064,Sketch066,Sketch068]
  Origin = -> Origin002
FEATURE [Part::Extrusion] Extrude073  label="Extrude base con smusso sopra neopixel"
  Base = -> Sketch068
  Dir = (1,0,0)
  DirMode = 2
  FaceMakerClass = Part::FaceMakerBullseye
  FaceMakerMode = 3
  LengthFwd = -1
  LengthRev = 0
  Solid = true
  Symmetric = false
FEATURE [Part::Chamfer] Chamfer  label="Chamfer frontale supporto neopixel da fondere al supporto"
  Base = -> Extrude073
  EdgeLinks = -> Extrude073 [Edge4,Edge7,Edge10,Edge12]
  Edges = 4 edges r=0.5: [Edge4,Edge7,Edge10,Edge12]
FEATURE [Sketcher::SketchObject] Sketch069  label="cilindro minore"
  ArcFitTolerance = 1e-06
  AttachmentSupport = -> [XZ_Plane004]
  FullyConstrained = true
  MakeInternals = false
  MapMode = 5
  Placement = pos=(0,0,0) rot=(1,0,0;1.5708rad)
  sketch-geometry (1):
    g0: Circle CenterX=0 CenterY=0 CenterZ=0 NormalX=0 NormalY=0 NormalZ=1 AngleXU=0 Radius=5.8
  constraints (2):
    c: Diameter(g0) = 11.6
    c: Coincident(g0,g-1)
FEATURE [Sketcher::SketchObject] Sketch070  label="cilindro maggiore"
  ArcFitTolerance = 1e-06
  AttachmentSupport = -> [XZ_Plane004]
  ExternalGeometry = -> [Sketch069]
  FullyConstrained = true
  MakeInternals = false
  MapMode = 5
  Placement = pos=(0,0,0) rot=(1,0,0;1.5708rad)
  sketch-geometry (1):
    g0: Circle CenterX=0 CenterY=0 CenterZ=0 NormalX=0 NormalY=0 NormalZ=1 AngleXU=0 Radius=6.5
  constraints (2):
    c: Coincident(g0,g-1)
    c: Diameter(g0) = 13
FEATURE [Sketcher::SketchObject] Sketch071  label="buco interno"
  ArcFitTolerance = 1e-06
  AttachmentSupport = -> [XZ_Plane004]
  ExternalGeometry = -> [Sketch069]
  FullyConstrained = true
  MakeInternals = false
  MapMode = 5
  Placement = pos=(0,0,0) rot=(1,0,0;1.5708rad)
  sketch-geometry (1):
    g0: Circle CenterX=0 CenterY=0 CenterZ=0 NormalX=0 NormalY=0 NormalZ=1 AngleXU=0 Radius=5
  constraints (2):
    c: Coincident(g0,g-1)
    c: Diameter(g0) = 10
FEATURE [PartDesign::Pad] Pad
  Direction = (0,-1,2e-16)
  Length = 1.2
  Length2 = 10
  Placement = pos=(0,0,0) rot=(1,0,0;1.5708rad)
  Profile = -> Sketch070
  ReferenceAxis = -> Sketch070 [N_Axis]
  Refine = true
  Suppressed = false
  Type = 0
FEATURE [PartDesign::Pad] Pad001
  BaseFeature = -> Pad
  Direction = (0,-1,2e-16)
  Length = 5.6
  Length2 = 10
  Placement = pos=(0,0,0) rot=(1,0,0;1.5708rad)
  Profile = -> Sketch069
  ReferenceAxis = -> Sketch069 [N_Axis]
  Refine = true
  Suppressed = false
  Type = 0
FEATURE [PartDesign::Pocket] Pocket
  BaseFeature = -> Pad001
  Direction = (0,1,-2e-16)
  Length = 7
  Length2 = 5
  Midplane = true
  Placement = pos=(0,0,0) rot=(1,0,0;1.5708rad)
  Profile = -> Sketch071
  ReferenceAxis = -> Sketch071 [N_Axis]
  Refine = true
  Suppressed = false
  Type = 0
FEATURE [PartDesign::Fillet] Fillet
  Base = -> Pocket [Face7]
  BaseFeature = -> Pocket
  Placement = pos=(0,0,0) rot=(1,0,0;1.5708rad)
  Radius = 1
  Refine = true
  SupportTransform = false
  Suppressed = false
  UseAllEdges = false
FEATURE [PartDesign::Body] Body004  label="pulsanti lato sinistro"
  AllowCompound = false
  Group = -> [Sketch069,Sketch070,Sketch071,Pad,Pad001,Pocket,Fillet]
  Origin = -> Origin004
  Tip = -> Fillet
FEATURE [Sketcher::SketchObject] Sketch072  label="buco per saldature e diodo driver solenoide"
  ArcFitTolerance = 1e-06
  AttachmentSupport = -> [XZ_Plane]
  ExternalGeometry = -> [Sketch038]
  FullyConstrained = true
  MakeInternals = false
  MapMode = 5
  Placement = pos=(0,0,0) rot=(1,0,0;1.5708rad)
  sketch-geometry (4):
    g0: LineSegment StartX=-209.225 StartY=-40.6939 StartZ=0 EndX=-204.154 EndY=-29.8182 EndZ=0
    g1: LineSegment StartX=-204.154 StartY=-29.8182 StartZ=0 EndX=-206.51 EndY=-28.7194 EndZ=0
    g2: LineSegment StartX=-206.51 StartY=-28.7194 StartZ=0 EndX=-211.582 EndY=-39.5951 EndZ=0
    g3: LineSegment StartX=-211.582 StartY=-39.5951 StartZ=0 EndX=-209.225 EndY=-40.6939 EndZ=0
  constraints (11):
    c: Coincident(g1,g0)
    c: Coincident(g2,g1)
    c: Coincident(g3,g2)
    c: Coincident(g3,g0)
    c: Parallel(g-3,g0)
    c: Parallel(g0,g2)
    c: Perpendicular(g0,g3)
    c: Perpendicular(g1,g0)
    c: Distance(g3) = 2.6
    c: Distance(g2) = 12
    c: Coincident(g0,g-3)
FEATURE [Part::Extrusion] Extrude074  label="Extrude buco per saldature e diodo driver solenoide"
  Base = -> Sketch072
  Dir = (0,-1,2e-16)
  DirMode = 2
  FaceMakerClass = Part::FaceMakerBullseye
  FaceMakerMode = 3
  LengthFwd = 14.6
  LengthRev = 0
  Solid = true
  Symmetric = true
FEATURE [Part::Cut] Cut042
  Base = -> Cut041
  Refine = true
  Tool = -> Extrude074
FEATURE [Sketcher::SketchObject] Sketch073  label="fori slargati blocco solenoide"
  ArcFitTolerance = 1e-06
  AttachmentSupport = -> [XY_Plane]
  ExternalGeometry = -> [Sketch030]
  FullyConstrained = true
  MakeInternals = false
  MapMode = 5
  sketch-geometry (2):
    g0: Circle CenterX=-152.209 CenterY=6.95 CenterZ=0 NormalX=0 NormalY=0 NormalZ=1 AngleXU=0 Radius=3.7
    g1: Circle CenterX=-130.41 CenterY=-6.95 CenterZ=0 NormalX=0 NormalY=0 NormalZ=1 AngleXU=0 Radius=3.7
  constraints (4):
    c: Diameter(g0) = 7.4
    c: Coincident(g0,g-3)
    c: Diameter(g1) = 7.4
    c: Coincident(g1,g-4)
FEATURE [Part::Extrusion] Extrude075  label="Extrude fori slargati blocco solenoide"
  Base = -> Sketch073
  Dir = (0,0,1)
  DirMode = 2
  FaceMakerClass = Part::FaceMakerBullseye
  FaceMakerMode = 3
  LengthFwd = 1.5
  LengthRev = 0
  Placement = pos=(0,0,36.4) rot=(0,0,1;0rad)
  Solid = true
  Symmetric = false
FEATURE [Part::Cut] Cut043
  Base = -> Cut042
  Refine = true
  Tool = -> Extrude075
FEATURE [Sketcher::SketchObject] Sketch074  label="lato sx pistola"
  ArcFitTolerance = 1e-06
  AttachmentSupport = -> [XZ_Plane]
  ExternalGeometry = -> [Sketch016,Sketch,Sketch058]
  FullyConstrained = true
  MakeInternals = false
  MapMode = 5
  Placement = pos=(0,0,0) rot=(1,0,0;1.5708rad)
  sketch-geometry (37):
    g0: LineSegment StartX=-82.8 StartY=3.2 StartZ=0 EndX=0 EndY=3.2 EndZ=0
    g1: LineSegment StartX=-82.8 StartY=3.2 StartZ=0 EndX=-82.8 EndY=6.2 EndZ=0
    g2: LineSegment [constr] StartX=-107.6 StartY=18 StartZ=0 EndX=-107.6 EndY=20 EndZ=0
    g3: LineSegment [constr] StartX=-132.428 StartY=18 StartZ=0 EndX=-132.428 EndY=20 EndZ=0
    g4: LineSegment StartX=-132.428 StartY=20 StartZ=0 EndX=-107.6 EndY=20 EndZ=0
    g5: ArcOfCircle CenterX=-107.6 CenterY=4 CenterZ=0 NormalX=0 NormalY=0 NormalZ=1 AngleXU=0 Radius=16 StartAngle=0.137937 EndAngle=1.5708
    g6: LineSegment StartX=-82.8 StartY=6.2 StartZ=0 EndX=-91.752 EndY=6.2 EndZ=0
    g7: LineSegment [constr] StartX=-145.743 StartY=8.32624 StartZ=0 EndX=-147.645 EndY=8.94427 EndZ=0
    g8: ArcOfCircle CenterX=-132.428 CenterY=4 CenterZ=0 NormalX=0 NormalY=0 NormalZ=1 AngleXU=0 Radius=16 StartAngle=1.5708 EndAngle=2.82743
    g9: LineSegment StartX=-215.932 StartY=-80.4316 StartZ=0 EndX=-176.685 EndY=-80.4316 EndZ=0
    g10: LineSegment StartX=-147.645 StartY=8.94427 StartZ=0 EndX=-176.685 EndY=-80.4316 EndZ=0
    g11: LineSegment [constr] StartX=-193.988 StartY=-2.33927 StartZ=0 EndX=-192.176 EndY=-3.18451 EndZ=0
    g12: LineSegment [constr] StartX=-217.232 StartY=-52.1862 StartZ=0 EndX=-215.42 EndY=-53.0314 EndZ=0
    g13: LineSegment StartX=-192.176 StartY=-3.18451 StartZ=0 EndX=-215.42 EndY=-53.0314 EndZ=0
    g14: ArcOfCircle CenterX=-184.801 CenterY=-67.3089 CenterZ=0 NormalX=0 NormalY=0 NormalZ=1 AngleXU=0 Radius=33.7833 StartAngle=2.70526 EndAngle=3.54053
    g15: ArcOfCircle CenterX=-207.583 CenterY=4 CenterZ=0 NormalX=0 NormalY=0 NormalZ=1 AngleXU=0 Radius=17 StartAngle=5.84685 EndAngle=7.56663
    g16: LineSegment StartX=-202.765 StartY=20.303 StartZ=0 EndX=-195.887 EndY=39.2 EndZ=0
    g17: LineSegment [constr] StartX=-193.885 StartY=33.0037 StartZ=0 EndX=-197.644 EndY=34.3718 EndZ=0
    g18: LineSegment StartX=-195.887 StartY=39.2 StartZ=0 EndX=0 EndY=39.2 EndZ=0
    g19: LineSegment StartX=0 StartY=3.2 StartZ=0 EndX=0 EndY=39.2 EndZ=0
    g20: LineSegment StartX=-189.939 StartY=31.5672 StartZ=0 EndX=-192.333 EndY=24.9893 EndZ=0
    g21: LineSegment StartX=-196.467 StartY=26.4942 StartZ=0 EndX=-194.073 EndY=33.0721 EndZ=0
    g22: Circle CenterX=-213.443 CenterY=-76.8316 CenterZ=0 NormalX=0 NormalY=0 NormalZ=1 AngleXU=0 Radius=1.8
    g23: Circle CenterX=-179.305 CenterY=-76.8316 CenterZ=0 NormalX=0 NormalY=0 NormalZ=1 AngleXU=0 Radius=1.8
    g24: Circle CenterX=-184.08 CenterY=34.8 CenterZ=0 NormalX=0 NormalY=0 NormalZ=1 AngleXU=0 Radius=1.8
    g25: Circle CenterX=-78.51 CenterY=34.8 CenterZ=0 NormalX=0 NormalY=0 NormalZ=1 AngleXU=0 Radius=1.8
    g26: Circle CenterX=-78.51 CenterY=7.6 CenterZ=0 NormalX=0 NormalY=0 NormalZ=1 AngleXU=0 Radius=1.8
    g27: Circle CenterX=-5.6 CenterY=34.8 CenterZ=0 NormalX=0 NormalY=0 NormalZ=1 AngleXU=0 Radius=1.8
    g28: Circle CenterX=-5.6 CenterY=7.6 CenterZ=0 NormalX=0 NormalY=0 NormalZ=1 AngleXU=0 Radius=1.8
    g29: LineSegment StartX=-190.127 StartY=31.6356 StartZ=0 EndX=-189.939 EndY=31.5672 EndZ=0
    g30: LineSegment StartX=-194.073 StartY=33.0721 StartZ=0 EndX=-193.885 EndY=33.0037 EndZ=0
    g31: LineSegment StartX=-193.885 StartY=33.0037 StartZ=0 EndX=-190.127 EndY=31.6356 EndZ=0
    g32: LineSegment StartX=-196.467 StartY=26.4942 StartZ=0 EndX=-192.333 EndY=24.9893 EndZ=0
    g33: Circle CenterX=-19 CenterY=21.2 CenterZ=0 NormalX=0 NormalY=0 NormalZ=1 AngleXU=0 Radius=6.3
    g34: Circle CenterX=-42 CenterY=21.2 CenterZ=0 NormalX=0 NormalY=0 NormalZ=1 AngleXU=0 Radius=6.3
    g35: Circle CenterX=-65 CenterY=21.2 CenterZ=0 NormalX=0 NormalY=0 NormalZ=1 AngleXU=0 Radius=6.3
    g36: LineSegment [constr] StartX=-4 StartY=21.2 StartZ=0 EndX=-65 EndY=21.2 EndZ=0
  constraints (96):
    c: Coincident(g0,g-41)
    c: Horizontal(g0)
    c: PointOnObject(g0,g-39)
    c: Coincident(g1,g0)
    c: Vertical(g1)
    c: DistanceY(g1,g1) = 3
    c: Coincident(g2,g-17)
    c: Vertical(g2)
    c: Coincident(g3,g-16)
    c: Vertical(g3)
    c: DistanceY(g2,g2) = 2
    c: DistanceY(g3,g3) = 2
    c: Coincident(g4,g3)
    c: Coincident(g4,g2)
    c: Coincident(g5,g-17)
    c: Coincident(g5,g2)
    c: Coincident(g6,g1)
    c: Horizontal(g6)
    c: Coincident(g6,g5)
    c: Coincident(g7,g-15)
    c: Coincident(g8,g7)
    c: Coincident(g8,g3)
    c: Coincident(g8,g-15)
    c: Horizontal(g9)
    c: DistanceY(g-13,g9) = 2
    c: Coincident(g10,g7)
    c: Parallel(g10,g-14)
    c: Coincident(g9,g10)
    c: Distance(g11) = 2
    c: Coincident(g11,g-11)
    c: Perpendicular(g-11,g11)
    c: Distance(g12) = 2
    c: Coincident(g12,g-12)
    c: Perpendicular(g-11,g12)
    c: Coincident(g13,g11)
    c: Coincident(g13,g12)
    c: Coincident(g14,g-32)
    c: Coincident(g14,g12)
    c: Coincident(g14,g9)
    c: Coincident(g15,g-10)
    c: Coincident(g15,g11)
    c: Parallel(g16,g-22)
    c: Distance(g17) = 4
    c: PointOnObject(g17,g16)
    c: Coincident(g15,g16)
    c: Horizontal(g18)
    c: Coincident(g18,g16)
    c: Coincident(g19,g0)
    c: PointOnObject(g19,g-39)
    c: DistanceY(g19,g-36) = 2
    c: Coincident(g18,g19)
    c: Diameter(g22) = 3.6
    c: Coincident(g22,g-9)
    c: Diameter(g23) = 3.6
    c: Coincident(g23,g-8)
    c: Diameter(g24) = 3.6
    c: Diameter(g25) = 3.6
    c: Diameter(g26) = 3.6
    c: Diameter(g27) = 3.6
    c: Diameter(g28) = 3.6
    c: Coincident(g27,g-4)
    c: Coincident(g28,g-3)
    c: Coincident(g25,g-6)
    c: Coincident(g26,g-5)
    c: Coincident(g24,g-7)
    c: Parallel(g20,g-21)
    c: Equal(g20,g-21)
    c: Parallel(g21,g-19)
    c: Equal(g21,g-19)
    c: Distance(g29) = 0.2
    c: Distance(g30) = 0.2
    c: Parallel(g29,g-20)
    c: Parallel(g31,g-20)
    c: Equal(g31,g-20)
    c: Coincident(g30,g31)
    c: Coincident(g31,g29)
    c: Coincident(g29,g-21)
    c: Parallel(g30,g31)
    c: Coincident(g17,g30)
    c: Coincident(g20,g29)
    c: Coincident(g21,g30)
    c: Perpendicular(g16,g17)
    c: Coincident(g32,g21)
    c: Coincident(g32,g20)
    c: Perpendicular(g10,g7)
    c: Diameter(g33) = 12.6
    c: Diameter(g34) = 12.6
    c: Diameter(g35) = 12.6
    c: Horizontal(g36)
    c: PointOnObject(g33,g36)
    c: PointOnObject(g34,g36)
    c: DistanceX(g34,g33) = 23
    c: DistanceX(g35,g34) = 23
    c: DistanceX(g33,g36) = 15
    c: Symmetric(g-24,g-24,g36)
    c: Coincident(g36,g35)
FEATURE [Part::Extrusion] Extrude076  label="Extrude lato sx pistola"
  Base = -> Sketch074
  Dir = (0,-1,2e-16)
  DirMode = 2
  FaceMakerClass = Part::FaceMakerBullseye
  FaceMakerMode = 3
  LengthFwd = -2
  LengthRev = 0
  Solid = true
  Symmetric = false
FEATURE [Sketcher::SketchObject] Sketch075  label="lato dx pistola"
  ArcFitTolerance = 1e-06
  AttachmentSupport = -> [XZ_Plane]
  ExternalGeometry = -> [Sketch016,Sketch,Sketch058,Sketch074]
  FullyConstrained = true
  MakeInternals = false
  MapMode = 5
  Placement = pos=(0,0,0) rot=(1,0,0;1.5708rad)
  sketch-geometry (61):
    g0: LineSegment StartX=-82.8 StartY=3.2 StartZ=0 EndX=0 EndY=3.2 EndZ=0
    g1: LineSegment StartX=-82.8 StartY=3.2 StartZ=0 EndX=-82.8 EndY=6.2 EndZ=0
    g2: LineSegment [constr] StartX=-107.6 StartY=18 StartZ=0 EndX=-107.6 EndY=20 EndZ=0
    g3: LineSegment [constr] StartX=-132.428 StartY=18 StartZ=0 EndX=-132.428 EndY=20 EndZ=0
    g4: LineSegment StartX=-132.428 StartY=20 StartZ=0 EndX=-107.6 EndY=20 EndZ=0
    g5: ArcOfCircle CenterX=-107.6 CenterY=4 CenterZ=0 NormalX=0 NormalY=0 NormalZ=1 AngleXU=0 Radius=16 StartAngle=0.137937 EndAngle=1.5708
    g6: LineSegment StartX=-82.8 StartY=6.2 StartZ=0 EndX=-91.752 EndY=6.2 EndZ=0
    g7: LineSegment [constr] StartX=-145.743 StartY=8.32624 StartZ=0 EndX=-147.645 EndY=8.94427 EndZ=0
    g8: ArcOfCircle CenterX=-132.428 CenterY=4 CenterZ=0 NormalX=0 NormalY=0 NormalZ=1 AngleXU=0 Radius=16 StartAngle=1.5708 EndAngle=2.82743
    g9: LineSegment StartX=-215.932 StartY=-80.4316 StartZ=0 EndX=-176.685 EndY=-80.4316 EndZ=0
    g10: LineSegment StartX=-147.645 StartY=8.94427 StartZ=0 EndX=-176.685 EndY=-80.4316 EndZ=0
    g11: LineSegment [constr] StartX=-193.988 StartY=-2.33927 StartZ=0 EndX=-192.176 EndY=-3.18451 EndZ=0
    g12: LineSegment [constr] StartX=-217.232 StartY=-52.1862 StartZ=0 EndX=-215.42 EndY=-53.0314 EndZ=0
    g13: LineSegment StartX=-192.176 StartY=-3.18451 StartZ=0 EndX=-215.42 EndY=-53.0314 EndZ=0
    g14: ArcOfCircle CenterX=-184.801 CenterY=-67.3089 CenterZ=0 NormalX=0 NormalY=0 NormalZ=1 AngleXU=0 Radius=33.7833 StartAngle=2.70526 EndAngle=3.54053
    g15: ArcOfCircle CenterX=-207.583 CenterY=4 CenterZ=0 NormalX=0 NormalY=0 NormalZ=1 AngleXU=0 Radius=17 StartAngle=5.84685 EndAngle=7.56663
    g16: LineSegment StartX=-202.765 StartY=20.303 StartZ=0 EndX=-195.887 EndY=39.2 EndZ=0
    g17: LineSegment [constr] StartX=-193.885 StartY=33.0037 StartZ=0 EndX=-197.644 EndY=34.3718 EndZ=0
    g18: LineSegment StartX=-195.887 StartY=39.2 StartZ=0 EndX=0 EndY=39.2 EndZ=0
    g19: LineSegment StartX=0 StartY=3.2 StartZ=0 EndX=0 EndY=39.2 EndZ=0
    g20: LineSegment StartX=-189.939 StartY=31.5672 StartZ=0 EndX=-192.333 EndY=24.9893 EndZ=0
    g21: LineSegment StartX=-196.467 StartY=26.4942 StartZ=0 EndX=-194.073 EndY=33.0721 EndZ=0
    g22: Circle CenterX=-213.443 CenterY=-76.8316 CenterZ=0 NormalX=0 NormalY=0 NormalZ=1 AngleXU=0 Radius=1.8
    g23: Circle CenterX=-179.305 CenterY=-76.8316 CenterZ=0 NormalX=0 NormalY=0 NormalZ=1 AngleXU=0 Radius=1.8
    g24: Circle CenterX=-184.08 CenterY=34.8 CenterZ=0 NormalX=0 NormalY=0 NormalZ=1 AngleXU=0 Radius=1.8
    g25: Circle CenterX=-78.51 CenterY=34.8 CenterZ=0 NormalX=0 NormalY=0 NormalZ=1 AngleXU=0 Radius=1.8
    g26: Circle CenterX=-78.51 CenterY=7.6 CenterZ=0 NormalX=0 NormalY=0 NormalZ=1 AngleXU=0 Radius=1.8
    g27: Circle CenterX=-5.6 CenterY=34.8 CenterZ=0 NormalX=0 NormalY=0 NormalZ=1 AngleXU=0 Radius=1.8
    g28: Circle CenterX=-5.6 CenterY=7.6 CenterZ=0 NormalX=0 NormalY=0 NormalZ=1 AngleXU=0 Radius=1.8
    g29: LineSegment StartX=-190.127 StartY=31.6356 StartZ=0 EndX=-189.939 EndY=31.5672 EndZ=0
    g30: LineSegment StartX=-194.073 StartY=33.0721 StartZ=0 EndX=-193.885 EndY=33.0037 EndZ=0
    g31: LineSegment StartX=-193.885 StartY=33.0037 StartZ=0 EndX=-190.127 EndY=31.6356 EndZ=0
    g32: LineSegment StartX=-196.467 StartY=26.4942 StartZ=0 EndX=-192.333 EndY=24.9893 EndZ=0
    g33: LineSegment [constr] StartX=-4 StartY=21.2 StartZ=0 EndX=-87.91 EndY=21.2 EndZ=0
    g34: GeomPoint [constr] X=-4 Y=21.2 Z=0
    g35: LineSegment [constr] StartX=-15.2 StartY=33.7 StartZ=0 EndX=-15.2 EndY=8.7 EndZ=0
    g36: LineSegment [constr] StartX=-15.2 StartY=33.7 StartZ=0 EndX=-56.2 EndY=33.7 EndZ=0
    g37: LineSegment [constr] StartX=-15.2 StartY=8.7 StartZ=0 EndX=-56.2 EndY=8.7 EndZ=0
    g38: LineSegment [constr] StartX=-56.2 StartY=33.7 StartZ=0 EndX=-56.2 EndY=8.7 EndZ=0
    g39: Circle CenterX=-18.6 CenterY=30.3 CenterZ=0 NormalX=0 NormalY=0 NormalZ=1 AngleXU=0 Radius=3.4
    g40: Circle CenterX=-18.6 CenterY=12.1 CenterZ=0 NormalX=0 NormalY=0 NormalZ=1 AngleXU=0 Radius=3.4
    g41: Circle CenterX=-43.2 CenterY=30.3 CenterZ=0 NormalX=0 NormalY=0 NormalZ=1 AngleXU=0 Radius=3.4
    g42: Circle CenterX=-43.2 CenterY=12.1 CenterZ=0 NormalX=0 NormalY=0 NormalZ=1 AngleXU=0 Radius=3.4
    g43: LineSegment [constr] StartX=-4 StartY=21.2 StartZ=0 EndX=-15.2 EndY=21.2 EndZ=0
    g44: LineSegment [constr] StartX=-15.2 StartY=21.2 StartZ=0 EndX=-36.2 EndY=21.2 EndZ=0
    g45: LineSegment [constr] StartX=-41.5 StartY=16.2 StartZ=0 EndX=-30.9 EndY=16.2 EndZ=0
    g46: LineSegment [constr] StartX=-30.9 StartY=16.2 StartZ=0 EndX=-30.9 EndY=26.2 EndZ=0
    g47: LineSegment [constr] StartX=-30.9 StartY=26.2 StartZ=0 EndX=-41.5 EndY=26.2 EndZ=0
    g48: LineSegment [constr] StartX=-41.5 StartY=26.2 StartZ=0 EndX=-41.5 EndY=16.2 EndZ=0
    g49: GeomPoint [constr] X=-36.2 Y=21.2 Z=0
    g50: Circle CenterX=-36.2 CenterY=21.2 CenterZ=0 NormalX=0 NormalY=0 NormalZ=1 AngleXU=0 Radius=2.8
    g51: LineSegment [constr] StartX=-24.2 StartY=26.7 StartZ=0 EndX=-24.2 EndY=15.7 EndZ=0
    g52: Circle CenterX=-24.2 CenterY=26.7 CenterZ=0 NormalX=0 NormalY=0 NormalZ=1 AngleXU=0 Radius=3
    g53: Circle CenterX=-24.2 CenterY=15.7 CenterZ=0 NormalX=0 NormalY=0 NormalZ=1 AngleXU=0 Radius=3
    g54: GeomPoint X=-18.6 Y=30.3 Z=0
    g55: GeomPoint X=-18.6 Y=12.1 Z=0
    g56: GeomPoint X=-43.2 Y=12.1 Z=0
    g57: GeomPoint X=-43.2 Y=30.3 Z=0
    g58: Circle CenterX=-65 CenterY=21.2 CenterZ=0 NormalX=0 NormalY=0 NormalZ=1 AngleXU=0 Radius=1.5
    g59: Circle CenterX=-42 CenterY=21.2 CenterZ=0 NormalX=0 NormalY=0 NormalZ=1 AngleXU=0 Radius=1.5
    g60: Circle CenterX=-19 CenterY=21.2 CenterZ=0 NormalX=0 NormalY=0 NormalZ=1 AngleXU=0 Radius=1.5
  constraints (149):
    c: Coincident(g0,g-41)
    c: Horizontal(g0)
    c: PointOnObject(g0,g-39)
    c: Coincident(g1,g0)
    c: Vertical(g1)
    c: DistanceY(g1,g1) = 3
    c: Coincident(g2,g-17)
    c: Vertical(g2)
    c: Coincident(g3,g-16)
    c: Vertical(g3)
    c: DistanceY(g2,g2) = 2
    c: DistanceY(g3,g3) = 2
    c: Coincident(g4,g3)
    c: Coincident(g4,g2)
    c: Coincident(g5,g-17)
    c: Coincident(g5,g2)
    c: Coincident(g6,g1)
    c: Horizontal(g6)
    c: Coincident(g6,g5)
    c: Coincident(g7,g-15)
    c: Coincident(g8,g7)
    c: Coincident(g8,g3)
    c: Coincident(g8,g-15)
    c: Horizontal(g9)
    c: DistanceY(g-13,g9) = 2
    c: Coincident(g10,g7)
    c: Parallel(g10,g-14)
    c: Coincident(g9,g10)
    c: Distance(g11) = 2
    c: Coincident(g11,g-11)
    c: Perpendicular(g-11,g11)
    c: Distance(g12) = 2
    c: Coincident(g12,g-12)
    c: Perpendicular(g-11,g12)
    c: Coincident(g13,g11)
    c: Coincident(g13,g12)
    c: Coincident(g14,g-32)
    c: Coincident(g14,g12)
    c: Coincident(g14,g9)
    c: Coincident(g15,g-10)
    c: Coincident(g15,g11)
    c: Parallel(g16,g-22)
    c: Distance(g17) = 4
    c: PointOnObject(g17,g16)
    c: Coincident(g15,g16)
    c: Horizontal(g18)
    c: Coincident(g18,g16)
    c: Coincident(g19,g0)
    c: PointOnObject(g19,g-39)
    c: DistanceY(g19,g-36) = 2
    c: Coincident(g18,g19)
    c: Diameter(g22) = 3.6
    c: Coincident(g22,g-9)
    c: Diameter(g23) = 3.6
    c: Coincident(g23,g-8)
    c: Diameter(g24) = 3.6
    c: Diameter(g25) = 3.6
    c: Diameter(g26) = 3.6
    c: Diameter(g27) = 3.6
    c: Diameter(g28) = 3.6
    c: Coincident(g27,g-4)
    c: Coincident(g28,g-3)
    c: Coincident(g25,g-6)
    c: Coincident(g26,g-5)
    c: Coincident(g24,g-7)
    c: Parallel(g20,g-21)
    c: Equal(g20,g-21)
    c: Parallel(g21,g-19)
    c: Equal(g21,g-19)
    c: Distance(g29) = 0.2
    c: Distance(g30) = 0.2
    c: Parallel(g29,g-20)
    c: Parallel(g31,g-20)
    c: Equal(g31,g-20)
    c: Coincident(g30,g31)
    c: Coincident(g31,g29)
    c: Coincident(g29,g-21)
    c: Parallel(g30,g31)
    c: Coincident(g17,g30)
    c: Coincident(g20,g29)
    c: Coincident(g21,g30)
    c: Perpendicular(g16,g17)
    c: Coincident(g32,g21)
    c: Coincident(g32,g20)
    c: Perpendicular(g10,g7)
    c: Horizontal(g33)
    c: Symmetric(g-24,g-24,g33)
    c: PointOnObject(g33,g-28)
    c: Symmetric(g-24,g-24,g34)
    c: DistanceY(g35,g35) = 25
    c: Symmetric(g35,g35,g33)
    c: Distance(g36) = 41
    c: Coincident(g36,g35)
    c: Horizontal(g36)
    c: Coincident(g37,g35)
    c: Horizontal(g37)
    c: Coincident(g38,g36)
    c: Vertical(g38)
    c: Coincident(g37,g38)
    c: Diameter(g39) = 6.8
    c: Diameter(g40) = 6.8
    c: Tangent(g39,g36)
    c: Tangent(g40,g37)
    c: Tangent(g39,g35)
    c: Tangent(g40,g35)
    c: Diameter(g41) = 6.8
    c: Diameter(g42) = 6.8
    c: Tangent(g41,g36)
    c: Tangent(g42,g37)
    c: DistanceX(g41,g39) = 24.6
    c: DistanceX(g42,g40) = 24.6
    c: Distance(g43) = 11.2
    c: Coincident(g43,g33)
    c: PointOnObject(g43,g33)
    c: PointOnObject(g43,g35)
    c: Distance(g44) = 21
    c: Coincident(g44,g43)
    c: PointOnObject(g44,g33)
    c: Coincident(g45,g46)
    c: Coincident(g46,g47)
    c: Coincident(g47,g48)
    c: Coincident(g48,g45)
    c: Horizontal(g45)
    c: Horizontal(g47)
    c: Vertical(g46)
    c: Vertical(g48)
    c: Symmetric(g47,g45,g49)
    c: Distance(g46,g48) = 10.6
    c: Distance(g45,g47) = 10
    c: Coincident(g49,g44)
    c: Diameter(g50) = 5.6
    c: Coincident(g50,g44)
    c: Distance(g51) = 11
    c: Symmetric(g51,g51,g33)
    c: DistanceX(g51,g43) = 9
    c: Diameter(g52) = 6
    c: Coincident(g52,g51)
    c: Diameter(g53) = 6
    c: Coincident(g53,g51)
    c: Coincident(g40,g55)
    c: Coincident(g39,g54)
    c: Coincident(g41,g57)
    c: Coincident(g42,g56)
    c: Diameter(g58) = 3
    c: Diameter(g59) = 3
    c: Diameter(g60) = 3
    c: Coincident(g58,g-44)
    c: Coincident(g59,g-46)
    c: Coincident(g60,g-45)
FEATURE [Sketcher::SketchObject] Sketch076  label="lato sx pistola - scavi pulsanti"
  ArcFitTolerance = 1e-06
  AttachmentSupport = -> [XZ_Plane]
  ExternalGeometry = -> [Sketch074]
  FullyConstrained = true
  MakeInternals = false
  MapMode = 5
  Placement = pos=(0,0,0) rot=(1,0,0;1.5708rad)
  sketch-geometry (3):
    g0: Circle CenterX=-65 CenterY=21.2 CenterZ=0 NormalX=0 NormalY=0 NormalZ=1 AngleXU=0 Radius=7.3
    g1: Circle CenterX=-42 CenterY=21.2 CenterZ=0 NormalX=0 NormalY=0 NormalZ=1 AngleXU=0 Radius=7.3
    g2: Circle CenterX=-19 CenterY=21.2 CenterZ=0 NormalX=0 NormalY=0 NormalZ=1 AngleXU=0 Radius=7.3
  constraints (6):
    c: Diameter(g0) = 14.6
    c: Diameter(g1) = 14.6
    c: Diameter(g2) = 14.6
    c: Coincident(g0,g-3)
    c: Coincident(g1,g-4)
    c: Coincident(g2,g-5)
FEATURE [Part::Extrusion] Extrude077  label="Extrude lato sx pistola - scavi pulsanti"
  Base = -> Sketch076
  Dir = (0,-1,2e-16)
  DirMode = 2
  FaceMakerClass = Part::FaceMakerBullseye
  FaceMakerMode = 3
  LengthFwd = -1.2
  LengthRev = 0
  Solid = true
  Symmetric = false
FEATURE [Part::Cut] Cut044
  Base = -> Extrude076
  Refine = true
  Tool = -> Extrude077
FEATURE [Part::Extrusion] Extrude078  label="Extrude lato dx pistola"
  Base = -> Sketch075
  Dir = (0,-1,2e-16)
  DirMode = 2
  FaceMakerClass = Part::FaceMakerBullseye
  FaceMakerMode = 3
  LengthFwd = 2
  LengthRev = 0
  Solid = true
  Symmetric = false
FEATURE [Sketcher::SketchObject] Sketch077  label="lato dx pistola - scavi pulsanti"
  ArcFitTolerance = 1e-06
  AttachmentSupport = -> [XZ_Plane]
  ExternalGeometry = -> [Sketch075]
  FullyConstrained = true
  MakeInternals = false
  MapMode = 5
  Placement = pos=(0,0,0) rot=(1,0,0;1.5708rad)
  sketch-geometry (4):
    g0: LineSegment StartX=-27.2 StartY=26.7 StartZ=0 EndX=-27.2 EndY=15.7 EndZ=0
    g1: LineSegment StartX=-21.2 StartY=26.7 StartZ=0 EndX=-21.2 EndY=15.7 EndZ=0
    g2: ArcOfCircle CenterX=-24.2 CenterY=26.7 CenterZ=0 NormalX=0 NormalY=0 NormalZ=1 AngleXU=0 Radius=3 StartAngle=5.96642e-06 EndAngle=3.14159
    g3: ArcOfCircle CenterX=-24.2 CenterY=15.7 CenterZ=0 NormalX=0 NormalY=0 NormalZ=1 AngleXU=0 Radius=3 StartAngle=3.14159 EndAngle=6.28319
  constraints (10):
    c: Vertical(g0)
    c: Coincident(g2,g-3)
    c: Vertical(g1)
    c: Coincident(g3,g-4)
    c: Tangent(g1,g-3)
    c: Tangent(g0,g-3)
    c: Tangent(g3,g0) = -1.5708
    c: Coincident(g3,g1)
    c: Tangent(g0,g2) = -1.5708
    c: Coincident(g1,g2)
FEATURE [Part::Extrusion] Extrude079  label="Extrude lato dx pistola - scavi pulsanti"
  Base = -> Sketch077
  Dir = (0,-1,2e-16)
  DirMode = 2
  FaceMakerClass = Part::FaceMakerBullseye
  FaceMakerMode = 3
  LengthFwd = 1.2
  LengthRev = 0
  Solid = true
  Symmetric = false
FEATURE [Part::Cut] Cut045
  Base = -> Extrude078
  Refine = true
  Tool = -> Extrude079
FEATURE [Sketcher::SketchObject] Sketch078
  ArcFitTolerance = 1e-06
  AttachmentSupport = -> [XZ_Plane005]
  FullyConstrained = true
  MakeInternals = false
  MapMode = 5
  Placement = pos=(0,0,0) rot=(1,0,0;1.5708rad)
  sketch-geometry (5):
    g0: LineSegment [constr] StartX=0 StartY=5.5 StartZ=0 EndX=0 EndY=-5.5 EndZ=0
    g1: ArcOfCircle CenterX=0 CenterY=5.5 CenterZ=0 NormalX=0 NormalY=0 NormalZ=1 AngleXU=0 Radius=2.7 StartAngle=0 EndAngle=3.14159
    g2: ArcOfCircle CenterX=0 CenterY=-5.5 CenterZ=0 NormalX=0 NormalY=0 NormalZ=1 AngleXU=0 Radius=2.7 StartAngle=3.1416 EndAngle=6.28318
    g3: LineSegment StartX=-2.7 StartY=5.5 StartZ=0 EndX=-2.7 EndY=-5.50001 EndZ=0
    g4: LineSegment StartX=2.7 StartY=5.5 StartZ=0 EndX=2.7 EndY=-5.50001 EndZ=0
  constraints (13):
    c: Distance(g0) = 11
    c: Vertical(g0)
    c: Symmetric(g0,g0,g-1)
    c: Radius(g1) = 2.7
    c: Coincident(g1,g0)
    c: Radius(g2) = 2.7
    c: Coincident(g2,g0)
    c: Vertical(g3)
    c: Vertical(g4)
    c: Coincident(g2,g4)
    c: Coincident(g2,g3)
    c: Tangent(g3,g1) = -1.5708
    c: Tangent(g4,g1) = 1.5708
FEATURE [PartDesign::Pad] Pad002
  Direction = (0,-1,2e-16)
  Length = 0.8
  Length2 = 10
  Placement = pos=(0,0,0) rot=(1,0,0;1.5708rad)
  Profile = -> Sketch078
  ReferenceAxis = -> Sketch078 [N_Axis]
  Refine = true
  Suppressed = false
  Type = 0
FEATURE [Sketcher::SketchObject] Sketch079
  ArcFitTolerance = 1e-06
  AttachmentSupport = -> [XZ_Plane005]
  ExternalGeometry = -> [Sketch078]
  FullyConstrained = true
  MakeInternals = false
  MapMode = 5
  Placement = pos=(0,0,0) rot=(1,0,0;1.5708rad)
  sketch-geometry (2):
    g0: Circle CenterX=-1e-16 CenterY=5.5 CenterZ=0 NormalX=0 NormalY=0 NormalZ=1 AngleXU=0 Radius=2.7
    g1: Circle CenterX=0 CenterY=-5.5 CenterZ=0 NormalX=0 NormalY=0 NormalZ=1 AngleXU=0 Radius=2.7
  constraints (4):
    c: Coincident(g0,g-3)
    c: PointOnObject(g-3,g0)
    c: Coincident(g1,g-4)
    c: Equal(g1,g-4)
FEATURE [PartDesign::Pad] Pad003
  BaseFeature = -> Pad002
  Direction = (0,-1,2e-16)
  Length = 5
  Length2 = 10
  Placement = pos=(0,0,0) rot=(1,0,0;1.5708rad)
  Profile = -> Sketch079
  ReferenceAxis = -> Sketch079 [N_Axis]
  Refine = true
  Suppressed = false
  Type = 0
FEATURE [PartDesign::Fillet] Fillet001
  Base = -> Pad003 [Edge16,Edge14]
  BaseFeature = -> Pad003
  Placement = pos=(0,0,0) rot=(1,0,0;1.5708rad)
  Radius = 0.4
  Refine = true
  SupportTransform = false
  Suppressed = false
  UseAllEdges = false
FEATURE [PartDesign::Body] Body005  label="pulsanti lato destro"
  AllowCompound = false
  Group = -> [Sketch078,Pad002,Sketch079,Pad003,Fillet001]
  Origin = -> Origin005
  Tip = -> Fillet001
FEATURE [Sketcher::SketchObject] Sketch080  label="lato dx pistola - fori per inserto M3 x 3 x 4.5"
  ArcFitTolerance = 1e-06
  AttachmentSupport = -> [XZ_Plane]
  ExternalGeometry = -> [Sketch075]
  FullyConstrained = true
  MakeInternals = false
  MapMode = 5
  Placement = pos=(0,0,0) rot=(1,0,0;1.5708rad)
  sketch-geometry (4):
    g0: Circle CenterX=-18.6 CenterY=12.1 CenterZ=0 NormalX=0 NormalY=0 NormalZ=1 AngleXU=0 Radius=2.25
    g1: Circle CenterX=-18.6 CenterY=30.3 CenterZ=0 NormalX=0 NormalY=0 NormalZ=1 AngleXU=0 Radius=2.25
    g2: Circle CenterX=-43.2 CenterY=30.3 CenterZ=0 NormalX=0 NormalY=0 NormalZ=1 AngleXU=0 Radius=2.25
    g3: Circle CenterX=-43.2 CenterY=12.1 CenterZ=0 NormalX=0 NormalY=0 NormalZ=1 AngleXU=0 Radius=2.25
  constraints (8):
    c: Diameter(g0) = 4.5
    c: Coincident(g0,g-5)
    c: Diameter(g1) = 4.5
    c: Coincident(g1,g-4)
    c: Diameter(g2) = 4.5
    c: Coincident(g2,g-3)
    c: Diameter(g3) = 4.5
    c: Coincident(g3,g-6)
FEATURE [Sketcher::SketchObject] Sketch081  label="lato dx pistola - pieno per inserto M3 x 3 x 4,5"
  ArcFitTolerance = 1e-06
  AttachmentSupport = -> [XZ_Plane]
  ExternalGeometry = -> [Sketch075]
  FullyConstrained = true
  MakeInternals = false
  MapMode = 5
  Placement = pos=(0,0,0) rot=(1,0,0;1.5708rad)
  sketch-geometry (4):
    g0: Circle CenterX=-43.2 CenterY=30.3 CenterZ=0 NormalX=0 NormalY=0 NormalZ=1 AngleXU=0 Radius=3.4
    g1: Circle CenterX=-18.6 CenterY=30.3 CenterZ=0 NormalX=0 NormalY=0 NormalZ=1 AngleXU=0 Radius=3.4
    g2: Circle CenterX=-43.2 CenterY=12.1 CenterZ=0 NormalX=0 NormalY=0 NormalZ=1 AngleXU=0 Radius=3.4
    g3: Circle CenterX=-18.6 CenterY=12.1 CenterZ=0 NormalX=0 NormalY=0 NormalZ=1 AngleXU=0 Radius=3.4
  constraints (8):
    c: Diameter(g0) = 6.8
    c: Coincident(g0,g-6)
    c: Diameter(g1) = 6.8
    c: Coincident(g1,g-3)
    c: Diameter(g2) = 6.8
    c: Coincident(g2,g-5)
    c: Diameter(g3) = 6.8
    c: Coincident(g3,g-4)
FEATURE [Part::Extrusion] Extrude080  label="Extrude lato dx pistola - pieno per inserto M3 x 3 x 4,5"
  Base = -> Sketch081
  Dir = (0,-1,2e-16)
  DirMode = 2
  FaceMakerClass = Part::FaceMakerBullseye
  FaceMakerMode = 3
  LengthFwd = -2.4
  LengthRev = 0
  Solid = true
  Symmetric = false
FEATURE [Part::MultiFuse] Fusion004
  Refine = true
  Shapes = -> [Cut045,Extrude080]
FEATURE [Part::Extrusion] Extrude081  label="Extrude lato dx pistola - fori per inserto M3 x 3 x 4.5"
  Base = -> Sketch080
  Dir = (0,-1,2e-16)
  DirMode = 2
  FaceMakerClass = Part::FaceMakerBullseye
  FaceMakerMode = 3
  LengthFwd = 0.6
  LengthRev = 2.4
  Solid = true
  Symmetric = false
FEATURE [Part::Cut] Cut046
  Base = -> Fusion004
  Refine = true
  Tool = -> Extrude081
FEATURE [Sketcher::SketchObject] Sketch082  label="lato sx pistola - disegno anteriore"
  ArcFitTolerance = 1e-06
  AttachmentSupport = -> [XZ_Plane]
  ExternalGeometry = -> [Sketch074]
  FullyConstrained = true
  MakeInternals = false
  MapMode = 5
  Placement = pos=(0,0,0) rot=(1,0,0;1.5708rad)
  sketch-geometry (12):
    g0: ArcOfCircle CenterX=-65 CenterY=21.2 CenterZ=0 NormalX=0 NormalY=0 NormalZ=1 AngleXU=0 Radius=10 StartAngle=1.5708 EndAngle=4.71239
    g1: ArcOfCircle CenterX=-19 CenterY=21.2 CenterZ=0 NormalX=0 NormalY=0 NormalZ=1 AngleXU=0 Radius=10 StartAngle=4.71239 EndAngle=7.85398
    g2: LineSegment StartX=-65 StartY=31.2 StartZ=0 EndX=-19 EndY=31.2 EndZ=0
    g3: LineSegment StartX=-65 StartY=11.2 StartZ=0 EndX=-19 EndY=11.2 EndZ=0
    g4: LineSegment StartX=-82.8 StartY=3.2 StartZ=0 EndX=0 EndY=3.2 EndZ=0
    g5: LineSegment StartX=0 StartY=3.2 StartZ=0 EndX=0 EndY=39.2 EndZ=0
    g6: LineSegment StartX=0 StartY=39.2 StartZ=0 EndX=-82.8 EndY=39.2 EndZ=0
    g7: LineSegment StartX=-82.8 StartY=39.2 StartZ=0 EndX=-82.8 EndY=3.2 EndZ=0
    g8: Circle CenterX=-78.51 CenterY=34.8 CenterZ=0 NormalX=0 NormalY=0 NormalZ=1 AngleXU=0 Radius=1.8
    g9: Circle CenterX=-5.6 CenterY=34.8 CenterZ=0 NormalX=0 NormalY=0 NormalZ=1 AngleXU=0 Radius=1.8
    g10: Circle CenterX=-5.6 CenterY=7.6 CenterZ=0 NormalX=0 NormalY=0 NormalZ=1 AngleXU=0 Radius=1.8
    g11: Circle CenterX=-78.51 CenterY=7.6 CenterZ=0 NormalX=0 NormalY=0 NormalZ=1 AngleXU=0 Radius=1.8
  constraints (26):
    c: Tangent(g0,g2) = 1.5708
    c: Tangent(g0,g3) = -1.5708
    c: Tangent(g1,g2) = 1.5708
    c: Tangent(g1,g3) = -1.5708
    c: Equal(g0,g1)
    c: Coincident(g4,g5)
    c: Coincident(g5,g6)
    c: Coincident(g6,g7)
    c: Coincident(g7,g4)
    c: Horizontal(g4)
    c: Horizontal(g6)
    c: Vertical(g5)
    c: Vertical(g7)
    c: Coincident(g4,g-7)
    c: Coincident(g5,g-9)
    c: Diameter(g1) = 20
    c: Coincident(g1,g-5)
    c: Coincident(g0,g-4)
    c: Equal(g9,g-11)
    c: Equal(g10,g-12)
    c: Equal(g11,g-13)
    c: Equal(g8,g-10)
    c: Coincident(g8,g-10)
    c: Coincident(g11,g-13)
    c: Coincident(g10,g-12)
    c: Coincident(g9,g-11)
FEATURE [Sketcher::SketchObject] Sketch083  label="lato dx pistola - disegno anteriore"
  ArcFitTolerance = 1e-06
  AttachmentSupport = -> [XZ_Plane]
  ExternalGeometry = -> [Sketch082]
  FullyConstrained = true
  MakeInternals = false
  MapMode = 5
  Placement = pos=(0,0,0) rot=(1,0,0;1.5708rad)
  sketch-geometry (12):
    g0: LineSegment StartX=-82.8 StartY=3.2 StartZ=0 EndX=0 EndY=3.2 EndZ=0
    g1: LineSegment StartX=0 StartY=3.2 StartZ=0 EndX=0 EndY=39.2 EndZ=0
    g2: LineSegment StartX=0 StartY=39.2 StartZ=0 EndX=-82.8 EndY=39.2 EndZ=0
    g3: LineSegment StartX=-82.8 StartY=39.2 StartZ=0 EndX=-82.8 EndY=3.2 EndZ=0
    g4: ArcOfCircle CenterX=-65 CenterY=21.2 CenterZ=0 NormalX=0 NormalY=0 NormalZ=1 AngleXU=0 Radius=10 StartAngle=1.5708 EndAngle=4.71239
    g5: ArcOfCircle CenterX=-19 CenterY=21.2 CenterZ=0 NormalX=0 NormalY=0 NormalZ=1 AngleXU=0 Radius=10 StartAngle=4.71239 EndAngle=7.85398
    g6: LineSegment StartX=-65 StartY=31.2 StartZ=0 EndX=-19 EndY=31.2 EndZ=0
    g7: LineSegment StartX=-65 StartY=11.2 StartZ=0 EndX=-19 EndY=11.2 EndZ=0
    g8: Circle CenterX=-78.51 CenterY=34.8 CenterZ=0 NormalX=0 NormalY=0 NormalZ=1 AngleXU=0 Radius=1.8
    g9: Circle CenterX=-5.6 CenterY=34.8 CenterZ=0 NormalX=0 NormalY=0 NormalZ=1 AngleXU=0 Radius=1.8
    g10: Circle CenterX=-5.6 CenterY=7.6 CenterZ=0 NormalX=0 NormalY=0 NormalZ=1 AngleXU=0 Radius=1.8
    g11: Circle CenterX=-78.51 CenterY=7.6 CenterZ=0 NormalX=0 NormalY=0 NormalZ=1 AngleXU=0 Radius=1.8
  constraints (26):
    c: Coincident(g0,g1)
    c: Coincident(g1,g2)
    c: Coincident(g2,g3)
    c: Coincident(g3,g0)
    c: Horizontal(g0)
    c: Horizontal(g2)
    c: Vertical(g1)
    c: Vertical(g3)
    c: Coincident(g0,g-5)
    c: Coincident(g1,g-6)
    c: Tangent(g4,g6) = 1.5708
    c: Tangent(g4,g7) = -1.5708
    c: Tangent(g5,g6) = 1.5708
    c: Tangent(g5,g7) = -1.5708
    c: Equal(g4,g5)
    c: Equal(g5,g-9)
    c: Coincident(g5,g-9)
    c: Coincident(g4,g-8)
    c: Equal(g8,g-11)
    c: Equal(g11,g-12)
    c: Equal(g10,g-13)
    c: Equal(g9,g-14)
    c: Coincident(g9,g-14)
    c: Coincident(g10,g-13)
    c: Coincident(g11,g-12)
    c: Coincident(g8,g-11)
FEATURE [Sketcher::SketchObject] Sketch084  label="lato sx pistola - spazi anteriori per viti"
  ArcFitTolerance = 1e-06
  AttachmentSupport = -> [XZ_Plane]
  ExternalGeometry = -> [Sketch082]
  FullyConstrained = true
  MakeInternals = false
  MapMode = 5
  Placement = pos=(0,0,0) rot=(1,0,0;1.5708rad)
  sketch-geometry (24):
    g0: ArcOfCircle CenterX=-78.51 CenterY=34.8 CenterZ=0 NormalX=0 NormalY=0 NormalZ=1 AngleXU=0 Radius=3.5 StartAngle=4.71239 EndAngle=6.28319
    g1: ArcOfCircle CenterX=-5.6 CenterY=34.8 CenterZ=0 NormalX=0 NormalY=0 NormalZ=1 AngleXU=0 Radius=3.5 StartAngle=3.14159 EndAngle=4.71239
    g2: ArcOfCircle CenterX=-78.51 CenterY=7.6 CenterZ=0 NormalX=0 NormalY=0 NormalZ=1 AngleXU=0 Radius=3.5 StartAngle=3.99598e-11 EndAngle=1.5708
    g3: ArcOfCircle CenterX=-5.6 CenterY=7.6 CenterZ=0 NormalX=0 NormalY=0 NormalZ=1 AngleXU=0 Radius=3.5 StartAngle=1.5708 EndAngle=3.14159
    g4: LineSegment StartX=0 StartY=11.1 StartZ=0 EndX=-5.6 EndY=11.1 EndZ=0
    g5: LineSegment StartX=-9.1 StartY=7.6 StartZ=0 EndX=-9.1 EndY=3.2 EndZ=0
    g6: LineSegment StartX=-75.01 StartY=39.2 StartZ=0 EndX=-75.01 EndY=34.8 EndZ=0
    g7: LineSegment StartX=-82.8 StartY=31.3 StartZ=0 EndX=-78.51 EndY=31.3 EndZ=0
    g8: LineSegment StartX=-82.8 StartY=11.1 StartZ=0 EndX=-78.51 EndY=11.1 EndZ=0
    g9: LineSegment StartX=-75.01 StartY=7.6 StartZ=0 EndX=-75.01 EndY=3.2 EndZ=0
    g10: LineSegment StartX=-9.1 StartY=39.2 StartZ=0 EndX=-9.1 EndY=34.8 EndZ=0
    g11: LineSegment StartX=-5.6 StartY=31.3 StartZ=0 EndX=0 EndY=31.3 EndZ=0
    g12: LineSegment StartX=-9.1 StartY=39.2 StartZ=0 EndX=0 EndY=39.2 EndZ=0
    g13: LineSegment StartX=0 StartY=39.2 StartZ=0 EndX=0 EndY=31.3 EndZ=0
    g14: LineSegment StartX=0 StartY=11.1 StartZ=0 EndX=0 EndY=3.2 EndZ=0
    g15: LineSegment StartX=0 StartY=3.2 StartZ=0 EndX=-9.1 EndY=3.2 EndZ=0
    g16: LineSegment StartX=-75.01 StartY=3.2 StartZ=0 EndX=-82.8 EndY=3.2 EndZ=0
    g17: LineSegment StartX=-82.8 StartY=3.2 StartZ=0 EndX=-82.8 EndY=11.1 EndZ=0
    g18: LineSegment StartX=-82.8 StartY=31.3 StartZ=0 EndX=-82.8 EndY=39.2 EndZ=0
    g19: LineSegment StartX=-82.8 StartY=39.2 StartZ=0 EndX=-75.01 EndY=39.2 EndZ=0
    g20: Circle CenterX=-78.51 CenterY=34.8 CenterZ=0 NormalX=0 NormalY=0 NormalZ=1 AngleXU=0 Radius=1.8
    g21: Circle CenterX=-5.6 CenterY=34.8 CenterZ=0 NormalX=0 NormalY=0 NormalZ=1 AngleXU=0 Radius=1.8
    g22: Circle CenterX=-5.6 CenterY=7.6 CenterZ=0 NormalX=0 NormalY=0 NormalZ=1 AngleXU=0 Radius=1.8
    g23: Circle CenterX=-78.51 CenterY=7.6 CenterZ=0 NormalX=0 NormalY=0 NormalZ=1 AngleXU=0 Radius=1.8
  constraints (56):
    c: Radius(g0) = 3.5
    c: Coincident(g0,g-5)
    c: Radius(g1) = 3.5
    c: Coincident(g1,g-10)
    c: Radius(g2) = 3.5
    c: Coincident(g2,g-4)
    c: Radius(g3) = 3.5
    c: Coincident(g3,g-9)
    c: Horizontal(g4)
    c: Vertical(g5)
    c: Vertical(g6)
    c: Horizontal(g7)
    c: Horizontal(g8)
    c: Vertical(g9)
    c: Vertical(g10)
    c: Horizontal(g11)
    c: Tangent(g11,g1) = -1.5708
    c: Tangent(g1,g10) = -1.5708
    c: Tangent(g3,g5) = -1.5708
    c: Tangent(g3,g4) = -1.5708
    c: Tangent(g9,g2) = 1.5708
    c: Tangent(g8,g2) = 1.5708
    c: Tangent(g7,g0) = -1.5708
    c: Tangent(g0,g6) = 1.5708
    c: PointOnObject(g10,g-7)
    c: PointOnObject(g11,g-11)
    c: PointOnObject(g4,g-11)
    c: PointOnObject(g5,g-8)
    c: PointOnObject(g9,g-8)
    c: PointOnObject(g8,g-6)
    c: PointOnObject(g7,g-6)
    c: PointOnObject(g6,g-7)
    c: Coincident(g12,g10)
    c: Coincident(g12,g-11)
    c: Coincident(g13,g12)
    c: Coincident(g13,g11)
    c: Coincident(g14,g4)
    c: Coincident(g14,g-11)
    c: Coincident(g15,g14)
    c: Coincident(g15,g5)
    c: Coincident(g16,g9)
    c: Coincident(g16,g-8)
    c: Coincident(g17,g16)
    c: Coincident(g17,g8)
    c: Coincident(g18,g7)
    c: Coincident(g18,g-7)
    c: Coincident(g19,g18)
    c: Coincident(g19,g6)
    c: Equal(g21,g-10)
    c: Equal(g-9,g22)
    c: Equal(g23,g-4)
    c: Equal(g20,g-5)
    c: Coincident(g20,g0)
    c: Coincident(g21,g1)
    c: Coincident(g22,g3)
    c: Coincident(g23,g2)
FEATURE [Sketcher::SketchObject] Sketch085  label="lato dx pistola - spazi anteriori per viti"
  ArcFitTolerance = 1e-06
  AttachmentSupport = -> [XZ_Plane]
  ExternalGeometry = -> [Sketch083]
  FullyConstrained = true
  MakeInternals = false
  MapMode = 5
  Placement = pos=(0,0,0) rot=(1,0,0;1.5708rad)
  sketch-geometry (24):
    g0: ArcOfCircle CenterX=-78.51 CenterY=34.8 CenterZ=0 NormalX=0 NormalY=0 NormalZ=1 AngleXU=0 Radius=3.5 StartAngle=4.71239 EndAngle=6.28319
    g1: ArcOfCircle CenterX=-5.6 CenterY=34.8 CenterZ=0 NormalX=0 NormalY=0 NormalZ=1 AngleXU=0 Radius=3.5 StartAngle=3.14159 EndAngle=4.71239
    g2: ArcOfCircle CenterX=-78.51 CenterY=7.6 CenterZ=0 NormalX=0 NormalY=0 NormalZ=1 AngleXU=0 Radius=3.5 StartAngle=3.99599e-11 EndAngle=1.5708
    g3: ArcOfCircle CenterX=-5.6 CenterY=7.6 CenterZ=0 NormalX=0 NormalY=0 NormalZ=1 AngleXU=0 Radius=3.5 StartAngle=1.5708 EndAngle=3.14159
    g4: LineSegment StartX=-9.1 StartY=39.2 StartZ=0 EndX=-9.1 EndY=34.8 EndZ=0
    g5: LineSegment StartX=-5.6 StartY=31.3 StartZ=0 EndX=0 EndY=31.3 EndZ=0
    g6: LineSegment StartX=-5.6 StartY=11.1 StartZ=0 EndX=0 EndY=11.1 EndZ=0
    g7: LineSegment StartX=-9.1 StartY=7.6 StartZ=0 EndX=-9.1 EndY=3.2 EndZ=0
    g8: LineSegment StartX=-82.8 StartY=11.1 StartZ=0 EndX=-78.51 EndY=11.1 EndZ=0
    g9: LineSegment StartX=-75.01 StartY=7.6 StartZ=0 EndX=-75.01 EndY=3.2 EndZ=0
    g10: LineSegment StartX=-82.8 StartY=31.3 StartZ=0 EndX=-78.51 EndY=31.3 EndZ=0
    g11: LineSegment StartX=-75.01 StartY=34.8 StartZ=0 EndX=-75.01 EndY=39.2 EndZ=0
    g12: LineSegment StartX=-75.01 StartY=3.2 StartZ=0 EndX=-82.8 EndY=3.2 EndZ=0
    g13: LineSegment StartX=-82.8 StartY=3.2 StartZ=0 EndX=-82.8 EndY=11.1 EndZ=0
    g14: LineSegment StartX=-82.8 StartY=31.3 StartZ=0 EndX=-82.8 EndY=39.2 EndZ=0
    g15: LineSegment StartX=-82.8 StartY=39.2 StartZ=0 EndX=-75.01 EndY=39.2 EndZ=0
    g16: LineSegment StartX=-9.1 StartY=39.2 StartZ=0 EndX=0 EndY=39.2 EndZ=0
    g17: LineSegment StartX=0 StartY=39.2 StartZ=0 EndX=0 EndY=31.3 EndZ=0
    g18: LineSegment StartX=-9.1 StartY=3.2 StartZ=0 EndX=0 EndY=3.2 EndZ=0
    g19: LineSegment StartX=0 StartY=3.2 StartZ=0 EndX=0 EndY=11.1 EndZ=0
    g20: Circle CenterX=-78.51 CenterY=34.8 CenterZ=0 NormalX=0 NormalY=0 NormalZ=1 AngleXU=0 Radius=1.8
    g21: Circle CenterX=-5.6 CenterY=34.8 CenterZ=0 NormalX=0 NormalY=0 NormalZ=1 AngleXU=0 Radius=1.8
    g22: Circle CenterX=-5.6 CenterY=7.6 CenterZ=0 NormalX=0 NormalY=0 NormalZ=1 AngleXU=0 Radius=1.8
    g23: Circle CenterX=-78.51 CenterY=7.6 CenterZ=0 NormalX=0 NormalY=0 NormalZ=1 AngleXU=0 Radius=1.8
  constraints (56):
    c: Radius(g0) = 3.5
    c: Coincident(g0,g-3)
    c: Radius(g1) = 3.5
    c: Coincident(g1,g-5)
    c: Radius(g2) = 3.5
    c: Coincident(g2,g-4)
    c: Radius(g3) = 3.5
    c: Coincident(g3,g-6)
    c: Vertical(g4)
    c: Horizontal(g5)
    c: Horizontal(g6)
    c: Vertical(g7)
    c: Horizontal(g8)
    c: Vertical(g9)
    c: Horizontal(g10)
    c: Vertical(g11)
    c: Tangent(g4,g1) = -1.5708
    c: Tangent(g5,g1) = -1.5708
    c: Tangent(g6,g3) = 1.5708
    c: Tangent(g7,g3) = -1.5708
    c: Tangent(g9,g2) = 1.5708
    c: Tangent(g8,g2) = 1.5708
    c: Tangent(g10,g0) = -1.5708
    c: Tangent(g11,g0) = -1.5708
    c: PointOnObject(g11,g-9)
    c: PointOnObject(g4,g-9)
    c: PointOnObject(g5,g-10)
    c: PointOnObject(g6,g-10)
    c: PointOnObject(g7,g-7)
    c: PointOnObject(g9,g-7)
    c: PointOnObject(g8,g-8)
    c: PointOnObject(g10,g-8)
    c: Coincident(g12,g9)
    c: Coincident(g12,g-8)
    c: Coincident(g13,g12)
    c: Coincident(g13,g8)
    c: Coincident(g14,g10)
    c: Coincident(g14,g-9)
    c: Coincident(g15,g14)
    c: Coincident(g15,g11)
    c: Coincident(g16,g4)
    c: Coincident(g16,g-10)
    c: Coincident(g17,g16)
    c: Coincident(g17,g5)
    c: Coincident(g18,g7)
    c: Coincident(g18,g-10)
    c: Coincident(g19,g18)
    c: Coincident(g19,g6)
    c: Equal(g20,g-3)
    c: Equal(g21,g-5)
    c: Equal(g22,g-6)
    c: Equal(g23,g-4)
    c: Coincident(g20,g0)
    c: Coincident(g21,g1)
    c: Coincident(g22,g3)
    c: Coincident(g23,g2)
FEATURE [Part::Extrusion] Extrude082  label="Extrude lato sx pistola - disegno anteriore"
  Base = -> Sketch082
  Dir = (0,-1,2e-16)
  DirMode = 2
  FaceMakerClass = Part::FaceMakerBullseye
  FaceMakerMode = 3
  LengthFwd = -1.6
  LengthRev = 0
  Placement = pos=(0,2,0) rot=(0,0,1;0rad)
  Solid = true
  Symmetric = false
FEATURE [Part::Extrusion] Extrude083  label="Extrude lato dx pistola - disegno anteriore"
  Base = -> Sketch083
  Dir = (0,-1,2e-16)
  DirMode = 2
  FaceMakerClass = Part::FaceMakerBullseye
  FaceMakerMode = 3
  LengthFwd = 1.6
  LengthRev = 0
  Placement = pos=(0,-2,0) rot=(0,0,1;0rad)
  Solid = true
  Symmetric = false
FEATURE [Part::Extrusion] Extrude084  label="Extrude lato sx pistola - spazi anteriori per viti"
  Base = -> Sketch084
  Dir = (0,-1,2e-16)
  DirMode = 2
  FaceMakerClass = Part::FaceMakerBullseye
  FaceMakerMode = 3
  LengthFwd = -1.6
  LengthRev = 0
  Placement = pos=(0,2,0) rot=(0,0,1;0rad)
  Solid = true
  Symmetric = false
FEATURE [Part::Extrusion] Extrude085  label="Extrude lato dx pistola - spazi anteriori per viti"
  Base = -> Sketch085
  Dir = (0,-1,2e-16)
  DirMode = 2
  FaceMakerClass = Part::FaceMakerBullseye
  FaceMakerMode = 3
  LengthFwd = 0.8
  LengthRev = 0
  Placement = pos=(0,-2.8,0) rot=(0,0,1;0rad)
  Solid = true
  Symmetric = false
FEATURE [Part::Cut] Cut048  label="Extrude lato dx pistola - disegno anterioro con fori viti"
  Base = -> Extrude083
  Refine = true
  Tool = -> Extrude085
FEATURE [Part::MultiFuse] Fusion006
  Refine = true
  Shapes = -> [Cut046,Cut048]
FEATURE [Sketcher::SketchObject] Sketch087  label="lato sx pistola - rialzo posteriore"
  ArcFitTolerance = 1e-06
  AttachmentSupport = -> [XZ_Plane]
  ExternalGeometry = -> [Sketch074]
  FullyConstrained = true
  MakeInternals = false
  MapMode = 5
  Placement = pos=(0,0,0) rot=(1,0,0;1.5708rad)
  sketch-geometry (10):
    g0: LineSegment StartX=-181.33 StartY=20.0744 StartZ=0 EndX=-144.029 EndY=20.0744 EndZ=0
    g1: LineSegment StartX=-137.815 StartY=39.2 StartZ=0 EndX=-144.029 EndY=20.0744 EndZ=0
    g2: LineSegment StartX=-178.754 StartY=39.2 StartZ=0 EndX=-137.815 EndY=39.2 EndZ=0
    g3: ArcOfCircle CenterX=-184.08 CenterY=34.8 CenterZ=0 NormalX=0 NormalY=0 NormalZ=1 AngleXU=0 Radius=3.5 StartAngle=4.71239 EndAngle=5.93412
    g4: LineSegment StartX=-178.754 StartY=39.2 StartZ=0 EndX=-180.791 EndY=33.6029 EndZ=0
    g5: GeomPoint [constr] X=-181.33 Y=20.0744 Z=0
    g6: LineSegment [constr] StartX=-181.33 StartY=20.0744 StartZ=0 EndX=-192.176 EndY=-3.18451 EndZ=0
    g7: LineSegment StartX=-184.08 StartY=31.3 StartZ=0 EndX=-186.139 EndY=31.3 EndZ=0
    g8: LineSegment StartX=-186.139 StartY=31.3 StartZ=0 EndX=-190.224 EndY=20.0744 EndZ=0
    g9: LineSegment StartX=-181.33 StartY=20.0744 StartZ=0 EndX=-190.224 EndY=20.0744 EndZ=0
  constraints (23):
    c: Horizontal(g0)
    c: Tangent(g1,g-5)
    c: PointOnObject(g2,g-4)
    c: Coincident(g2,g1)
    c: Radius(g3) = 3.5
    c: Coincident(g3,g-10)
    c: Horizontal(g2)
    c: Equal(g1,g-3)
    c: Coincident(g0,g1)
    c: Tangent(g4,g3) = 1.5708
    c: Coincident(g4,g2)
    c: Coincident(g6,g5)
    c: Tangent(g6,g-11) = -1.5708
    c: Coincident(g0,g5)
    c: Parallel(g4,g-3)
    c: Horizontal(g7)
    c: Parallel(g8,g-3)
    c: Tangent(g3,g7) = 1.5708
    c: Coincident(g8,g7)
    c: Coincident(g9,g0)
    c: Horizontal(g9)
    c: Coincident(g9,g8)
    c: DistanceX(g-8,g7) = 3.8
FEATURE [Sketcher::SketchObject] Sketch086  label="lato sx pistola - rialzo centrale"
  ArcFitTolerance = 1e-06
  AttachmentOffset = pos=(0,2,0) rot=(0,0,1;0rad)
  AttachmentSupport = -> [XZ_Plane]
  ExternalGeometry = -> [Sketch074,Sketch087]
  FullyConstrained = true
  MakeInternals = false
  MapMode = 5
  Placement = pos=(0,4e-16,2) rot=(1,0,0;1.5708rad)
  sketch-geometry (6):
    g0: LineSegment StartX=-137.815 StartY=37.2 StartZ=0 EndX=-142.793 EndY=21.8787 EndZ=0
    g1: LineSegment StartX=-137.815 StartY=37.2 StartZ=0 EndX=-110.815 EndY=37.2 EndZ=0
    g2: LineSegment StartX=-110.815 StartY=37.2 StartZ=0 EndX=-112.201 EndY=32.9344 EndZ=0
    g3: LineSegment StartX=-127.418 StartY=21.8787 StartZ=0 EndX=-142.793 EndY=21.8787 EndZ=0
    g4: ArcOfCircle CenterX=-127.418 CenterY=37.8787 CenterZ=0 NormalX=0 NormalY=0 NormalZ=1 AngleXU=0 Radius=16 StartAngle=4.71239 EndAngle=5.96903
    g5: GeomPoint [constr] X=-115.793 Y=21.8787 Z=0
  constraints (15):
    c: Distance(g1) = 27
    c: Coincident(g1,g0)
    c: PointOnObject(g1,g-4)
    c: Parallel(g2,g-3)
    c: Coincident(g2,g1)
    c: Horizontal(g3)
    c: PointOnObject(g5,g2)
    c: PointOnObject(g5,g3)
    c: Tangent(g2,g4) = 1.5708
    c: Tangent(g3,g4) = 1.5708
    c: Radius(g4) = 16
    c: Parallel(g0,g-7)
    c: Coincident(g0,g-7)
    c: Coincident(g0,g3)
    c: Distance(g0,g-7) = 4
FEATURE [Sketcher::SketchObject] Sketch088  label="lato sx pistola - rialzo impugnatura"
  ArcFitTolerance = 1e-06
  AttachmentSupport = -> [XZ_Plane]
  ExternalGeometry = -> [Sketch074,Sketch087]
  FullyConstrained = true
  MakeInternals = false
  MapMode = 5
  Placement = pos=(0,0,0) rot=(1,0,0;1.5708rad)
  sketch-geometry (11):
    g0: LineSegment StartX=-144.029 StartY=20.0744 StartZ=0 EndX=-176.685 EndY=-80.4316 EndZ=0
    g1: Circle CenterX=-213.443 CenterY=-76.8316 CenterZ=0 NormalX=0 NormalY=0 NormalZ=1 AngleXU=0 Radius=3
    g2: Circle CenterX=-179.305 CenterY=-76.8316 CenterZ=0 NormalX=0 NormalY=0 NormalZ=1 AngleXU=0 Radius=3
    g3: LineSegment StartX=-176.685 StartY=-80.4316 StartZ=0 EndX=-215.932 EndY=-80.4316 EndZ=0
    g4: LineSegment StartX=-192.176 StartY=-3.18451 StartZ=0 EndX=-215.42 EndY=-53.0314 EndZ=0
    g5: ArcOfCircle CenterX=-184.801 CenterY=-67.3089 CenterZ=0 NormalX=0 NormalY=0 NormalZ=1 AngleXU=0 Radius=33.7833 StartAngle=2.70526 EndAngle=3.54053
    g6: LineSegment [constr] StartX=-192.176 StartY=-3.18451 StartZ=0 EndX=-181.33 EndY=20.0744 EndZ=0
    g7: LineSegment StartX=-144.029 StartY=20.0744 StartZ=0 EndX=-190.224 EndY=20.0744 EndZ=0
    g8: LineSegment StartX=-190.224 StartY=20.0744 StartZ=0 EndX=-191.316 EndY=17.0744 EndZ=0
    g9: LineSegment StartX=-191.316 StartY=17.0744 StartZ=0 EndX=-182.729 EndY=17.0744 EndZ=0
    g10: LineSegment StartX=-192.176 StartY=-3.18451 StartZ=0 EndX=-182.729 EndY=17.0744 EndZ=0
  constraints (26):
    c: Coincident(g0,g-5)
    c: Coincident(g2,g-10)
    c: Coincident(g1,g-9)
    c: Diameter(g2) = 6
    c: Diameter(g1) = 6
    c: Coincident(g3,g0)
    c: Coincident(g3,g-4)
    c: Equal(g4,g-15)
    c: Parallel(g4,g-15)
    c: Coincident(g4,g-15)
    c: Coincident(g5,g4)
    c: Coincident(g5,g3)
    c: Tangent(g6,g4) = 1.5708
    c: PointOnObject(g6,g-13)
    c: Coincident(g0,g-13)
    c: Coincident(g7,g0)
    c: Coincident(g7,g-14)
    c: Coincident(g8,g7)
    c: Coincident(g9,g8)
    c: Horizontal(g9)
    c: PointOnObject(g9,g6)
    c: Coincident(g10,g4)
    c: Coincident(g10,g9)
    c: DistanceY(g8,g8) = 3
    c: Parallel(g8,g-16)
    c: Tangent(g5,g-3)
FEATURE [Sketcher::SketchObject] Sketch089  label="lato sx pistola - disegno centrale"
  ArcFitTolerance = 1e-06
  AttachmentSupport = -> [XZ_Plane]
  ExternalGeometry = -> [Sketch086]
  FullyConstrained = true
  MakeInternals = false
  MapMode = 5
  Placement = pos=(0,0,0) rot=(1,0,0;1.5708rad)
  sketch-geometry (4):
    g0: LineSegment StartX=-130.215 StartY=39.2 StartZ=0 EndX=-119.215 EndY=39.2 EndZ=0
    g1: LineSegment StartX=-130.215 StartY=39.2 StartZ=0 EndX=-132.81 EndY=31.2111 EndZ=0
    g2: LineSegment StartX=-119.215 StartY=39.2 StartZ=0 EndX=-121.81 EndY=31.2111 EndZ=0
    g3: LineSegment StartX=-132.81 StartY=31.2111 StartZ=0 EndX=-121.81 EndY=31.2111 EndZ=0
  constraints (11):
    c: Horizontal(g3)
    c: Parallel(g2,g-4)
    c: Parallel(g1,g-4)
    c: Distance(g1) = 8.4
    c: DistanceX(g0,g0) = 11
    c: Tangent(g0,g-3)
    c: Coincident(g1,g0)
    c: Coincident(g2,g0)
    c: Coincident(g3,g1)
    c: Coincident(g3,g2)
    c: DistanceX(g0,g-4) = 8.4
FEATURE [Sketcher::SketchObject] Sketch090  label="lato sx pistola - disegno pre centrale"
  ArcFitTolerance = 1e-06
  AttachmentSupport = -> [XZ_Plane]
  ExternalGeometry = -> [Sketch074,Sketch086]
  FullyConstrained = true
  MakeInternals = false
  MapMode = 5
  Placement = pos=(0,0,0) rot=(1,0,0;1.5708rad)
  sketch-geometry (4):
    g0: LineSegment StartX=-106.615 StartY=36.8 StartZ=0 EndX=-89.6146 EndY=36.8 EndZ=0
    g1: LineSegment StartX=-110.254 StartY=26.8 StartZ=0 EndX=-89.6146 EndY=26.8 EndZ=0
    g2: LineSegment StartX=-106.615 StartY=36.8 StartZ=0 EndX=-110.254 EndY=26.8 EndZ=0
    g3: ArcOfCircle CenterX=-94.6146 CenterY=31.8 CenterZ=0 NormalX=0 NormalY=0 NormalZ=1 AngleXU=0 Radius=7.07107 StartAngle=5.49779 EndAngle=7.06858
  constraints (13):
    c: Horizontal(g0)
    c: Horizontal(g1)
    c: Parallel(g-3,g2)
    c: Coincident(g0,g2)
    c: DistanceY(g2,g2) = 10
    c: Coincident(g1,g2)
    c: DistanceX(g0,g0) = 17
    c: DistanceX(g0,g1) = 0
    c: Coincident(g3,g1)
    c: DistanceX(g-5,g0) = 4.2
    c: DistanceY(g0,g-5) = 2.4
    c: Coincident(g3,g0)
    c: DistanceX(g3,g0) = 5
FEATURE [PartDesign::Body] Body  label="Struttura pistola"
  AllowCompound = false
  Group = -> [Sketch,Sketch002,Sketch004,DatumPlane,Sketch005,DatumPlane001,CopyCut,Sketch008,Sketch009,Sketch010,Sketch011,Sketch012,Sketch013,Sketch014,Sketch015,Sketch016,Sketch017,Sketch018,Sketch019,Sketch020,Sketch022,Sketch023,Sketch024,Sketch025,Sketch026,Sketch027,Sketch029,Sketch030,Sketch031,Sketch032,Sketch033,Sketch034,Sketch035,Sketch036,Sketch037,Sketch038,Sketch039,Sketch040,Sketch041,Sketch042,+28 more]
  Origin = -> Origin
FEATURE [PartDesign::SubShapeBinder] Binder
  BindCopyOnChange = 0
  BindMode = 0
  ClaimChildren = false
  Context = -> Body006 [Binder.]
  Fuse = false
  MakeFace = true
  OffsetFill = false
  OffsetIntersection = false
  OffsetJoinType = 0
  OffsetOpenResult = false
  PartialLoad = false
  Refine = true
  Relative = true
  Support = -> [Body[Sketch074.]]
  _Version = 2
FEATURE [PartDesign::SubShapeBinder] Binder001
  BindCopyOnChange = 0
  BindMode = 0
  ClaimChildren = false
  Context = -> Body007 [Binder001.]
  Fuse = false
  MakeFace = true
  OffsetFill = false
  OffsetIntersection = false
  OffsetJoinType = 0
  OffsetOpenResult = false
  PartialLoad = false
  Refine = true
  Relative = true
  Support = -> [Body[Sketch075.]]
  _Version = 2
FEATURE [Mesh::Feature] logo_per_PCB_definitivo_positivo
  Placement = pos=(-191,17,-66) rot=(0,1,1;0rad)
FEATURE [Sketcher::SketchObject] Sketch114  label="Sketch114 - base lato DX"
  ArcFitTolerance = 1e-06
  AttachmentSupport = -> [Binder001]
  ExternalGeometry = -> [Binder001]
  FullyConstrained = true
  MakeInternals = false
  MapMode = 5
  Placement = pos=(0,1e-15,0) rot=(0,0.707107,0.707107;3.14159rad)
  sketch-geometry (30):
    g0: Circle CenterX=5.6 CenterY=34.8 CenterZ=0 NormalX=0 NormalY=0 NormalZ=1 AngleXU=0 Radius=1.8
    g1: Circle CenterX=5.6 CenterY=7.6 CenterZ=0 NormalX=0 NormalY=0 NormalZ=1 AngleXU=0 Radius=1.8
    g2: Circle CenterX=24.2 CenterY=26.7 CenterZ=0 NormalX=0 NormalY=0 NormalZ=1 AngleXU=0 Radius=3
    g3: Circle CenterX=24.2 CenterY=15.7 CenterZ=0 NormalX=0 NormalY=0 NormalZ=1 AngleXU=0 Radius=3
    g4: Circle CenterX=36.2 CenterY=21.2 CenterZ=0 NormalX=0 NormalY=0 NormalZ=1 AngleXU=0 Radius=2.8
    g5: Circle CenterX=78.51 CenterY=34.8 CenterZ=0 NormalX=0 NormalY=0 NormalZ=1 AngleXU=0 Radius=1.8
    g6: Circle CenterX=78.51 CenterY=7.6 CenterZ=0 NormalX=0 NormalY=0 NormalZ=1 AngleXU=0 Radius=1.8
    g7: Circle CenterX=184.08 CenterY=34.8 CenterZ=0 NormalX=0 NormalY=0 NormalZ=1 AngleXU=0 Radius=1.8
    g8: Circle CenterX=213.443 CenterY=-76.8316 CenterZ=0 NormalX=0 NormalY=0 NormalZ=1 AngleXU=0 Radius=1.8
    g9: Circle CenterX=179.305 CenterY=-76.8316 CenterZ=0 NormalX=0 NormalY=0 NormalZ=1 AngleXU=0 Radius=1.8
    g10: ArcOfCircle [constr] CenterX=132.428 CenterY=4 CenterZ=0 NormalX=0 NormalY=0 NormalZ=1 AngleXU=0 Radius=16 StartAngle=0.314159 EndAngle=1.5708
    g11: ArcOfCircle CenterX=107.6 CenterY=4 CenterZ=0 NormalX=0 NormalY=0 NormalZ=1 AngleXU=0 Radius=16 StartAngle=1.5708 EndAngle=3.00366
    g12: ArcOfCircle CenterX=207.583 CenterY=4 CenterZ=0 NormalX=0 NormalY=0 NormalZ=1 AngleXU=0 Radius=17 StartAngle=1.85815 EndAngle=3.57792
    g13: ArcOfCircle CenterX=184.801 CenterY=-67.3089 CenterZ=0 NormalX=0 NormalY=0 NormalZ=1 AngleXU=0 Radius=33.7833 StartAngle=5.88425 EndAngle=6.71952
    g14: LineSegment StartX=0 StartY=39.2 StartZ=0 EndX=0 EndY=3.2 EndZ=0
    g15: LineSegment StartX=0 StartY=3.2 StartZ=0 EndX=82.8 EndY=3.2 EndZ=0
    g16: LineSegment StartX=82.8 StartY=3.2 StartZ=0 EndX=82.8 EndY=6.2 EndZ=0
    g17: LineSegment StartX=82.8 StartY=6.2 StartZ=0 EndX=91.752 EndY=6.2 EndZ=0
    g18: LineSegment StartX=107.6 StartY=20 StartZ=0 EndX=132.428 EndY=20 EndZ=0
    g19: LineSegment StartX=147.645 StartY=8.94427 StartZ=0 EndX=176.685 EndY=-80.4316 EndZ=0
    g20: LineSegment StartX=176.685 StartY=-80.4316 StartZ=0 EndX=215.932 EndY=-80.4316 EndZ=0
    g21: LineSegment StartX=215.42 StartY=-53.0314 StartZ=0 EndX=192.176 EndY=-3.18451 EndZ=0
    g22: LineSegment StartX=202.765 StartY=20.303 StartZ=0 EndX=195.887 EndY=39.2 EndZ=0
    g23: LineSegment StartX=195.887 StartY=39.2 StartZ=0 EndX=0 EndY=39.2 EndZ=0
    g24: LineSegment StartX=196.467 StartY=26.4942 StartZ=0 EndX=194.073 EndY=33.0721 EndZ=0
    g25: LineSegment StartX=194.073 StartY=33.0721 StartZ=0 EndX=189.939 EndY=31.5672 EndZ=0
    g26: LineSegment StartX=189.939 StartY=31.5672 StartZ=0 EndX=192.333 EndY=24.9893 EndZ=0
    g27: LineSegment StartX=192.333 StartY=24.9893 StartZ=0 EndX=196.467 EndY=26.4942 EndZ=0
    g28: LineSegment StartX=132.428 StartY=20 StartZ=0 EndX=144.053 EndY=20 EndZ=0
    g29: LineSegment StartX=144.053 StartY=20 StartZ=0 EndX=147.645 EndY=8.94427 EndZ=0
  constraints (65):
    c: Equal(g0,g-25)
    c: Equal(g2,g-29)
    c: Equal(g3,g-30)
    c: Equal(g4,g-28)
    c: Equal(g1,g-26)
    c: Coincident(g0,g-25)
    c: Coincident(g1,g-26)
    c: Coincident(g2,g-29)
    c: Coincident(g3,g-30)
    c: Coincident(g4,g-28)
    c: Equal(g5,g-23)
    c: Equal(g6,g-24)
    c: Coincident(g5,g-23)
    c: Coincident(g6,g-24)
    c: Equal(g7,g-20)
    c: Coincident(g7,g-20)
    c: Equal(g9,g-22)
    c: Coincident(g9,g-22)
    c: Equal(g8,g-21)
    c: Coincident(g8,g-21)
    c: Equal(g13,g-12)
    c: Equal(g12,g-14)
    c: Equal(g10,g-9)
    c: Equal(g11,g-7)
    c: Coincident(g14,g-27)
    c: Coincident(g14,g-27)
    c: Coincident(g15,g14)
    c: Coincident(g15,g-5)
    c: Coincident(g16,g15)
    c: Coincident(g16,g-6)
    c: Coincident(g17,g16)
    c: Coincident(g17,g-7)
    c: Coincident(g11,g17)
    c: Coincident(g11,g-8)
    c: Coincident(g18,g11)
    c: Coincident(g18,g-9)
    c: Coincident(g10,g18)
    c: Coincident(g10,g-10)
    c: Coincident(g19,g10)
    c: Coincident(g19,g-11)
    c: Coincident(g20,g19)
    c: Coincident(g20,g-12)
    c: Coincident(g13,g20)
    c: Coincident(g13,g-13)
    c: Coincident(g21,g13)
    c: Coincident(g21,g-14)
    c: Coincident(g12,g21)
    c: Coincident(g12,g-15)
    c: Coincident(g22,g12)
    c: Coincident(g22,g-15)
    c: Coincident(g23,g22)
    c: Coincident(g23,g14)
    c: Coincident(g24,g-18)
    c: Coincident(g24,g-16)
    c: Coincident(g25,g24)
    c: Coincident(g25,g-19)
    c: Coincident(g26,g25)
    c: Coincident(g26,g-19)
    c: Coincident(g27,g26)
    c: Coincident(g27,g24)
    c: Coincident(g29,g10)
    c: Coincident(g28,g10)
    c: Coincident(g29,g28)
    c: Parallel(g28,g18)
    c: Parallel(g29,g19)
FEATURE [PartDesign::Pad] Pad011
  Direction = (0,1,-2e-16)
  Length = 2
  Length2 = 10
  Profile = -> Sketch114
  ReferenceAxis = -> Sketch114 [N_Axis]
  Refine = true
  Reversed = true
  Suppressed = false
  Type = 0
FEATURE [Sketcher::SketchObject] Sketch115
  ArcFitTolerance = 1e-06
  AttachmentSupport = -> [Pad011]
  ExternalGeometry = -> [Binder001]
  FullyConstrained = true
  MakeInternals = false
  MapMode = 5
  Placement = pos=(0,1.7e-15,0) rot=(0,0.707107,0.707107;3.14159rad)
  sketch-geometry (4):
    g0: ArcOfCircle CenterX=24.2 CenterY=26.7 CenterZ=0 NormalX=0 NormalY=0 NormalZ=1 AngleXU=0 Radius=3 StartAngle=4.48384e-08 EndAngle=3.14159
    g1: ArcOfCircle CenterX=24.2 CenterY=15.7 CenterZ=0 NormalX=0 NormalY=0 NormalZ=1 AngleXU=0 Radius=3 StartAngle=3.14159 EndAngle=6.28318
    g2: LineSegment StartX=21.2 StartY=26.7 StartZ=0 EndX=21.2 EndY=15.7 EndZ=0
    g3: LineSegment StartX=27.2 StartY=26.7 StartZ=0 EndX=27.2 EndY=15.7 EndZ=0
  constraints (12):
    c: Equal(g1,g-4)
    c: Equal(g0,g-3)
    c: Coincident(g0,g-3)
    c: Coincident(g1,g-4)
    c: Vertical(g2)
    c: Vertical(g3)
    c: Tangent(g3,g-3)
    c: Tangent(g2,g-3)
    c: Coincident(g0,g2)
    c: Coincident(g0,g3)
    c: Coincident(g1,g2)
    c: Coincident(g3,g1)
FEATURE [Sketcher::SketchObject] Sketch117
  ArcFitTolerance = 1e-06
  AttachmentSupport = -> [Pad011]
  ExternalGeometry = -> [Binder001]
  FullyConstrained = true
  MakeInternals = false
  MapMode = 5
  Placement = pos=(0,1.7e-15,0) rot=(0,0.707107,0.707107;3.14159rad)
  sketch-geometry (4):
    g0: Circle CenterX=43.2 CenterY=30.3 CenterZ=0 NormalX=0 NormalY=0 NormalZ=1 AngleXU=0 Radius=2.25
    g1: Circle CenterX=43.2 CenterY=12.1 CenterZ=0 NormalX=0 NormalY=0 NormalZ=1 AngleXU=0 Radius=2.25
    g2: Circle CenterX=18.6 CenterY=30.3 CenterZ=0 NormalX=0 NormalY=0 NormalZ=1 AngleXU=0 Radius=2.25
    g3: Circle CenterX=18.6 CenterY=12.1 CenterZ=0 NormalX=0 NormalY=0 NormalZ=1 AngleXU=0 Radius=2.25
  constraints (8):
    c: Diameter(g0) = 4.5
    c: Diameter(g1) = 4.5
    c: Diameter(g2) = 4.5
    c: Diameter(g3) = 4.5
    c: Coincident(g2,g-3)
    c: Coincident(g3,g-6)
    c: Coincident(g0,g-4)
    c: Coincident(g1,g-5)
FEATURE [Sketcher::SketchObject] Sketch118
  ArcFitTolerance = 1e-06
  AttachmentSupport = -> [Pad011]
  ExternalGeometry = -> [Binder001]
  FullyConstrained = true
  MakeInternals = false
  MapMode = 5
  Placement = pos=(0,-2,0) rot=(1,0,0;1.5708rad)
  sketch-geometry (12):
    g0: Circle CenterX=-78.51 CenterY=34.8 CenterZ=0 NormalX=0 NormalY=0 NormalZ=1 AngleXU=0 Radius=1.8
    g1: Circle CenterX=-78.51 CenterY=7.6 CenterZ=0 NormalX=0 NormalY=0 NormalZ=1 AngleXU=0 Radius=1.8
    g2: Circle CenterX=-5.6 CenterY=34.8 CenterZ=0 NormalX=0 NormalY=0 NormalZ=1 AngleXU=0 Radius=1.8
    g3: Circle CenterX=-5.6 CenterY=7.6 CenterZ=0 NormalX=0 NormalY=0 NormalZ=1 AngleXU=0 Radius=1.8
    g4: LineSegment StartX=0 StartY=39.2 StartZ=0 EndX=0 EndY=3.2 EndZ=0
    g5: LineSegment StartX=0 StartY=3.2 StartZ=0 EndX=-82.8 EndY=3.2 EndZ=0
    g6: LineSegment StartX=-82.8 StartY=3.2 StartZ=0 EndX=-82.8 EndY=39.2 EndZ=0
    g7: LineSegment StartX=-82.8 StartY=39.2 StartZ=0 EndX=0 EndY=39.2 EndZ=0
    g8: ArcOfCircle CenterX=-65 CenterY=21.2 CenterZ=0 NormalX=0 NormalY=0 NormalZ=1 AngleXU=0 Radius=10 StartAngle=1.5708 EndAngle=4.71239
    g9: ArcOfCircle CenterX=-19 CenterY=21.2 CenterZ=0 NormalX=0 NormalY=0 NormalZ=1 AngleXU=0 Radius=10 StartAngle=4.71239 EndAngle=7.85398
    g10: LineSegment StartX=-65 StartY=31.2 StartZ=0 EndX=-19 EndY=31.2 EndZ=0
    g11: LineSegment StartX=-65 StartY=11.2 StartZ=0 EndX=-19 EndY=11.2 EndZ=0
  constraints (25):
    c: Equal(g2,g-5)
    c: Equal(g3,g-7)
    c: Equal(g1,g-6)
    c: Equal(g0,g-4)
    c: Coincident(g0,g-4)
    c: Coincident(g1,g-6)
    c: Coincident(g3,g-7)
    c: Coincident(g2,g-5)
    c: Coincident(g4,g-8)
    c: Coincident(g4,g-9)
    c: Coincident(g5,g4)
    c: Coincident(g5,g-10)
    c: Coincident(g6,g5)
    c: PointOnObject(g6,g-3)
    c: Vertical(g6)
    c: Coincident(g7,g6)
    c: Coincident(g7,g4)
    c: Tangent(g8,g10) = 1.5708
    c: Tangent(g8,g11) = -1.5708
    c: Tangent(g9,g10) = 1.5708
    c: Tangent(g9,g11) = -1.5708
    c: Equal(g8,g9)
    c: Radius(g8) = 10
    c: Coincident(g8,g-11)
    c: Coincident(g9,g-12)
FEATURE [Sketcher::SketchObject] Sketch120
  ArcFitTolerance = 1e-06
  AttachmentSupport = -> [Pad011]
  ExternalGeometry = -> [Binder001]
  FullyConstrained = true
  MakeInternals = false
  MapMode = 5
  Placement = pos=(0,-2,0) rot=(1,0,0;1.5708rad)
  sketch-geometry (4):
    g0: LineSegment StartX=-137.815 StartY=39.2 StartZ=0 EndX=-142.655 EndY=24.303 EndZ=0
    g1: LineSegment StartX=-137.815 StartY=39.2 StartZ=0 EndX=-110.815 EndY=39.2 EndZ=0
    g2: LineSegment StartX=-142.655 StartY=24.303 StartZ=0 EndX=-110.815 EndY=24.303 EndZ=0
    g3: ArcOfCircle CenterX=-92.2534 CenterY=31.7515 CenterZ=0 NormalX=0 NormalY=0 NormalZ=1 AngleXU=0 Radius=20 StartAngle=2.75997 EndAngle=3.52321
  constraints (12):
    c: PointOnObject(g0,g-3)
    c: Coincident(g1,g0)
    c: PointOnObject(g1,g-3)
    c: Coincident(g2,g0)
    c: Horizontal(g2)
    c: Tangent(g0,g-4)
    c: Vertical(g2,g1)
    c: DistanceX(g1,g1) = 27
    c: DistanceY(g-6,g0) = 4
    c: Radius(g3) = 20
    c: Coincident(g3,g1)
    c: Coincident(g3,g2)
FEATURE [Sketcher::SketchObject] Sketch121
  ArcFitTolerance = 1e-06
  AttachmentSupport = -> [Pad011]
  ExternalGeometry = -> [Binder001]
  FullyConstrained = true
  MakeInternals = false
  MapMode = 5
  Placement = pos=(0,-2,0) rot=(1,0,0;1.5708rad)
  sketch-geometry (15):
    g0: LineSegment StartX=-137.815 StartY=39.2 StartZ=0 EndX=-143.955 EndY=20.303 EndZ=0
    g1: LineSegment StartX=-143.955 StartY=20.303 StartZ=0 EndX=-190.141 EndY=20.303 EndZ=0
    g2: LineSegment StartX=-190.141 StartY=20.303 StartZ=0 EndX=-186.139 EndY=31.3 EndZ=0
    g3: LineSegment StartX=-178.754 StartY=39.2 StartZ=0 EndX=-180.791 EndY=33.6029 EndZ=0
    g4: ArcOfCircle CenterX=-184.08 CenterY=34.8 CenterZ=0 NormalX=0 NormalY=0 NormalZ=1 AngleXU=0 Radius=3.5 StartAngle=4.71239 EndAngle=5.93412
    g5: LineSegment StartX=-184.08 StartY=31.3 StartZ=0 EndX=-186.139 EndY=31.3 EndZ=0
    g6: LineSegment StartX=-137.815 StartY=39.2 StartZ=0 EndX=-156.815 EndY=39.2 EndZ=0
    g7: LineSegment StartX=-168.815 StartY=39.2 StartZ=0 EndX=-178.754 EndY=39.2 EndZ=0
    g8: LineSegment StartX=-157.815 StartY=39.2 StartZ=0 EndX=-167.815 EndY=39.2 EndZ=0
    g9: LineSegment StartX=-168.815 StartY=31.2 StartZ=0 EndX=-156.815 EndY=31.2 EndZ=0
    g10: LineSegment StartX=-167.436 StartY=36.2 StartZ=0 EndX=-157.436 EndY=36.2 EndZ=0
    g11: ArcOfCircle CenterX=-176.411 CenterY=35.2 CenterZ=0 NormalX=0 NormalY=0 NormalZ=1 AngleXU=0 Radius=20 StartAngle=6.08183 EndAngle=6.48454
    g12: ArcOfCircle CenterX=-188.411 CenterY=35.2 CenterZ=0 NormalX=0 NormalY=0 NormalZ=1 AngleXU=0 Radius=20 StartAngle=6.08183 EndAngle=6.48454
    g13: ArcOfCircle CenterX=-177.411 CenterY=35.2 CenterZ=0 NormalX=0 NormalY=0 NormalZ=1 AngleXU=0 Radius=20 StartAngle=0.0500209 EndAngle=0.201358
    g14: ArcOfCircle CenterX=-187.411 CenterY=35.2 CenterZ=0 NormalX=0 NormalY=0 NormalZ=1 AngleXU=0 Radius=20 StartAngle=0.0500209 EndAngle=0.201358
  constraints (46):
    c: PointOnObject(g0,g-3)
    c: Tangent(g0,g-5)
    c: Coincident(g1,g0)
    c: Horizontal(g1)
    c: Coincident(g2,g1)
    c: PointOnObject(g3,g-3)
    c: Parallel(g3,g-6)
    c: Parallel(g2,g-6)
    c: Radius(g4) = 3.5
    c: Coincident(g4,g-7)
    c: Tangent(g3,g4) = 1.5708
    c: Horizontal(g5)
    c: Tangent(g5,g4) = 1.5708
    c: DistanceX(g-8,g5) = 3.8
    c: Coincident(g2,g5)
    c: Coincident(g6,g0)
    c: PointOnObject(g6,g-3)
    c: DistanceX(g6,g6) = 19
    c: PointOnObject(g7,g-3)
    c: DistanceX(g7,g6) = 12
    c: Coincident(g7,g3)
    c: PointOnObject(g8,g-3)
    c: PointOnObject(g8,g-3)
    c: DistanceX(g8,g8) = 10
    c: DistanceX(g8,g6) = 1
    c: Horizontal(g9)
    c: Vertical(g7,g9)
    c: Vertical(g6,g9)
    c: DistanceY(g9,g7) = 8
    c: Horizontal(g10)
    c: Equal(g8,g10)
    c: DistanceY(g10,g8) = 3
    c: Radius(g11) = 20
    c: Coincident(g11,g6)
    c: Coincident(g11,g9)
    c: Radius(g12) = 20
    c: Coincident(g12,g7)
    c: Coincident(g12,g9)
    c: Equal(g13,g11)
    c: Coincident(g13,g8)
    c: Coincident(g13,g10)
    c: Horizontal(g13,g11)
    c: Equal(g14,g12)
    c: Coincident(g14,g8)
    c: Coincident(g14,g10)
    c: Horizontal(g1,g-6)
FEATURE [Sketcher::SketchObject] Sketch122
  ArcFitTolerance = 1e-06
  AttachmentSupport = -> [Pad011]
  ExternalGeometry = -> [Binder001]
  FullyConstrained = true
  MakeInternals = false
  MapMode = 5
  Placement = pos=(0,-2,0) rot=(1,0,0;1.5708rad)
  sketch-geometry (8):
    g0: LineSegment StartX=-202.765 StartY=20.303 StartZ=0 EndX=-143.955 EndY=20.303 EndZ=0
    g1: ArcOfCircle CenterX=-184.801 CenterY=-67.3089 CenterZ=0 NormalX=0 NormalY=0 NormalZ=1 AngleXU=0 Radius=33.7833 StartAngle=2.70526 EndAngle=3.54053
    g2: LineSegment StartX=-176.685 StartY=-80.4316 StartZ=0 EndX=-215.932 EndY=-80.4316 EndZ=0
    g3: LineSegment StartX=-215.42 StartY=-53.0315 StartZ=0 EndX=-192.176 EndY=-3.18454 EndZ=0
    g4: ArcOfCircle CenterX=-207.583 CenterY=4 CenterZ=0 NormalX=0 NormalY=0 NormalZ=1 AngleXU=0 Radius=17 StartAngle=5.84685 EndAngle=7.56663
    g5: Circle CenterX=-213.443 CenterY=-76.8316 CenterZ=0 NormalX=0 NormalY=0 NormalZ=1 AngleXU=0 Radius=3
    g6: Circle CenterX=-179.305 CenterY=-76.8316 CenterZ=0 NormalX=0 NormalY=0 NormalZ=1 AngleXU=0 Radius=3
    g7: LineSegment StartX=-143.955 StartY=20.303 StartZ=0 EndX=-176.685 EndY=-80.4316 EndZ=0
  constraints (18):
    c: Coincident(g0,g-6)
    c: Coincident(g1,g-7)
    c: Coincident(g1,g-8)
    c: Coincident(g2,g1)
    c: Tangent(g3,g-5)
    c: Coincident(g4,g-6)
    c: Coincident(g4,g0)
    c: Coincident(g3,g4)
    c: Coincident(g1,g3)
    c: Diameter(g5) = 6
    c: Diameter(g6) = 6
    c: Coincident(g5,g-9)
    c: Coincident(g6,g-10)
    c: Horizontal(g0)
    c: Horizontal(g2)
    c: Coincident(g7,g0)
    c: Coincident(g7,g2)
    c: Tangent(g7,g-4)
FEATURE [Sketcher::SketchObject] Sketch123
  ArcFitTolerance = 1e-06
  AttachmentSupport = -> [Pad011]
  ExternalGeometry = -> [Binder001]
  FullyConstrained = true
  MakeInternals = false
  MapMode = 5
  Placement = pos=(0,-2,0) rot=(1,0,0;1.5708rad)
  sketch-geometry (4):
    g0: LineSegment StartX=-108 StartY=36.8 StartZ=0 EndX=-90 EndY=36.8 EndZ=0
    g1: LineSegment StartX=-108 StartY=36.8 StartZ=0 EndX=-108 EndY=26.8 EndZ=0
    g2: LineSegment StartX=-108 StartY=26.8 StartZ=0 EndX=-90 EndY=26.8 EndZ=0
    g3: ArcOfCircle CenterX=-94 CenterY=31.8 CenterZ=0 NormalX=0 NormalY=0 NormalZ=1 AngleXU=0 Radius=6.40312 StartAngle=5.38713 EndAngle=7.17924
  constraints (13):
    c: Horizontal(g0)
    c: Coincident(g1,g0)
    c: Vertical(g1)
    c: Coincident(g2,g1)
    c: Horizontal(g2)
    c: DistanceX(g0,g0) = 18
    c: DistanceY(g1,g1) = 10
    c: Equal(g0,g2)
    c: DistanceX(g0,g-3) = 90
    c: DistanceY(g0,g-3) = 2.4
    c: Coincident(g3,g0)
    c: Coincident(g3,g2)
    c: DistanceX(g3,g0) = 4
FEATURE [PartDesign::Chamfer] Chamfer014
  Angle = 45
  Base = -> Pad011 [Edge80,Edge4,Edge7]
  BaseFeature = -> Pad011
  ChamferType = 0
  FlipDirection = false
  Refine = true
  Size = 1.9
  Size2 = 1
  SupportTransform = false
  Suppressed = false
  UseAllEdges = false
FEATURE [PartDesign::Pocket] Pocket006
  BaseFeature = -> Chamfer014
  Direction = (0,-1,2e-16)
  Length = 1.2
  Length2 = 5
  Profile = -> Sketch115
  ReferenceAxis = -> Sketch115 [N_Axis]
  Refine = true
  Suppressed = false
  Type = 0
FEATURE [Sketcher::SketchObject] Sketch116
  ArcFitTolerance = 1e-06
  AttachmentSupport = -> [Pocket006]
  ExternalGeometry = -> [Binder001]
  FullyConstrained = true
  MakeInternals = false
  MapMode = 5
  Placement = pos=(0,1.7e-15,0) rot=(0,0.707107,0.707107;3.14159rad)
  sketch-geometry (4):
    g0: Circle CenterX=43.2 CenterY=30.3 CenterZ=0 NormalX=0 NormalY=0 NormalZ=1 AngleXU=0 Radius=3.4
    g1: Circle CenterX=43.2 CenterY=12.1 CenterZ=0 NormalX=0 NormalY=0 NormalZ=1 AngleXU=0 Radius=3.4
    g2: Circle CenterX=18.6 CenterY=30.3 CenterZ=0 NormalX=0 NormalY=0 NormalZ=1 AngleXU=0 Radius=3.4
    g3: Circle CenterX=18.6 CenterY=12.1 CenterZ=0 NormalX=0 NormalY=0 NormalZ=1 AngleXU=0 Radius=3.4
  constraints (8):
    c: Diameter(g0) = 6.8
    c: Diameter(g1) = 6.8
    c: Diameter(g2) = 6.8
    c: Diameter(g3) = 6.8
    c: Coincident(g2,g-3)
    c: Coincident(g0,g-4)
    c: Coincident(g3,g-6)
    c: Coincident(g1,g-5)
FEATURE [PartDesign::Pad] Pad012
  BaseFeature = -> Pocket006
  Direction = (0,1,-2e-16)
  Length = 2.4
  Length2 = 10
  Profile = -> Sketch116
  ReferenceAxis = -> Sketch116 [N_Axis]
  Refine = true
  Suppressed = false
  Type = 0
FEATURE [PartDesign::Pocket] Pocket007
  BaseFeature = -> Pad012
  Direction = (0,-1,2e-16)
  Length = 0.6
  Length2 = 2.4
  Profile = -> Sketch117
  ReferenceAxis = -> Sketch117 [N_Axis]
  Refine = true
  Suppressed = false
  Type = 4
FEATURE [PartDesign::Pad] Pad013
  BaseFeature = -> Pocket007
  Direction = (0,-1,2e-16)
  Length = 1.6
  Length2 = 10
  Profile = -> Sketch118
  ReferenceAxis = -> Sketch118 [N_Axis]
  Refine = true
  Suppressed = false
  Type = 0
FEATURE [Sketcher::SketchObject] Sketch119
  ArcFitTolerance = 1e-06
  AttachmentSupport = -> [Pad013]
  ExternalGeometry = -> [Binder001]
  FullyConstrained = true
  MakeInternals = false
  MapMode = 5
  Placement = pos=(0,-3.6,0) rot=(1,0,0;1.5708rad)
  sketch-geometry (21):
    g0: LineSegment [constr] StartX=-82.8 StartY=3.2 StartZ=0 EndX=-82.8 EndY=39.2 EndZ=0
    g1: ArcOfCircle CenterX=-78.51 CenterY=34.8 CenterZ=0 NormalX=0 NormalY=0 NormalZ=1 AngleXU=0 Radius=3.5 StartAngle=4.71239 EndAngle=6.28319
    g2: ArcOfCircle CenterX=-78.51 CenterY=7.6 CenterZ=0 NormalX=0 NormalY=0 NormalZ=1 AngleXU=0 Radius=3.5 StartAngle=0 EndAngle=1.5708
    g3: ArcOfCircle CenterX=-5.6 CenterY=34.8 CenterZ=0 NormalX=0 NormalY=0 NormalZ=1 AngleXU=0 Radius=3.5 StartAngle=3.14159 EndAngle=4.71239
    g4: ArcOfCircle CenterX=-5.6 CenterY=7.6 CenterZ=0 NormalX=0 NormalY=0 NormalZ=1 AngleXU=0 Radius=3.5 StartAngle=1.5708 EndAngle=3.14159
    g5: LineSegment StartX=0 StartY=39.2 StartZ=0 EndX=0 EndY=31.3 EndZ=0
    g6: LineSegment StartX=0 StartY=39.2 StartZ=0 EndX=-9.1 EndY=39.2 EndZ=0
    g7: LineSegment StartX=0 StartY=3.2 StartZ=0 EndX=0 EndY=11.1 EndZ=0
    g8: LineSegment StartX=0 StartY=3.2 StartZ=0 EndX=-9.1 EndY=3.2 EndZ=0
    g9: LineSegment StartX=-82.8 StartY=3.2 StartZ=0 EndX=-75.01 EndY=3.2 EndZ=0
    g10: LineSegment StartX=-82.8 StartY=3.2 StartZ=0 EndX=-82.8 EndY=11.1 EndZ=0
    g11: LineSegment StartX=-82.8 StartY=39.2 StartZ=0 EndX=-82.8 EndY=31.3 EndZ=0
    g12: LineSegment StartX=-82.8 StartY=39.2 StartZ=0 EndX=-75.01 EndY=39.2 EndZ=0
    g13: LineSegment StartX=-82.8 StartY=31.3 StartZ=0 EndX=-78.51 EndY=31.3 EndZ=0
    g14: LineSegment StartX=-75.01 StartY=39.2 StartZ=0 EndX=-75.01 EndY=34.8 EndZ=0
    g15: LineSegment StartX=-82.8 StartY=11.1 StartZ=0 EndX=-78.51 EndY=11.1 EndZ=0
    g16: LineSegment StartX=-75.01 StartY=3.2 StartZ=0 EndX=-75.01 EndY=7.6 EndZ=0
    g17: LineSegment StartX=-9.1 StartY=39.2 StartZ=0 EndX=-9.1 EndY=34.8 EndZ=0
    g18: LineSegment StartX=0 StartY=31.3 StartZ=0 EndX=-5.6 EndY=31.3 EndZ=0
    g19: LineSegment StartX=0 StartY=11.1 StartZ=0 EndX=-5.6 EndY=11.1 EndZ=0
    g20: LineSegment StartX=-9.1 StartY=3.2 StartZ=0 EndX=-9.1 EndY=7.6 EndZ=0
  constraints (51):
    c: Coincident(g0,g-10)
    c: PointOnObject(g0,g-8)
    c: Vertical(g0)
    c: Coincident(g1,g-3)
    c: Coincident(g2,g-4)
    c: Coincident(g3,g-5)
    c: Coincident(g4,g-6)
    c: Radius(g4) = 3.5
    c: Radius(g3) = 3.5
    c: Radius(g1) = 3.5
    c: Radius(g2) = 3.5
    c: Coincident(g5,g-9)
    c: PointOnObject(g5,g-9)
    c: Coincident(g6,g5)
    c: PointOnObject(g6,g-8)
    c: Coincident(g7,g-9)
    c: PointOnObject(g7,g-9)
    c: Coincident(g8,g7)
    c: PointOnObject(g8,g-7)
    c: Coincident(g9,g0)
    c: PointOnObject(g9,g-7)
    c: Coincident(g10,g0)
    c: PointOnObject(g10,g0)
    c: Coincident(g11,g0)
    c: PointOnObject(g11,g0)
    c: Coincident(g12,g0)
    c: PointOnObject(g12,g-8)
    c: Coincident(g13,g11)
    c: Horizontal(g13)
    c: Coincident(g14,g12)
    c: Vertical(g14)
    c: Coincident(g15,g10)
    c: Horizontal(g15)
    c: Coincident(g16,g9)
    c: Vertical(g16)
    c: Coincident(g17,g6)
    c: Vertical(g17)
    c: Coincident(g18,g5)
    c: Horizontal(g18)
    c: Coincident(g19,g7)
    c: Horizontal(g19)
    c: Coincident(g20,g8)
    c: Vertical(g20)
    c: Tangent(g20,g4) = 1.5708
    c: Tangent(g4,g19) = -1.5708
    c: Tangent(g18,g3) = 1.5708
    c: Tangent(g3,g17) = -1.5708
    c: Tangent(g13,g1) = -1.5708
    c: Tangent(g1,g14) = 1.5708
    c: Tangent(g16,g2) = -1.5708
    c: Tangent(g2,g15) = 1.5708
FEATURE [PartDesign::Pocket] Pocket008
  BaseFeature = -> Pad013
  Direction = (0,1,-2e-16)
  Length = 1.6
  Length2 = 5
  Profile = -> Sketch119
  ReferenceAxis = -> Sketch119 [N_Axis]
  Refine = true
  Suppressed = false
  Type = 0
FEATURE [PartDesign::Pad] Pad017
  BaseFeature = -> Pocket008
  Direction = (0,-1,2e-16)
  Length = 1.6
  Length2 = 10
  Profile = -> Sketch123
  ReferenceAxis = -> Sketch123 [N_Axis]
  Refine = true
  Suppressed = false
  Type = 0
FEATURE [Sketcher::SketchObject] Sketch125
  ArcFitTolerance = 1e-06
  AttachmentSupport = -> [Pad017]
  ExternalGeometry = -> [Pad017]
  FullyConstrained = true
  MakeInternals = false
  MapMode = 5
  Placement = pos=(0,-3.6,8e-16) rot=(1,0,0;1.5708rad)
  sketch-geometry (20):
    g0: LineSegment StartX=-108 StartY=35.8 StartZ=0 EndX=-108 EndY=35 EndZ=0
    g1: LineSegment StartX=-108 StartY=35 StartZ=0 EndX=-97 EndY=35 EndZ=0
    g2: LineSegment StartX=-97 StartY=35 StartZ=0 EndX=-97 EndY=35.8 EndZ=0
    g3: LineSegment StartX=-97 StartY=35.8 StartZ=0 EndX=-108 EndY=35.8 EndZ=0
    g4: LineSegment StartX=-108 StartY=28.6 StartZ=0 EndX=-108 EndY=27.8 EndZ=0
    g5: LineSegment StartX=-108 StartY=27.8 StartZ=0 EndX=-97 EndY=27.8 EndZ=0
    g6: LineSegment StartX=-97 StartY=27.8 StartZ=0 EndX=-97 EndY=28.6 EndZ=0
    g7: LineSegment StartX=-97 StartY=28.6 StartZ=0 EndX=-108 EndY=28.6 EndZ=0
    g8: LineSegment StartX=-108 StartY=30.4 StartZ=0 EndX=-108 EndY=29.6 EndZ=0
    g9: LineSegment StartX=-108 StartY=29.6 StartZ=0 EndX=-97 EndY=29.6 EndZ=0
    g10: LineSegment StartX=-97 StartY=29.6 StartZ=0 EndX=-97 EndY=30.4 EndZ=0
    g11: LineSegment StartX=-97 StartY=30.4 StartZ=0 EndX=-108 EndY=30.4 EndZ=0
    g12: LineSegment StartX=-108 StartY=32.2 StartZ=0 EndX=-108 EndY=31.4 EndZ=0
    g13: LineSegment StartX=-108 StartY=31.4 StartZ=0 EndX=-97 EndY=31.4 EndZ=0
    g14: LineSegment StartX=-97 StartY=31.4 StartZ=0 EndX=-97 EndY=32.2 EndZ=0
    g15: LineSegment StartX=-97 StartY=32.2 StartZ=0 EndX=-108 EndY=32.2 EndZ=0
    g16: LineSegment StartX=-108 StartY=34 StartZ=0 EndX=-108 EndY=33.2 EndZ=0
    g17: LineSegment StartX=-108 StartY=33.2 StartZ=0 EndX=-97 EndY=33.2 EndZ=0
    g18: LineSegment StartX=-97 StartY=33.2 StartZ=0 EndX=-97 EndY=34 EndZ=0
    g19: LineSegment StartX=-97 StartY=34 StartZ=0 EndX=-108 EndY=34 EndZ=0
  constraints (55):
    c: Coincident(g1,g0)
    c: Horizontal(g1)
    c: Coincident(g2,g1)
    c: Vertical(g2)
    c: Coincident(g3,g2)
    c: Horizontal(g3)
    c: Coincident(g3,g0)
    c: DistanceX(g1,g1) = 11
    c: DistanceY(g2,g2) = 0.8
    c: Coincident(g5,g4)
    c: Horizontal(g5)
    c: Coincident(g6,g5)
    c: Vertical(g6)
    c: Coincident(g7,g6)
    c: Horizontal(g7)
    c: Coincident(g7,g4)
    c: Coincident(g9,g8)
    c: Horizontal(g9)
    c: Coincident(g10,g9)
    c: Vertical(g10)
    c: Coincident(g11,g10)
    c: Horizontal(g11)
    c: Coincident(g11,g8)
    c: Coincident(g13,g12)
    c: Horizontal(g13)
    c: Coincident(g14,g13)
    c: Vertical(g14)
    c: Coincident(g15,g14)
    c: Horizontal(g15)
    c: Coincident(g15,g12)
    c: Coincident(g17,g16)
    c: Horizontal(g17)
    c: Coincident(g18,g17)
    c: Vertical(g18)
    c: Coincident(g19,g18)
    c: Horizontal(g19)
    c: Coincident(g19,g16)
    c: Equal(g3,g19)
    c: Equal(g3,g15)
    c: Equal(g3,g11)
    c: Equal(g3,g7)
    c: Equal(g2,g18)
    c: Equal(g2,g14)
    c: Equal(g2,g10)
    c: Equal(g2,g6)
    c: DistanceY(g-4,g4) = 1
    c: DistanceY(g4,g8) = 1
    c: DistanceY(g8,g12) = 1
    c: DistanceY(g12,g16) = 1
    c: DistanceY(g16,g0) = 1
    c: Tangent(g0,g-5)
    c: Tangent(g16,g-5)
    c: Tangent(g12,g-5)
    c: Tangent(g8,g-5)
    c: Tangent(g4,g-5)
FEATURE [PartDesign::Chamfer] Chamfer009
  Angle = 45
  Base = -> Pad017 [Edge151,Edge154]
  BaseFeature = -> Pad017
  ChamferType = 1
  FlipDirection = false
  Refine = true
  Size = 1.5
  Size2 = 2.8
  SupportTransform = false
  Suppressed = false
  UseAllEdges = false
FEATURE [PartDesign::Pocket] Pocket009
  BaseFeature = -> Chamfer009
  Direction = (0,1,-2e-16)
  Length = 1
  Length2 = 5
  Profile = -> Sketch125
  ReferenceAxis = -> Sketch125 [N_Axis]
  Refine = true
  Suppressed = false
  Type = 0
FEATURE [PartDesign::Pad] Pad014
  BaseFeature = -> Pocket009
  Direction = (0,-1,2e-16)
  Length = 0.8
  Length2 = 10
  Profile = -> Sketch120
  ReferenceAxis = -> Sketch120 [N_Axis]
  Refine = true
  Suppressed = false
  Type = 0
FEATURE [Sketcher::SketchObject] Sketch124
  ArcFitTolerance = 1e-06
  AttachmentSupport = -> [Pad014]
  ExternalGeometry = -> [Binder001]
  FullyConstrained = true
  MakeInternals = false
  MapMode = 5
  Placement = pos=(0,-2.8,6e-16) rot=(1,0,0;1.5708rad)
  sketch-geometry (4):
    g0: LineSegment StartX=-129 StartY=39.2 StartZ=0 EndX=-131.599 EndY=31.2 EndZ=0
    g1: LineSegment StartX=-118 StartY=39.2 StartZ=0 EndX=-120.599 EndY=31.2 EndZ=0
    g2: LineSegment StartX=-129 StartY=39.2 StartZ=0 EndX=-118 EndY=39.2 EndZ=0
    g3: LineSegment StartX=-120.599 StartY=31.2 StartZ=0 EndX=-131.599 EndY=31.2 EndZ=0
  constraints (12):
    c: PointOnObject(g0,g-3)
    c: PointOnObject(g1,g-3)
    c: Parallel(g-4,g0)
    c: Parallel(g-4,g1)
    c: Coincident(g2,g0)
    c: Coincident(g2,g1)
    c: DistanceX(g2,g2) = 11
    c: DistanceY(g1,g1) = 8
    c: Coincident(g3,g1)
    c: Horizontal(g3)
    c: Coincident(g3,g0)
    c: DistanceX(g1,g-3) = 118
FEATURE [PartDesign::Pad] Pad018
  BaseFeature = -> Pad014
  Direction = (0,-1,2e-16)
  Length = 1.2
  Length2 = 10
  Profile = -> Sketch124
  ReferenceAxis = -> Sketch124 [N_Axis]
  Refine = true
  Suppressed = false
  Type = 0
FEATURE [Sketcher::SketchObject] Sketch126
  ArcFitTolerance = 1e-06
  AttachmentSupport = -> [Pad018]
  ExternalGeometry = -> [Pad018]
  FullyConstrained = true
  MakeInternals = false
  MapMode = 5
  Placement = pos=(0,-4,0) rot=(1,0,0;1.5708rad)
  sketch-geometry (8):
    g0: LineSegment StartX=-129.877 StartY=36.5 StartZ=0 EndX=-130.137 EndY=35.7 EndZ=0
    g1: LineSegment StartX=-130.69 StartY=34 StartZ=0 EndX=-130.95 EndY=33.2 EndZ=0
    g2: LineSegment StartX=-129.877 StartY=36.5 StartZ=0 EndX=-118.877 EndY=36.5 EndZ=0
    g3: LineSegment StartX=-130.137 StartY=35.7 StartZ=0 EndX=-119.137 EndY=35.7 EndZ=0
    g4: LineSegment StartX=-130.69 StartY=34 StartZ=0 EndX=-119.69 EndY=34 EndZ=0
    g5: LineSegment StartX=-130.95 StartY=33.2 StartZ=0 EndX=-119.95 EndY=33.2 EndZ=0
    g6: LineSegment StartX=-118.877 StartY=36.5 StartZ=0 EndX=-119.137 EndY=35.7 EndZ=0
    g7: LineSegment StartX=-119.69 StartY=34 StartZ=0 EndX=-119.95 EndY=33.2 EndZ=0
  constraints (20):
    c: Coincident(g2,g0)
    c: Horizontal(g2)
    c: Coincident(g3,g0)
    c: Horizontal(g3)
    c: Coincident(g4,g1)
    c: Horizontal(g4)
    c: Coincident(g5,g1)
    c: Horizontal(g5)
    c: Coincident(g6,g2)
    c: Coincident(g6,g3)
    c: Coincident(g7,g4)
    c: Coincident(g7,g5)
    c: Tangent(g0,g-4)
    c: Tangent(g6,g-5)
    c: Tangent(g1,g-4)
    c: Tangent(g7,g-5)
    c: DistanceY(g3,g2) = 0.8
    c: DistanceY(g5,g4) = 0.8
    c: DistanceY(g-6,g1) = 2
    c: DistanceY(g-6,g0) = 4.5
FEATURE [PartDesign::Chamfer] Chamfer008
  Angle = 45
  Base = -> Pad018 [Edge257]
  BaseFeature = -> Pad018
  ChamferType = 1
  FlipDirection = false
  Refine = true
  Size = 1
  Size2 = 6
  SupportTransform = false
  Suppressed = false
  UseAllEdges = false
FEATURE [PartDesign::Pocket] Pocket010
  BaseFeature = -> Chamfer008
  Direction = (0,1,-2e-16)
  Length = 1
  Length2 = 5
  Profile = -> Sketch126
  ReferenceAxis = -> Sketch126 [N_Axis]
  Refine = true
  Suppressed = false
  Type = 0
FEATURE [PartDesign::Pad] Pad015
  BaseFeature = -> Pocket010
  Direction = (0,-1,2e-16)
  Length = 2
  Length2 = 10
  Profile = -> Sketch121
  ReferenceAxis = -> Sketch121 [N_Axis]
  Refine = true
  Suppressed = false
  Type = 0
FEATURE [PartDesign::Pad] Pad016
  BaseFeature = -> Pad015
  Direction = (0,-1,2e-16)
  Length = 1.6
  Length2 = 10
  Profile = -> Sketch122
  ReferenceAxis = -> Sketch122 [N_Axis]
  Refine = true
  Suppressed = false
  Type = 0
FEATURE [Sketcher::SketchObject] Sketch127
  ArcFitTolerance = 1e-06
  AttachmentSupport = -> [Pad016]
  ExternalGeometry = -> [Pad016]
  FullyConstrained = true
  MakeInternals = false
  MapMode = 5
  Placement = pos=(0,0,-80.4316) rot=(1,0,0;3.14159rad)
  sketch-geometry (8):
    g0: LineSegment StartX=-176.685 StartY=3.6 StartZ=0 EndX=-186.685 EndY=3.6 EndZ=0
    g1: LineSegment [constr] StartX=-186.685 StartY=3.6 StartZ=0 EndX=-186.685 EndY=-9e-16 EndZ=0
    g2: LineSegment StartX=-176.685 StartY=3.6 StartZ=0 EndX=-176.685 EndY=0 EndZ=0
    g3: ArcOfEllipse CenterX=-186.685 CenterY=-9e-16 CenterZ=0 NormalX=0 NormalY=0 NormalZ=1 MajorRadius=10 MinorRadius=3.6 AngleXU=1e-16 StartAngle=0 EndAngle=1.5708
    g4: LineSegment [constr] StartX=-176.685 StartY=-2e-15 StartZ=0 EndX=-196.685 EndY=-2e-15 EndZ=0
    g5: LineSegment [constr] StartX=-186.685 StartY=3.6 StartZ=0 EndX=-186.685 EndY=-3.6 EndZ=0
    g6: GeomPoint [constr] X=-177.356 Y=0 Z=0
    g7: GeomPoint [constr] X=-196.015 Y=-1.9e-15 Z=0
  constraints (13):
    c: Coincident(g0,g-4)
    c: PointOnObject(g0,g-4)
    c: DistanceX(g0,g0) = 10
    c: Coincident(g1,g0)
    c: PointOnObject(g1,g-5)
    c: Vertical(g1)
    c: Coincident(g2,g0)
    c: Coincident(g2,g-5)
    c: InternalAlignment(g4-g7 -> g3) x4
    c: Coincident(g3,g1)
    c: Coincident(g3,g0)
    c: Coincident(g3,g2)
    c: Horizontal(g4)
FEATURE [Sketcher::SketchObject] Sketch128
  ArcFitTolerance = 1e-06
  AttachmentSupport = -> [Pad016]
  ExternalGeometry = -> [Pad016]
  FullyConstrained = true
  MakeInternals = false
  MapMode = 5
  Placement = pos=(0,0,-80.4316) rot=(1,0,0;3.14159rad)
  sketch-geometry (8):
    g0: LineSegment StartX=-215.932 StartY=3.6 StartZ=0 EndX=-215.932 EndY=-1.3e-15 EndZ=0
    g1: LineSegment StartX=-215.932 StartY=3.6 StartZ=0 EndX=-205.932 EndY=3.6 EndZ=0
    g2: LineSegment [constr] StartX=-205.932 StartY=3.6 StartZ=0 EndX=-205.932 EndY=-9e-16 EndZ=0
    g3: ArcOfEllipse CenterX=-205.932 CenterY=-9e-16 CenterZ=0 NormalX=0 NormalY=0 NormalZ=1 MajorRadius=10 MinorRadius=3.6 AngleXU=-3.14159 StartAngle=4.71239 EndAngle=6.28319
    g4: LineSegment [constr] StartX=-215.932 StartY=-1e-15 StartZ=0 EndX=-195.932 EndY=-1e-15 EndZ=0
    g5: LineSegment [constr] StartX=-205.932 StartY=-3.6 StartZ=0 EndX=-205.932 EndY=3.6 EndZ=0
    g6: GeomPoint [constr] X=-215.262 Y=-2e-15 Z=0
    g7: GeomPoint [constr] X=-196.602 Y=-1e-15 Z=0
  constraints (13):
    c: Coincident(g0,g-4)
    c: Coincident(g0,g-5)
    c: Coincident(g1,g0)
    c: PointOnObject(g1,g-3)
    c: DistanceX(g1,g1) = 10
    c: Coincident(g2,g1)
    c: Vertical(g2)
    c: PointOnObject(g2,g-5)
    c: InternalAlignment(g4-g7 -> g3) x4
    c: Coincident(g3,g2)
    c: Coincident(g3,g1)
    c: Coincident(g3,g0)
    c: Horizontal(g4)
FEATURE [PartDesign::SubtractivePipe] SubtractivePipe002
  AuxilleryCurvelinear = true
  AuxillerySpineTangent = false
  BaseFeature = -> Pad016
  Binormal = (0,0,0)
  Mode = 0
  Profile = -> Sketch127
  Refine = true
  Spine = -> Pad016 [Edge254]
  SpineTangent = false
  Suppressed = false
  Transformation = 0
  Transition = 0
FEATURE [PartDesign::SubtractivePipe] SubtractivePipe003
  AuxilleryCurvelinear = true
  AuxillerySpineTangent = false
  BaseFeature = -> SubtractivePipe002
  Binormal = (0,0,0)
  Mode = 0
  Profile = -> Sketch128
  Refine = true
  Spine = -> Pad016 [Edge256,Edge251,Edge252]
  SpineTangent = false
  Suppressed = false
  Transformation = 0
  Transition = 0
FEATURE [Sketcher::SketchObject] Sketch129
  ArcFitTolerance = 1e-06
  AttachmentSupport = -> [Pad016]
  ExternalGeometry = -> [Binder001]
  FullyConstrained = true
  MakeInternals = false
  MapMode = 5
  Placement = pos=(0,-3.6,0) rot=(1,0,0;1.5708rad)
  sketch-geometry (12):
    g0: LineSegment [constr] StartX=-192.176 StartY=-3.18451 StartZ=0 EndX=-181.223 EndY=20.303 EndZ=0
    g1: LineSegment [constr] StartX=-202.765 StartY=20.303 StartZ=0 EndX=-181.223 EndY=20.303 EndZ=0
    g2: LineSegment StartX=-202.765 StartY=20.303 StartZ=0 EndX=-181.223 EndY=20.303 EndZ=0
    g3: LineSegment StartX=-192.176 StartY=-3.18451 StartZ=0 EndX=-196.804 EndY=-13.1107 EndZ=0
    g4: ArcOfCircle CenterX=-207.583 CenterY=4 CenterZ=0 NormalX=0 NormalY=0 NormalZ=1 AngleXU=0 Radius=17 StartAngle=5.84685 EndAngle=7.56663
    g5: ArcOfEllipse CenterX=-181.223 CenterY=8.55923 CenterZ=0 NormalX=0 NormalY=0 NormalZ=1 MajorRadius=23.4779 MinorRadius=11.7437 AngleXU=2e-16 StartAngle=4.71239 EndAngle=7.85398
    g6: LineSegment [constr] StartX=-157.745 StartY=8.55923 StartZ=0 EndX=-204.701 EndY=8.55923 EndZ=0
    g7: LineSegment [constr] StartX=-181.223 StartY=20.303 StartZ=0 EndX=-181.223 EndY=-3.18451 EndZ=0
    g8: GeomPoint [constr] X=-160.894 Y=8.55923 Z=0
    g9: GeomPoint [constr] X=-201.553 Y=8.55923 Z=0
    g10: ArcOfCircle CenterX=-181.223 CenterY=-20.3763 CenterZ=0 NormalX=0 NormalY=0 NormalZ=1 AngleXU=0 Radius=17.1918 StartAngle=1.57079 EndAngle=2.70526
    g11: GeomPoint [constr] X=-181.223 Y=-3.18451 Z=0
  constraints (23):
    c: Coincident(g0,g-5)
    c: Coincident(g1,g-6)
    c: Horizontal(g1)
    c: Coincident(g1,g0)
    c: Parallel(g0,g-4)
    c: Coincident(g2,g1)
    c: Coincident(g2,g0)
    c: Coincident(g3,g0)
    c: Equal(g4,g-5)
    c: Coincident(g4,g1)
    c: Coincident(g4,g0)
    c: InternalAlignment(g6-g9 -> g5) x4
    c: Vertical(g5,g0)
    c: Horizontal(g6)
    c: Coincident(g5,g0)
    c: DistanceX(g6,g-3) = 10.1
    c: Tangent(g10,g3) = -1.5708
    c: PointOnObject(g11,g10)
    c: Tangent(g5,g10,g11) = 1.5708
    c: Coincident(g10,g5)
    c: Coincident(g11,g7)
    c: Parallel(g3,g-4)
    c: Horizontal(g5,g0)
FEATURE [Sketcher::SketchObject] Sketch130
  ArcFitTolerance = 1e-06
  AttachmentOffset = pos=(0,0,-1.6) rot=(0,0,1;0rad)
  AttachmentSupport = -> [Pad016]
  ExternalGeometry = -> [Binder001]
  FullyConstrained = true
  MakeInternals = false
  MapMode = 5
  Placement = pos=(0,-2,-4e-16) rot=(1,0,0;1.5708rad)
  sketch-geometry (12):
    g0: LineSegment [constr] StartX=-192.176 StartY=-3.18451 StartZ=0 EndX=-181.223 EndY=20.303 EndZ=0
    g1: LineSegment [constr] StartX=-202.765 StartY=20.303 StartZ=0 EndX=-181.223 EndY=20.303 EndZ=0
    g2: LineSegment StartX=-202.765 StartY=20.303 StartZ=0 EndX=-181.223 EndY=20.303 EndZ=0
    g3: LineSegment StartX=-192.176 StartY=-3.18451 StartZ=0 EndX=-193.827 EndY=-6.72678 EndZ=0
    g4: ArcOfCircle CenterX=-207.583 CenterY=4 CenterZ=0 NormalX=0 NormalY=0 NormalZ=1 AngleXU=0 Radius=17 StartAngle=5.84685 EndAngle=7.56663
    g5: ArcOfEllipse CenterX=-181.223 CenterY=10.803 CenterZ=0 NormalX=0 NormalY=0 NormalZ=1 MajorRadius=14.4779 MinorRadius=9.5 AngleXU=0 StartAngle=4.71239 EndAngle=7.85398
    g6: LineSegment [constr] StartX=-166.745 StartY=10.803 StartZ=0 EndX=-195.701 EndY=10.803 EndZ=0
    g7: LineSegment [constr] StartX=-181.223 StartY=20.303 StartZ=0 EndX=-181.223 EndY=1.30297 EndZ=0
    g8: GeomPoint [constr] X=-170.298 Y=10.803 Z=0
    g9: GeomPoint [constr] X=-192.148 Y=10.803 Z=0
    g10: ArcOfCircle CenterX=-181.223 CenterY=-12.6042 CenterZ=0 NormalX=0 NormalY=0 NormalZ=1 AngleXU=0 Radius=13.9072 StartAngle=1.5708 EndAngle=2.70526
    g11: GeomPoint [constr] X=-181.223 Y=1.30297 Z=0
  constraints (23):
    c: Coincident(g0,g-5)
    c: Coincident(g1,g-6)
    c: Horizontal(g1)
    c: Coincident(g1,g0)
    c: Parallel(g0,g-4)
    c: Coincident(g2,g1)
    c: Coincident(g2,g0)
    c: Coincident(g3,g0)
    c: Equal(g4,g-5)
    c: Coincident(g4,g1)
    c: Coincident(g4,g0)
    c: InternalAlignment(g6-g9 -> g5) x4
    c: Vertical(g5,g0)
    c: Horizontal(g6)
    c: Coincident(g5,g0)
    c: DistanceX(g6,g-3) = 19.1
    c: Tangent(g10,g3) = -1.5708
    c: PointOnObject(g11,g10)
    c: Tangent(g5,g10,g11) = 1.5708
    c: Coincident(g10,g5)
    c: Coincident(g11,g7)
    c: Parallel(g3,g-4)
    c: DistanceY(g5,g0) = 19
FEATURE [Part::Part2DObjectPython] Clone2D001  label="Sketch130 (2D)"  # Draft 2D object (typed FeaturePython)
  Fuse = false
  Objects = -> [Sketch130]
  Placement = pos=(0,-2,-4e-16) rot=(1,0,0;1.5708rad)
  Scale = (1,1,1)
FEATURE [Sketcher::SketchObject] Sketch131
  ArcFitTolerance = 1e-06
  AttachmentOffset = pos=(0,0,-3.5) rot=(0,0,1;0rad)
  AttachmentSupport = -> [Pad016]
  ExternalGeometry = -> [Binder001]
  FullyConstrained = true
  MakeInternals = false
  MapMode = 5
  Placement = pos=(0,-0.1,-8e-16) rot=(1,0,0;1.5708rad)
  sketch-geometry (1):
    g0: GeomPoint X=-197.47 Y=8.55923 Z=0
  constraints (1):
    c: Symmetric(g-6,g-4,g0)
FEATURE [PartDesign::SubtractiveLoft] SubtractiveLoft002
  BaseFeature = -> SubtractivePipe003
  Closed = false
  Profile = -> Sketch129
  Refine = true
  Ruled = false
  Sections = -> [Sketch130]
  Suppressed = false
FEATURE [PartDesign::SubtractiveLoft] SubtractiveLoft003
  BaseFeature = -> SubtractiveLoft002
  Closed = false
  Profile = -> Clone2D001
  Refine = true
  Ruled = false
  Sections = -> [Sketch131]
  Suppressed = false
FEATURE [PartDesign::Chamfer] Chamfer010
  Angle = 45
  Base = -> SubtractiveLoft003 [Edge200,Edge201,Edge203,Edge202,Edge194]
  BaseFeature = -> SubtractiveLoft003
  ChamferType = 0
  FlipDirection = false
  Refine = true
  Size = 1.5
  Size2 = 1
  SupportTransform = false
  Suppressed = false
  UseAllEdges = false
FEATURE [PartDesign::Chamfer] Chamfer011
  Angle = 45
  Base = -> Chamfer010 [Edge15]
  BaseFeature = -> Chamfer010
  ChamferType = 0
  FlipDirection = false
  Refine = true
  Size = 3.5
  Size2 = 1
  SupportTransform = false
  Suppressed = false
  UseAllEdges = false
FEATURE [PartDesign::Chamfer] Chamfer012
  Angle = 45
  Base = -> Chamfer011 [Edge10]
  BaseFeature = -> Chamfer011
  ChamferType = 0
  FlipDirection = false
  Refine = true
  Size = 3.5
  Size2 = 1
  SupportTransform = false
  Suppressed = false
  UseAllEdges = false
FEATURE [PartDesign::Chamfer] Chamfer013
  Angle = 45
  Base = -> Chamfer012 [Edge146,Edge93]
  BaseFeature = -> Chamfer012
  ChamferType = 0
  FlipDirection = false
  Refine = true
  Size = 1.9
  Size2 = 1
  SupportTransform = false
  Suppressed = false
  UseAllEdges = false
FEATURE [Sketcher::SketchObject] Sketch132
  ArcFitTolerance = 1e-06
  AttachmentSupport = -> [Pad016]
  ExternalGeometry = -> [Binder001]
  FullyConstrained = true
  MakeInternals = false
  MapMode = 5
  Placement = pos=(0,-3.6,0) rot=(1,0,0;1.5708rad)
  sketch-geometry (3):
    g0: LineSegment [constr] StartX=-215.42 StartY=-53.0314 StartZ=0 EndX=-167.782 EndY=-53.0314 EndZ=0
    g1: Circle CenterX=-191.282 CenterY=-53.0314 CenterZ=0 NormalX=0 NormalY=0 NormalZ=1 AngleXU=0 Radius=11.5
    g2: Circle CenterX=-191.282 CenterY=-53.0314 CenterZ=0 NormalX=0 NormalY=0 NormalZ=1 AngleXU=0 Radius=10.7
  constraints (8):
    c: Coincident(g0,g-3)
    c: PointOnObject(g0,g-4)
    c: Horizontal(g0)
    c: Diameter(g1) = 23
    c: PointOnObject(g1,g0)
    c: DistanceX(g1,g0) = 23.5
    c: Diameter(g2) = 21.4
    c: Coincident(g2,g1)
FEATURE [PartDesign::Fillet] Fillet007
  Base = -> Chamfer013 [Edge84]
  BaseFeature = -> Chamfer013
  Radius = 1.1
  Refine = true
  SupportTransform = false
  Suppressed = false
  UseAllEdges = false
FEATURE [PartDesign::Fillet] Fillet008
  Base = -> Fillet007 [Edge77]
  BaseFeature = -> Fillet007
  Radius = 1.9
  Refine = true
  SupportTransform = false
  Suppressed = false
  UseAllEdges = false
FEATURE [PartDesign::Pocket] Pocket011
  BaseFeature = -> Fillet008
  Direction = (0,1,-2e-16)
  Length = 0.8
  Length2 = 5
  Profile = -> Sketch132
  ReferenceAxis = -> Sketch132 [N_Axis]
  Refine = true
  Suppressed = false
  Type = 0
FEATURE [Part::Part2DObjectPython] ShapeString  # Draft 2D object (typed FeaturePython)
  FontFile = <path>
  Fuse = false
  Justification = 6
  JustificationReference = 0
  KeepLeftMargin = false
  MakeFace = true
  ObliqueAngle = 0
  Placement = pos=(-199,-3.6,-57.5) rot=(1,0,0;1.5708rad)
  ScaleToSize = true
  Size = 10
  String = AS
  Tracking = 0
FEATURE [PartDesign::Pocket] Pocket012
  BaseFeature = -> Pocket011
  Direction = (0,1,0)
  Length = 1
  Length2 = 5
  Profile = -> ShapeString
  ReferenceAxis = -> ShapeString [N_Axis]
  Refine = true
  Suppressed = false
  Type = 0
FEATURE [PartDesign::Body] Body007  label="lato DX"
  AllowCompound = false
  Group = -> [Binder001,Sketch114,Pad011,Chamfer014,Sketch115,Pocket006,Sketch116,Pad012,Sketch117,Pocket007,Sketch118,Pad013,Sketch119,Pocket008,Pad017,Chamfer009,Pocket009,Sketch123,Sketch120,Pad014,Pad018,Chamfer008,Pocket010,Sketch121,Pad015,Sketch122,Pad016,Sketch124,Sketch125,Sketch126,Sketch127,Sketch128,SubtractivePipe002,SubtractivePipe003,Sketch129,Sketch130,Clone2D001,Sketch131,SubtractiveLoft002,+11 more]
  Origin = -> Origin007
  Tip = -> Pocket012
FEATURE [Sketcher::SketchObject] Sketch133
  ArcFitTolerance = 1e-06
  AttachmentSupport = -> [Binder]
  ExternalGeometry = -> [Binder]
  FullyConstrained = true
  MakeInternals = false
  MapMode = 5
  Placement = pos=(0,9e-16,0) rot=(0,0.707107,0.707107;3.14159rad)
  sketch-geometry (30):
    g0: LineSegment StartX=0 StartY=39.2 StartZ=0 EndX=0 EndY=3.2 EndZ=0
    g1: LineSegment StartX=0 StartY=3.2 StartZ=0 EndX=82.8 EndY=3.2 EndZ=0
    g2: LineSegment StartX=82.8 StartY=3.2 StartZ=0 EndX=82.8 EndY=6.2 EndZ=0
    g3: LineSegment StartX=82.8 StartY=6.2 StartZ=0 EndX=91.752 EndY=6.2 EndZ=0
    g4: LineSegment StartX=0 StartY=39.2 StartZ=0 EndX=195.887 EndY=39.2 EndZ=0
    g5: LineSegment StartX=195.887 StartY=39.2 StartZ=0 EndX=202.765 EndY=20.303 EndZ=0
    g6: LineSegment StartX=192.333 StartY=24.9893 StartZ=0 EndX=196.467 EndY=26.4942 EndZ=0
    g7: LineSegment StartX=196.467 StartY=26.4942 StartZ=0 EndX=194.073 EndY=33.0721 EndZ=0
    g8: LineSegment StartX=194.073 StartY=33.0721 StartZ=0 EndX=189.939 EndY=31.5672 EndZ=0
    g9: LineSegment StartX=189.939 StartY=31.5672 StartZ=0 EndX=192.333 EndY=24.9893 EndZ=0
    g10: ArcOfCircle CenterX=107.6 CenterY=4 CenterZ=0 NormalX=0 NormalY=0 NormalZ=1 AngleXU=0 Radius=16 StartAngle=1.5708 EndAngle=3.00366
    g11: LineSegment StartX=107.6 StartY=20 StartZ=0 EndX=132.428 EndY=20 EndZ=0
    g12: ArcOfCircle [constr] CenterX=132.428 CenterY=4 CenterZ=0 NormalX=0 NormalY=0 NormalZ=1 AngleXU=0 Radius=16 StartAngle=0.314159 EndAngle=1.5708
    g13: LineSegment StartX=147.645 StartY=8.94427 StartZ=0 EndX=176.685 EndY=-80.4316 EndZ=0
    g14: LineSegment StartX=176.685 StartY=-80.4316 StartZ=0 EndX=215.932 EndY=-80.4316 EndZ=0
    g15: ArcOfCircle CenterX=207.583 CenterY=4 CenterZ=0 NormalX=0 NormalY=0 NormalZ=1 AngleXU=0 Radius=17 StartAngle=1.85815 EndAngle=3.57792
    g16: ArcOfCircle CenterX=184.801 CenterY=-67.3089 CenterZ=0 NormalX=0 NormalY=0 NormalZ=1 AngleXU=0 Radius=33.7833 StartAngle=5.88425 EndAngle=6.71952
    g17: LineSegment StartX=192.176 StartY=-3.18451 StartZ=0 EndX=215.42 EndY=-53.0314 EndZ=0
    g18: Circle CenterX=5.6 CenterY=34.8 CenterZ=0 NormalX=0 NormalY=0 NormalZ=1 AngleXU=0 Radius=1.8
    g19: Circle CenterX=5.6 CenterY=7.6 CenterZ=0 NormalX=0 NormalY=0 NormalZ=1 AngleXU=0 Radius=1.8
    g20: Circle CenterX=78.51 CenterY=34.8 CenterZ=0 NormalX=0 NormalY=0 NormalZ=1 AngleXU=0 Radius=1.8
    g21: Circle CenterX=78.51 CenterY=7.6 CenterZ=0 NormalX=0 NormalY=0 NormalZ=1 AngleXU=0 Radius=1.8
    g22: Circle CenterX=184.08 CenterY=34.8 CenterZ=0 NormalX=0 NormalY=0 NormalZ=1 AngleXU=0 Radius=1.8
    g23: Circle CenterX=179.305 CenterY=-76.8316 CenterZ=0 NormalX=0 NormalY=0 NormalZ=1 AngleXU=0 Radius=1.8
    g24: Circle CenterX=213.443 CenterY=-76.8316 CenterZ=0 NormalX=0 NormalY=0 NormalZ=1 AngleXU=0 Radius=1.8
    g25: Circle CenterX=19 CenterY=21.2 CenterZ=0 NormalX=0 NormalY=0 NormalZ=1 AngleXU=0 Radius=6.3
    g26: Circle CenterX=42 CenterY=21.2 CenterZ=0 NormalX=0 NormalY=0 NormalZ=1 AngleXU=0 Radius=6.3
    g27: Circle CenterX=65 CenterY=21.2 CenterZ=0 NormalX=0 NormalY=0 NormalZ=1 AngleXU=0 Radius=6.3
    g28: LineSegment StartX=132.428 StartY=20 StartZ=0 EndX=144.053 EndY=20 EndZ=0
    g29: LineSegment StartX=147.645 StartY=8.94427 StartZ=0 EndX=144.053 EndY=20 EndZ=0
  constraints (65):
    c: Coincident(g0,g-4)
    c: Coincident(g0,g-5)
    c: Coincident(g1,g0)
    c: Coincident(g1,g-6)
    c: Coincident(g2,g1)
    c: Coincident(g2,g-7)
    c: Coincident(g3,g2)
    c: Coincident(g3,g-8)
    c: Coincident(g4,g0)
    c: Coincident(g4,g-16)
    c: Coincident(g5,g4)
    c: Coincident(g5,g-16)
    c: Coincident(g6,g-20)
    c: Coincident(g6,g-21)
    c: Coincident(g7,g6)
    c: Coincident(g7,g-23)
    c: Coincident(g8,g7)
    c: Coincident(g8,g-22)
    c: Coincident(g9,g8)
    c: Coincident(g9,g6)
    c: Equal(g10,g-8)
    c: Coincident(g10,g3)
    c: Coincident(g10,g-9)
    c: Coincident(g11,g10)
    c: Coincident(g11,g-10)
    c: Equal(g12,g-10)
    c: Coincident(g12,g11)
    c: Coincident(g12,g-11)
    c: Coincident(g13,g12)
    c: Coincident(g13,g-12)
    c: Coincident(g14,g13)
    c: Coincident(g14,g-13)
    c: Equal(g15,g-15)
    c: Coincident(g15,g5)
    c: Coincident(g15,g-15)
    c: Equal(g16,g-13)
    c: Coincident(g16,g14)
    c: Coincident(g16,g-14)
    c: Coincident(g17,g15)
    c: Coincident(g17,g16)
    c: Equal(g18,g-28)
    c: Equal(g19,g-29)
    c: Equal(g20,g-26)
    c: Equal(g21,g-27)
    c: Equal(g22,g-17)
    c: Equal(g24,g-25)
    c: Equal(g23,g-24)
    c: Coincident(g23,g-24)
    c: Coincident(g24,g-25)
    c: Coincident(g22,g-17)
    c: Coincident(g20,g-26)
    c: Coincident(g21,g-27)
    c: Coincident(g18,g-28)
    c: Coincident(g19,g-29)
    c: Equal(g25,g-30)
    c: Equal(g26,g-31)
    c: Equal(g27,g-32)
    c: Coincident(g25,g-30)
    c: Coincident(g26,g-31)
    c: Coincident(g27,g-32)
    c: Parallel(g28,g11)
    c: Parallel(g29,g13)
    c: Coincident(g28,g11)
    c: Coincident(g29,g12)
    c: Coincident(g29,g28)
FEATURE [PartDesign::Pad] Pad019
  Direction = (0,1,-2e-16)
  Length = 2
  Length2 = 10
  Profile = -> Sketch133
  ReferenceAxis = -> Sketch133 [N_Axis]
  Refine = true
  Suppressed = false
  Type = 0
FEATURE [Sketcher::SketchObject] Sketch091  label="Sketch091 - forma anteriore"
  ArcFitTolerance = 1e-06
  AttachmentSupport = -> [Pad019]
  ExternalGeometry = -> [Binder]
  FullyConstrained = true
  MakeInternals = false
  MapMode = 5
  Placement = pos=(0,2,0) rot=(0,0.707107,0.707107;3.14159rad)
  sketch-geometry (12):
    g0: Circle CenterX=5.6 CenterY=34.8 CenterZ=0 NormalX=0 NormalY=0 NormalZ=1 AngleXU=0 Radius=1.8
    g1: Circle CenterX=5.6 CenterY=7.6 CenterZ=0 NormalX=0 NormalY=0 NormalZ=1 AngleXU=0 Radius=1.8
    g2: Circle CenterX=78.51 CenterY=34.8 CenterZ=0 NormalX=0 NormalY=0 NormalZ=1 AngleXU=0 Radius=1.8
    g3: Circle CenterX=78.51 CenterY=7.6 CenterZ=0 NormalX=0 NormalY=0 NormalZ=1 AngleXU=0 Radius=1.8
    g4: LineSegment StartX=0 StartY=39.2 StartZ=0 EndX=0 EndY=3.2 EndZ=0
    g5: LineSegment StartX=0 StartY=3.2 StartZ=0 EndX=82.8 EndY=3.2 EndZ=0
    g6: LineSegment StartX=82.8 StartY=3.2 StartZ=0 EndX=82.8 EndY=39.2 EndZ=0
    g7: LineSegment StartX=82.8 StartY=39.2 StartZ=0 EndX=0 EndY=39.2 EndZ=0
    g8: ArcOfCircle CenterX=19 CenterY=21.2 CenterZ=0 NormalX=0 NormalY=0 NormalZ=1 AngleXU=0 Radius=10 StartAngle=1.5708 EndAngle=4.71239
    g9: ArcOfCircle CenterX=65 CenterY=21.2 CenterZ=0 NormalX=0 NormalY=0 NormalZ=1 AngleXU=0 Radius=10 StartAngle=4.71239 EndAngle=7.85398
    g10: LineSegment StartX=19 StartY=31.2 StartZ=0 EndX=65 EndY=31.2 EndZ=0
    g11: LineSegment StartX=19 StartY=11.2 StartZ=0 EndX=65 EndY=11.2 EndZ=0
  constraints (25):
    c: Equal(g2,g-7)
    c: Equal(g3,g-8)
    c: Equal(g1,g-13)
    c: Equal(g0,g-12)
    c: Coincident(g0,g-12)
    c: Coincident(g1,g-13)
    c: Coincident(g3,g-8)
    c: Coincident(g2,g-7)
    c: Coincident(g4,g-4)
    c: Coincident(g4,g-5)
    c: Coincident(g5,g4)
    c: Coincident(g5,g-6)
    c: Coincident(g6,g5)
    c: PointOnObject(g6,g-3)
    c: Vertical(g6)
    c: Coincident(g7,g6)
    c: Coincident(g7,g4)
    c: Tangent(g8,g10) = 1.5708
    c: Tangent(g8,g11) = -1.5708
    c: Tangent(g9,g10) = 1.5708
    c: Tangent(g9,g11) = -1.5708
    c: Equal(g8,g9)
    c: Radius(g8) = 10
    c: Coincident(g8,g-11)
    c: Coincident(g9,g-9)
FEATURE [Sketcher::SketchObject] Sketch093  label="Sketch093 - scavi interni pulsanti"
  ArcFitTolerance = 1e-06
  AttachmentSupport = -> [Pad019]
  ExternalGeometry = -> [Binder]
  FullyConstrained = true
  MakeInternals = false
  MapMode = 5
  Placement = pos=(0,1.8e-15,0) rot=(1,0,0;1.5708rad)
  sketch-geometry (3):
    g0: Circle CenterX=-65 CenterY=21.2 CenterZ=0 NormalX=0 NormalY=0 NormalZ=1 AngleXU=0 Radius=7.3
    g1: Circle CenterX=-42 CenterY=21.2 CenterZ=0 NormalX=0 NormalY=0 NormalZ=1 AngleXU=0 Radius=7.3
    g2: Circle CenterX=-19 CenterY=21.2 CenterZ=0 NormalX=0 NormalY=0 NormalZ=1 AngleXU=0 Radius=7.3
  constraints (6):
    c: Coincident(g0,g-3)
    c: Coincident(g1,g-4)
    c: Coincident(g2,g-5)
    c: Diameter(g0) = 14.6
    c: Diameter(g1) = 14.6
    c: Diameter(g2) = 14.6
FEATURE [Sketcher::SketchObject] Sketch094  label="Sketch094 - forma centrale"
  ArcFitTolerance = 1e-06
  AttachmentSupport = -> [Pad019]
  ExternalGeometry = -> [Binder]
  FullyConstrained = true
  MakeInternals = false
  MapMode = 5
  Placement = pos=(0,2,0) rot=(0,0.707107,0.707107;3.14159rad)
  sketch-geometry (4):
    g0: LineSegment StartX=137.815 StartY=39.2 StartZ=0 EndX=142.655 EndY=24.303 EndZ=0
    g1: LineSegment StartX=110.815 StartY=24.303 StartZ=0 EndX=142.655 EndY=24.303 EndZ=0
    g2: LineSegment StartX=137.815 StartY=39.2 StartZ=0 EndX=110.815 EndY=39.2 EndZ=0
    g3: ArcOfCircle CenterX=92.2534 CenterY=31.7515 CenterZ=0 NormalX=0 NormalY=0 NormalZ=1 AngleXU=0 Radius=20 StartAngle=5.90156 EndAngle=6.66481
  constraints (12):
    c: PointOnObject(g0,g-3)
    c: Tangent(g0,g-5)
    c: Horizontal(g1)
    c: Coincident(g1,g0)
    c: Coincident(g2,g0)
    c: PointOnObject(g2,g-3)
    c: DistanceX(g2,g2) = 27
    c: Vertical(g1,g2)
    c: Coincident(g3,g2)
    c: Radius(g3) = 20
    c: Coincident(g3,g1)
    c: DistanceY(g-6,g0) = 4
FEATURE [Sketcher::SketchObject] Sketch095  label="Sketch095 - forma posteriore"
  ArcFitTolerance = 1e-06
  AttachmentSupport = -> [Pad019]
  ExternalGeometry = -> [Binder]
  FullyConstrained = true
  MakeInternals = false
  MapMode = 5
  Placement = pos=(0,2,0) rot=(0,0.707107,0.707107;3.14159rad)
  sketch-geometry (15):
    g0: LineSegment StartX=137.815 StartY=39.2 StartZ=0 EndX=143.955 EndY=20.303 EndZ=0
    g1: LineSegment StartX=143.955 StartY=20.303 StartZ=0 EndX=190.141 EndY=20.303 EndZ=0
    g2: ArcOfCircle CenterX=184.08 CenterY=34.8 CenterZ=0 NormalX=0 NormalY=0 NormalZ=1 AngleXU=0 Radius=3.5 StartAngle=3.49066 EndAngle=4.71239
    g3: LineSegment StartX=180.791 StartY=33.6029 StartZ=0 EndX=178.754 EndY=39.2 EndZ=0
    g4: LineSegment StartX=184.08 StartY=31.3 StartZ=0 EndX=186.139 EndY=31.3 EndZ=0
    g5: LineSegment StartX=190.141 StartY=20.303 StartZ=0 EndX=186.139 EndY=31.3 EndZ=0
    g6: LineSegment StartX=137.815 StartY=39.2 StartZ=0 EndX=156.815 EndY=39.2 EndZ=0
    g7: LineSegment StartX=178.754 StartY=39.2 StartZ=0 EndX=168.815 EndY=39.2 EndZ=0
    g8: LineSegment StartX=156.815 StartY=31.2 StartZ=0 EndX=168.815 EndY=31.2 EndZ=0
    g9: ArcOfCircle CenterX=176.411 CenterY=35.2 CenterZ=0 NormalX=0 NormalY=0 NormalZ=1 AngleXU=0 Radius=20 StartAngle=2.94023 EndAngle=3.34295
    g10: ArcOfCircle CenterX=188.411 CenterY=35.2 CenterZ=0 NormalX=0 NormalY=0 NormalZ=1 AngleXU=0 Radius=20 StartAngle=2.94023 EndAngle=3.34295
    g11: LineSegment StartX=157.815 StartY=39.2 StartZ=0 EndX=167.815 EndY=39.2 EndZ=0
    g12: LineSegment StartX=157.436 StartY=36.2 StartZ=0 EndX=167.436 EndY=36.2 EndZ=0
    g13: ArcOfCircle CenterX=177.411 CenterY=35.2 CenterZ=0 NormalX=0 NormalY=0 NormalZ=1 AngleXU=0 Radius=20 StartAngle=2.94023 EndAngle=3.09157
    g14: ArcOfCircle CenterX=187.411 CenterY=35.2 CenterZ=0 NormalX=0 NormalY=0 NormalZ=1 AngleXU=0 Radius=20 StartAngle=2.94023 EndAngle=3.09157
  constraints (46):
    c: PointOnObject(g0,g-3)
    c: Tangent(g0,g-6)
    c: Coincident(g1,g0)
    c: Horizontal(g1)
    c: Radius(g2) = 3.5
    c: Coincident(g2,g-5)
    c: PointOnObject(g3,g-3)
    c: Parallel(g3,g-4)
    c: Tangent(g3,g2) = 1.5708
    c: Horizontal(g4)
    c: Tangent(g4,g2) = -1.5708
    c: Coincident(g5,g1)
    c: Parallel(g5,g-4)
    c: Coincident(g5,g4)
    c: DistanceX(g4,g-8) = 3.8
    c: Coincident(g6,g0)
    c: PointOnObject(g6,g-3)
    c: Coincident(g7,g3)
    c: PointOnObject(g7,g-3)
    c: Horizontal(g8)
    c: DistanceX(g6,g7) = 12
    c: Vertical(g8,g6)
    c: Vertical(g7,g8)
    c: DistanceY(g8,g6) = 8
    c: Coincident(g9,g8)
    c: Coincident(g9,g6)
    c: Coincident(g10,g7)
    c: Coincident(g10,g8)
    c: Radius(g9) = 20
    c: Radius(g10) = 20
    c: PointOnObject(g11,g-3)
    c: PointOnObject(g11,g-3)
    c: DistanceX(g11,g11) = 10
    c: DistanceX(g6,g11) = 1
    c: Horizontal(g12)
    c: Equal(g12,g11)
    c: DistanceY(g12,g11) = 3
    c: Coincident(g13,g11)
    c: Coincident(g13,g12)
    c: Radius(g13) = 20
    c: Coincident(g14,g11)
    c: Coincident(g14,g12)
    c: Radius(g14) = 20
    c: DistanceX(g0,g6) = 19
    c: Horizontal(g9,g13)
    c: Horizontal(g0,g-4)
FEATURE [Sketcher::SketchObject] Sketch096  label="Sketch096 - forma impugnatura"
  ArcFitTolerance = 1e-06
  AttachmentSupport = -> [Pad019]
  ExternalGeometry = -> [Binder]
  FullyConstrained = true
  MakeInternals = false
  MapMode = 5
  Placement = pos=(0,2,0) rot=(0,0.707107,0.707107;3.14159rad)
  sketch-geometry (8):
    g0: LineSegment StartX=176.685 StartY=-80.4316 StartZ=0 EndX=143.955 EndY=20.303 EndZ=0
    g1: LineSegment StartX=176.685 StartY=-80.4316 StartZ=0 EndX=215.932 EndY=-80.4316 EndZ=0
    g2: Circle CenterX=179.305 CenterY=-76.8316 CenterZ=0 NormalX=0 NormalY=0 NormalZ=1 AngleXU=0 Radius=3
    g3: Circle CenterX=213.443 CenterY=-76.8316 CenterZ=0 NormalX=0 NormalY=0 NormalZ=1 AngleXU=0 Radius=3
    g4: LineSegment StartX=143.955 StartY=20.303 StartZ=0 EndX=202.765 EndY=20.303 EndZ=0
    g5: LineSegment StartX=215.42 StartY=-53.0314 StartZ=0 EndX=192.176 EndY=-3.18451 EndZ=0
    g6: ArcOfCircle CenterX=184.801 CenterY=-67.3089 CenterZ=0 NormalX=0 NormalY=0 NormalZ=1 AngleXU=0 Radius=33.7833 StartAngle=5.88425 EndAngle=6.71952
    g7: ArcOfCircle CenterX=207.583 CenterY=4 CenterZ=0 NormalX=0 NormalY=0 NormalZ=1 AngleXU=0 Radius=17 StartAngle=1.85815 EndAngle=3.57792
  constraints (19):
    c: Coincident(g0,g-4)
    c: PointOnObject(g0,g-3)
    c: Horizontal(g0,g-7)
    c: Coincident(g1,g0)
    c: Coincident(g1,g-5)
    c: Diameter(g2) = 6
    c: Diameter(g3) = 6
    c: Coincident(g2,g-9)
    c: Coincident(g3,g-10)
    c: Coincident(g4,g0)
    c: Coincident(g5,g-6)
    c: Coincident(g6,g1)
    c: Coincident(g6,g5)
    c: Equal(g-5,g6)
    c: Coincident(g5,g-7)
    c: Coincident(g4,g-7)
    c: Tangent(g7,g-7)
    c: Coincident(g7,g4)
    c: Coincident(g7,g5)
FEATURE [Sketcher::SketchObject] Sketch097
  ArcFitTolerance = 1e-06
  AttachmentSupport = -> [Pad019]
  ExternalGeometry = -> [Binder]
  FullyConstrained = true
  MakeInternals = false
  MapMode = 5
  Placement = pos=(0,2,0) rot=(0,0.707107,0.707107;3.14159rad)
  sketch-geometry (4):
    g0: LineSegment StartX=90 StartY=36.8 StartZ=0 EndX=108 EndY=36.8 EndZ=0
    g1: LineSegment StartX=108 StartY=36.8 StartZ=0 EndX=108 EndY=26.8 EndZ=0
    g2: LineSegment StartX=108 StartY=26.8 StartZ=0 EndX=90 EndY=26.8 EndZ=0
    g3: ArcOfCircle CenterX=94 CenterY=31.8 CenterZ=0 NormalX=0 NormalY=0 NormalZ=1 AngleXU=0 Radius=6.40312 StartAngle=2.24554 EndAngle=4.03765
  constraints (13):
    c: Horizontal(g0)
    c: Coincident(g1,g0)
    c: Vertical(g1)
    c: DistanceX(g0,g0) = 18
    c: DistanceY(g1,g1) = 10
    c: Coincident(g2,g1)
    c: Horizontal(g2)
    c: Equal(g2,g0)
    c: DistanceY(g0,g-3) = 2.4
    c: Coincident(g3,g0)
    c: Coincident(g3,g2)
    c: DistanceX(g2,g3) = 4
    c: DistanceX(g-3,g0) = 90
FEATURE [PartDesign::Chamfer] Chamfer015
  Angle = 45
  Base = -> Pad019 [Edge19,Edge22,Edge79]
  BaseFeature = -> Pad019
  ChamferType = 0
  FlipDirection = false
  Refine = true
  Size = 1.9
  Size2 = 1
  SupportTransform = false
  Suppressed = false
  UseAllEdges = false
FEATURE [PartDesign::Pocket] Pocket002
  BaseFeature = -> Chamfer015
  Direction = (0,1,-2e-16)
  Length = 1.2
  Length2 = 5
  Profile = -> Sketch093
  ReferenceAxis = -> Sketch093 [N_Axis]
  Refine = true
  Suppressed = false
  Type = 0
FEATURE [PartDesign::Pad] Pad005
  BaseFeature = -> Pocket002
  Direction = (0,1,-2e-16)
  Length = 1.6
  Length2 = 10
  Profile = -> Sketch091
  ReferenceAxis = -> Sketch091 [N_Axis]
  Refine = true
  Suppressed = false
  Type = 0
FEATURE [Sketcher::SketchObject] Sketch092  label="Sketch092 - scavi per viti anteriori"
  ArcFitTolerance = 1e-06
  AttachmentSupport = -> [Pad005]
  ExternalGeometry = -> [Binder]
  FullyConstrained = true
  MakeInternals = false
  MapMode = 5
  Placement = pos=(0,3.6,0) rot=(0,0.707107,0.707107;3.14159rad)
  sketch-geometry (20):
    g0: ArcOfCircle CenterX=5.6 CenterY=7.6 CenterZ=0 NormalX=0 NormalY=0 NormalZ=1 AngleXU=0 Radius=3.5 StartAngle=0 EndAngle=1.5708
    g1: ArcOfCircle CenterX=5.6 CenterY=34.8 CenterZ=0 NormalX=0 NormalY=0 NormalZ=1 AngleXU=0 Radius=3.5 StartAngle=4.71239 EndAngle=6.28319
    g2: ArcOfCircle CenterX=78.51 CenterY=34.8 CenterZ=0 NormalX=0 NormalY=0 NormalZ=1 AngleXU=0 Radius=3.5 StartAngle=3.14159 EndAngle=4.71239
    g3: ArcOfCircle CenterX=78.51 CenterY=7.6 CenterZ=0 NormalX=0 NormalY=0 NormalZ=1 AngleXU=0 Radius=3.5 StartAngle=1.5708 EndAngle=3.14159
    g4: LineSegment StartX=0 StartY=3.2 StartZ=0 EndX=0 EndY=11.1 EndZ=0
    g5: LineSegment StartX=0 StartY=11.1 StartZ=0 EndX=5.6 EndY=11.1 EndZ=0
    g6: LineSegment StartX=0 StartY=3.2 StartZ=0 EndX=9.1 EndY=3.2 EndZ=0
    g7: LineSegment StartX=9.1 StartY=3.2 StartZ=0 EndX=9.1 EndY=7.6 EndZ=0
    g8: LineSegment StartX=0 StartY=39.2 StartZ=0 EndX=0 EndY=31.3 EndZ=0
    g9: LineSegment StartX=0 StartY=31.3 StartZ=0 EndX=5.6 EndY=31.3 EndZ=0
    g10: LineSegment StartX=0 StartY=39.2 StartZ=0 EndX=9.1 EndY=39.2 EndZ=0
    g11: LineSegment StartX=9.1 StartY=39.2 StartZ=0 EndX=9.1 EndY=34.8 EndZ=0
    g12: LineSegment StartX=82.8 StartY=39.2 StartZ=0 EndX=75.01 EndY=39.2 EndZ=0
    g13: LineSegment StartX=82.8 StartY=39.2 StartZ=0 EndX=82.8 EndY=31.3 EndZ=0
    g14: LineSegment StartX=82.8 StartY=31.3 StartZ=0 EndX=78.51 EndY=31.3 EndZ=0
    g15: LineSegment StartX=82.8 StartY=3.2 StartZ=0 EndX=75.01 EndY=3.2 EndZ=0
    g16: LineSegment StartX=75.01 StartY=3.2 StartZ=0 EndX=75.01 EndY=7.6 EndZ=0
    g17: LineSegment StartX=82.8 StartY=3.2 StartZ=0 EndX=82.8 EndY=11.1 EndZ=0
    g18: LineSegment StartX=82.8 StartY=11.1 StartZ=0 EndX=78.51 EndY=11.1 EndZ=0
    g19: LineSegment StartX=75.01 StartY=39.2 StartZ=0 EndX=75.01 EndY=34.8 EndZ=0
  constraints (48):
    c: Radius(g0) = 3.5
    c: Coincident(g0,g-10)
    c: Radius(g1) = 3.5
    c: Coincident(g1,g-9)
    c: Radius(g2) = 3.5
    c: Coincident(g2,g-8)
    c: Radius(g3) = 3.5
    c: Coincident(g3,g-7)
    c: Coincident(g4,g-5)
    c: PointOnObject(g4,g-4)
    c: Coincident(g5,g4)
    c: Horizontal(g5)
    c: Coincident(g6,g4)
    c: PointOnObject(g6,g-5)
    c: Coincident(g7,g6)
    c: Vertical(g7)
    c: Coincident(g8,g-4)
    c: PointOnObject(g8,g-4)
    c: Coincident(g9,g8)
    c: Horizontal(g9)
    c: Coincident(g10,g8)
    c: PointOnObject(g10,g-3)
    c: Coincident(g11,g10)
    c: Vertical(g11)
    c: PointOnObject(g12,g-3)
    c: PointOnObject(g12,g-3)
    c: Coincident(g13,g12)
    c: Vertical(g13)
    c: Coincident(g14,g13)
    c: Horizontal(g14)
    c: Coincident(g15,g-6)
    c: PointOnObject(g15,g-5)
    c: Coincident(g16,g15)
    c: Vertical(g16)
    c: Coincident(g17,g15)
    c: Coincident(g18,g17)
    c: Horizontal(g18)
    c: Tangent(g3,g18) = -1.5708
    c: Tangent(g16,g3) = 1.5708
    c: Coincident(g19,g12)
    c: Vertical(g19)
    c: Tangent(g2,g19) = -1.5708
    c: Tangent(g2,g14) = 1.5708
    c: Tangent(g0,g7) = -1.5708
    c: Tangent(g0,g5) = 1.5708
    c: Tangent(g9,g1) = -1.5708
    c: Tangent(g1,g11) = 1.5708
    c: Tangent(g17,g13)
FEATURE [PartDesign::Pocket] Pocket001
  BaseFeature = -> Pad005
  Direction = (0,-1,2e-16)
  Length = 1.6
  Length2 = 5
  Profile = -> Sketch092
  ReferenceAxis = -> Sketch092 [N_Axis]
  Refine = true
  Suppressed = false
  Type = 0
FEATURE [PartDesign::Pad] Pad006
  BaseFeature = -> Pocket001
  Direction = (0,1,-2e-16)
  Length = 0.8
  Length2 = 10
  Profile = -> Sketch094
  ReferenceAxis = -> Sketch094 [N_Axis]
  Refine = true
  Suppressed = false
  Type = 0
FEATURE [PartDesign::Pad] Pad007
  BaseFeature = -> Pad006
  Direction = (0,1,-2e-16)
  Length = 2
  Length2 = 10
  Profile = -> Sketch095
  ReferenceAxis = -> Sketch095 [N_Axis]
  Refine = true
  Suppressed = false
  Type = 0
FEATURE [PartDesign::Pad] Pad008  label="Pad008 - forma impugnatura"
  BaseFeature = -> Pad007
  Direction = (0,1,-2e-16)
  Length = 1.6
  Length2 = 10
  Profile = -> Sketch096
  ReferenceAxis = -> Sketch096 [N_Axis]
  Refine = true
  Suppressed = false
  Type = 0
FEATURE [PartDesign::Pad] Pad009
  BaseFeature = -> Pad008
  Direction = (0,1,-2e-16)
  Length = 1.6
  Length2 = 10
  Profile = -> Sketch097
  ReferenceAxis = -> Sketch097 [N_Axis]
  Refine = true
  Suppressed = false
  Type = 0
FEATURE [Sketcher::SketchObject] Sketch098
  ArcFitTolerance = 1e-06
  AttachmentSupport = -> [Pad006]
  ExternalGeometry = -> [Binder]
  FullyConstrained = true
  MakeInternals = false
  MapMode = 5
  Placement = pos=(0,2.8,-7e-16) rot=(0,0.707107,0.707107;3.14159rad)
  sketch-geometry (4):
    g0: LineSegment StartX=118 StartY=39.2 StartZ=0 EndX=129 EndY=39.2 EndZ=0
    g1: LineSegment StartX=120.599 StartY=31.2 StartZ=0 EndX=131.599 EndY=31.2 EndZ=0
    g2: LineSegment StartX=129 StartY=39.2 StartZ=0 EndX=131.599 EndY=31.2 EndZ=0
    g3: LineSegment StartX=118 StartY=39.2 StartZ=0 EndX=120.599 EndY=31.2 EndZ=0
  constraints (12):
    c: PointOnObject(g0,g-3)
    c: PointOnObject(g0,g-3)
    c: DistanceX(g0,g0) = 11
    c: Horizontal(g1)
    c: Equal(g1,g0)
    c: Coincident(g2,g0)
    c: Coincident(g3,g0)
    c: Parallel(g-4,g2)
    c: Coincident(g1,g2)
    c: Coincident(g1,g3)
    c: DistanceY(g1,g0) = 8
    c: DistanceX(g-3,g0) = 118
FEATURE [Sketcher::SketchObject] Sketch099
  ArcFitTolerance = 1e-06
  AttachmentSupport = -> [Pad008]
  ExternalGeometry = -> [Binder]
  FullyConstrained = true
  MakeInternals = false
  MapMode = 5
  Placement = pos=(0,3.6,0) rot=(0,0.707107,0.707107;3.14159rad)
  sketch-geometry (13):
    g0: LineSegment StartX=192.176 StartY=-3.18451 StartZ=0 EndX=196.804 EndY=-13.1108 EndZ=0
    g1: LineSegment [constr] StartX=202.765 StartY=20.303 StartZ=0 EndX=181.223 EndY=20.303 EndZ=0
    g2: LineSegment [constr] StartX=181.223 StartY=20.303 StartZ=0 EndX=181.223 EndY=-3.18451 EndZ=0
    g3: ArcOfCircle CenterX=181.223 CenterY=-20.3764 CenterZ=0 NormalX=0 NormalY=0 NormalZ=1 AngleXU=0 Radius=17.1918 StartAngle=0.436332 EndAngle=1.57079
    g4: ArcOfEllipse CenterX=181.223 CenterY=8.55923 CenterZ=0 NormalX=0 NormalY=0 NormalZ=1 MajorRadius=23.4779 MinorRadius=11.7437 AngleXU=0 StartAngle=1.5708 EndAngle=4.71239
    g5: LineSegment [constr] StartX=204.701 StartY=8.55923 StartZ=0 EndX=157.745 EndY=8.55923 EndZ=0
    g6: LineSegment [constr] StartX=181.223 StartY=20.303 StartZ=0 EndX=181.223 EndY=-3.18451 EndZ=0
    g7: GeomPoint [constr] X=201.553 Y=8.55923 Z=0
    g8: GeomPoint [constr] X=160.894 Y=8.55923 Z=0
    g9: GeomPoint [constr] X=181.223 Y=-3.18451 Z=0
    g10: LineSegment StartX=181.223 StartY=20.303 StartZ=0 EndX=202.765 EndY=20.303 EndZ=0
    g11: ArcOfCircle CenterX=207.583 CenterY=4 CenterZ=0 NormalX=0 NormalY=0 NormalZ=1 AngleXU=0 Radius=17 StartAngle=1.85815 EndAngle=3.57792
    g12: LineSegment [constr] StartX=172.411 StartY=39.2 StartZ=0 EndX=192.176 EndY=-3.18451 EndZ=0
  constraints (27):
    c: Coincident(g1,g-7)
    c: Horizontal(g1)
    c: Coincident(g2,g1)
    c: Vertical(g2)
    c: Horizontal(g2,g0)
    c: Coincident(g3,g0)
    c: Coincident(g3,g2)
    c: InternalAlignment(g5-g8 -> g4) x4
    c: Horizontal(g5)
    c: PointOnObject(g4,g2)
    c: Coincident(g4,g1)
    c: DistanceX(g-3,g5) = 10.1
    c: Coincident(g4,g2)
    c: Tangent(g3,g-5)
    c: PointOnObject(g9,g4)
    c: PointOnObject(g9,g3)
    c: Tangent(g4,g3,g9) = 1.5708
    c: Coincident(g10,g1)
    c: Coincident(g10,g1)
    c: Equal(g11,g-4)
    c: Coincident(g11,g1)
    c: Coincident(g11,g0)
    c: PointOnObject(g12,g-6)
    c: PointOnObject(g1,g12)
    c: Tangent(g12,g-5) = -1.5708
    c: Tangent(g0,g-5) = -1.5708
    c: Horizontal(g9,g12)
FEATURE [Sketcher::SketchObject] Sketch106  label="Sketch106 - smusso impuniatura interno"
  ArcFitTolerance = 1e-06
  AttachmentSupport = -> [Pad008]
  ExternalGeometry = -> [Pad008]
  FullyConstrained = true
  MakeInternals = false
  MapMode = 5
  Placement = pos=(0,-1.586e-13,-80.4316) rot=(1,0,0;3.14159rad)
  sketch-geometry (9):
    g0: LineSegment StartX=-176.685 StartY=-3.6 StartZ=0 EndX=-176.685 EndY=1.1684e-12 EndZ=0
    g1: LineSegment [constr] StartX=-176.685 StartY=1.79e-14 StartZ=0 EndX=-176.685 EndY=1.1684e-12 EndZ=0
    g2: LineSegment [constr] StartX=-186.685 StartY=-3.6 StartZ=0 EndX=-186.685 EndY=1.1684e-12 EndZ=0
    g3: ArcOfEllipse CenterX=-186.685 CenterY=1.1684e-12 CenterZ=0 NormalX=0 NormalY=0 NormalZ=1 MajorRadius=10 MinorRadius=3.6 AngleXU=-3.14159 StartAngle=1.5708 EndAngle=3.14159
    g4: LineSegment [constr] StartX=-196.685 StartY=1.79e-14 StartZ=0 EndX=-176.685 EndY=1.79e-14 EndZ=0
    g5: LineSegment [constr] StartX=-186.685 StartY=-3.6 StartZ=0 EndX=-186.685 EndY=3.6 EndZ=0
    g6: GeomPoint [constr] X=-196.015 Y=1.53e-14 Z=0
    g7: GeomPoint [constr] X=-177.356 Y=1.85e-14 Z=0
    g8: LineSegment StartX=-176.685 StartY=-3.6 StartZ=0 EndX=-186.685 EndY=-3.6 EndZ=0
  constraints (15):
    c: PointOnObject(g2,g-3)
    c: Coincident(g1,g-5)
    c: DistanceY(g1,g1) = 0
    c: Coincident(g0,g1)
    c: DistanceX(g2,g-5) = 10
    c: Vertical(g2)
    c: Horizontal(g2,g0)
    c: InternalAlignment(g4-g7 -> g3) x4
    c: Coincident(g3,g2)
    c: Horizontal(g4)
    c: Coincident(g3,g0)
    c: Tangent(g0,g-5) = 1.5708
    c: Coincident(g3,g2)
    c: Coincident(g8,g0)
    c: Coincident(g8,g2)
FEATURE [Sketcher::SketchObject] Sketch107  label="Sketch107 - smusso impugnatura esterno"
  ArcFitTolerance = 1e-06
  AttachmentSupport = -> [Pad008]
  ExternalGeometry = -> [Pad008]
  FullyConstrained = true
  MakeInternals = false
  MapMode = 5
  Placement = pos=(0,-1.586e-13,-80.4316) rot=(1,0,0;3.14159rad)
  sketch-geometry (9):
    g0: LineSegment [constr] StartX=-215.932 StartY=1.79e-14 StartZ=0 EndX=-215.932 EndY=2.03e-14 EndZ=0
    g1: LineSegment StartX=-215.932 StartY=-3.6 StartZ=0 EndX=-215.932 EndY=2.04e-14 EndZ=0
    g2: LineSegment StartX=-215.932 StartY=-3.6 StartZ=0 EndX=-205.932 EndY=-3.6 EndZ=0
    g3: LineSegment [constr] StartX=-205.932 StartY=-3.6 StartZ=0 EndX=-205.932 EndY=2.04e-14 EndZ=0
    g4: ArcOfEllipse CenterX=-205.932 CenterY=2.03e-14 CenterZ=0 NormalX=0 NormalY=0 NormalZ=1 MajorRadius=10 MinorRadius=3.6 AngleXU=3.14159 StartAngle=1e-16 EndAngle=1.5708
    g5: LineSegment [constr] StartX=-215.932 StartY=1.79e-14 StartZ=0 EndX=-195.932 EndY=1.79e-14 EndZ=0
    g6: LineSegment [constr] StartX=-205.932 StartY=-3.6 StartZ=0 EndX=-205.932 EndY=3.6 EndZ=0
    g7: GeomPoint [constr] X=-215.262 Y=2.05e-14 Z=0
    g8: GeomPoint [constr] X=-196.602 Y=1.78e-14 Z=0
  constraints (16):
    c: Coincident(g0,g-6)
    c: PointOnObject(g0,g-6)
    c: DistanceY(g0,g0) = 0
    c: Coincident(g1,g-6)
    c: Coincident(g1,g0)
    c: Tangent(g2,g-3)
    c: DistanceX(g2,g2) = 10
    c: Coincident(g3,g2)
    c: Vertical(g3)
    c: Horizontal(g3,g0)
    c: InternalAlignment(g5-g8 -> g4) x4
    c: Coincident(g4,g3)
    c: Horizontal(g5)
    c: Coincident(g4,g0)
    c: Coincident(g4,g2)
    c: PointOnObject(g2,g1)
FEATURE [Sketcher::SketchObject] Sketch108
  ArcFitTolerance = 1e-06
  AttachmentOffset = pos=(0,0,-1.6) rot=(0,0,1;0rad)
  AttachmentSupport = -> [Pad008]
  ExternalGeometry = -> [Binder]
  FullyConstrained = true
  MakeInternals = false
  MapMode = 5
  Placement = pos=(0,2,4e-16) rot=(0,0.707107,0.707107;3.14159rad)
  sketch-geometry (14):
    g0: LineSegment StartX=192.176 StartY=-3.18451 StartZ=0 EndX=193.827 EndY=-6.72678 EndZ=0
    g1: LineSegment [constr] StartX=202.765 StartY=20.303 StartZ=0 EndX=181.223 EndY=20.303 EndZ=0
    g2: LineSegment [constr] StartX=181.223 StartY=20.303 StartZ=0 EndX=181.223 EndY=1.30297 EndZ=0
    g3: ArcOfCircle CenterX=181.223 CenterY=-12.6042 CenterZ=0 NormalX=0 NormalY=0 NormalZ=1 AngleXU=0 Radius=13.9072 StartAngle=0.436332 EndAngle=1.5708
    g4: ArcOfEllipse CenterX=181.223 CenterY=10.803 CenterZ=0 NormalX=0 NormalY=0 NormalZ=1 MajorRadius=14.4779 MinorRadius=9.5 AngleXU=0 StartAngle=1.5708 EndAngle=4.71239
    g5: LineSegment [constr] StartX=195.701 StartY=10.803 StartZ=0 EndX=166.745 EndY=10.803 EndZ=0
    g6: LineSegment [constr] StartX=181.223 StartY=20.303 StartZ=0 EndX=181.223 EndY=1.30297 EndZ=0
    g7: GeomPoint [constr] X=192.148 Y=10.803 Z=0
    g8: GeomPoint [constr] X=170.298 Y=10.803 Z=0
    g9: LineSegment StartX=181.223 StartY=20.303 StartZ=0 EndX=202.765 EndY=20.303 EndZ=0
    g10: ArcOfCircle CenterX=207.583 CenterY=4 CenterZ=0 NormalX=0 NormalY=0 NormalZ=1 AngleXU=0 Radius=17 StartAngle=1.85815 EndAngle=3.57792
    g11: LineSegment [constr] StartX=172.411 StartY=39.2 StartZ=0 EndX=192.176 EndY=-3.18451 EndZ=0
    g12: GeomPoint [constr] X=181.223 Y=1.30297 Z=0
    g13: GeomPoint [constr] X=181.223 Y=1.30297 Z=0
  constraints (28):
    c: Coincident(g1,g-7)
    c: Horizontal(g1)
    c: Coincident(g2,g1)
    c: Vertical(g2)
    c: Coincident(g3,g2)
    c: InternalAlignment(g5-g8 -> g4) x4
    c: Horizontal(g5)
    c: PointOnObject(g4,g2)
    c: Coincident(g4,g1)
    c: DistanceX(g-3,g5) = 19.1
    c: Coincident(g4,g2)
    c: Coincident(g9,g1)
    c: Coincident(g9,g1)
    c: Coincident(g10,g1)
    c: Coincident(g10,g0)
    c: PointOnObject(g11,g-6)
    c: PointOnObject(g1,g11)
    c: DistanceY(g2,g1) = 19
    c: Coincident(g10,g-4)
    c: PointOnObject(g12,g4)
    c: PointOnObject(g12,g3)
    c: Tangent(g11,g-5) = -1.5708
    c: Tangent(g0,g-5) = -1.5708
    c: Tangent(g3,g0) = 1.5708
    c: PointOnObject(g13,g4)
    c: PointOnObject(g13,g3)
    c: Tangent(g4,g3,g13) = 1.5708
    c: Horizontal(g11,g0)
FEATURE [Part::Part2DObjectPython] Clone2D  label="Sketch108 (2D)"  # Draft 2D object (typed FeaturePython)
  Fuse = false
  Objects = -> [Sketch108]
  Placement = pos=(0,2,4e-16) rot=(0,0.707107,0.707107;3.14159rad)
  Scale = (1,1,1)
FEATURE [Sketcher::SketchObject] Sketch109
  ArcFitTolerance = 1e-06
  AttachmentOffset = pos=(0,0,-3.5) rot=(0,0,1;0rad)
  AttachmentSupport = -> [Pad008]
  ExternalGeometry = -> [Binder]
  FullyConstrained = true
  MakeInternals = false
  MapMode = 5
  Placement = pos=(0,0.1,8e-16) rot=(0,0.707107,0.707107;3.14159rad)
  sketch-geometry (1):
    g0: GeomPoint X=197.47 Y=8.55923 Z=0
  constraints (1):
    c: Symmetric(g-7,g-5,g0)
FEATURE [PartDesign::Chamfer] Chamfer005
  Angle = 45
  Base = -> Pad009 [Edge215,Edge212]
  BaseFeature = -> Pad009
  ChamferType = 1
  FlipDirection = false
  Refine = true
  Size = 1.5
  Size2 = 2.8
  SupportTransform = false
  Suppressed = false
  UseAllEdges = false
FEATURE [Sketcher::SketchObject] Sketch111
  ArcFitTolerance = 1e-06
  AttachmentSupport = -> [Pad009]
  ExternalGeometry = -> [Pad009]
  FullyConstrained = true
  MakeInternals = false
  MapMode = 5
  Placement = pos=(0,3.6,-8e-16) rot=(0,0.707107,0.707107;3.14159rad)
  sketch-geometry (21):
    g0: LineSegment [constr] StartX=97 StartY=36.8 StartZ=0 EndX=97 EndY=26.8 EndZ=0
    g1: LineSegment StartX=97 StartY=28.6 StartZ=0 EndX=97 EndY=27.8 EndZ=0
    g2: LineSegment StartX=97 StartY=27.8 StartZ=0 EndX=108 EndY=27.8 EndZ=0
    g3: LineSegment StartX=108 StartY=27.8 StartZ=0 EndX=108 EndY=28.6 EndZ=0
    g4: LineSegment StartX=108 StartY=28.6 StartZ=0 EndX=97 EndY=28.6 EndZ=0
    g5: LineSegment StartX=97 StartY=35.8 StartZ=0 EndX=97 EndY=35 EndZ=0
    g6: LineSegment StartX=97 StartY=35 StartZ=0 EndX=108 EndY=35 EndZ=0
    g7: LineSegment StartX=108 StartY=35 StartZ=0 EndX=108 EndY=35.8 EndZ=0
    g8: LineSegment StartX=108 StartY=35.8 StartZ=0 EndX=97 EndY=35.8 EndZ=0
    g9: LineSegment StartX=97 StartY=30.4 StartZ=0 EndX=97 EndY=29.6 EndZ=0
    g10: LineSegment StartX=97 StartY=29.6 StartZ=0 EndX=108 EndY=29.6 EndZ=0
    g11: LineSegment StartX=108 StartY=29.6 StartZ=0 EndX=108 EndY=30.4 EndZ=0
    g12: LineSegment StartX=108 StartY=30.4 StartZ=0 EndX=97 EndY=30.4 EndZ=0
    g13: LineSegment StartX=97 StartY=34 StartZ=0 EndX=97 EndY=33.2 EndZ=0
    g14: LineSegment StartX=97 StartY=33.2 StartZ=0 EndX=108 EndY=33.2 EndZ=0
    g15: LineSegment StartX=108 StartY=33.2 StartZ=0 EndX=108 EndY=34 EndZ=0
    g16: LineSegment StartX=108 StartY=34 StartZ=0 EndX=97 EndY=34 EndZ=0
    g17: LineSegment StartX=97 StartY=32.2 StartZ=0 EndX=97 EndY=31.4 EndZ=0
    g18: LineSegment StartX=97 StartY=31.4 StartZ=0 EndX=108 EndY=31.4 EndZ=0
    g19: LineSegment StartX=108 StartY=31.4 StartZ=0 EndX=108 EndY=32.2 EndZ=0
    g20: LineSegment StartX=108 StartY=32.2 StartZ=0 EndX=97 EndY=32.2 EndZ=0
  constraints (54):
    c: Vertical(g0)
    c: PointOnObject(g0,g-3)
    c: PointOnObject(g0,g-4)
    c: DistanceX(g0,g-5) = 11
    c: Coincident(g1,g2)
    c: Coincident(g2,g3)
    c: Coincident(g3,g4)
    c: Coincident(g4,g1)
    c: Horizontal(g2)
    c: Horizontal(g4)
    c: Tangent(g1,g0)
    c: Tangent(g3,g-5)
    c: DistanceY(g2,g3) = 0.8
    c: Coincident(g5,g6)
    c: Coincident(g6,g7)
    c: Coincident(g7,g8)
    c: Coincident(g8,g5)
    c: Horizontal(g6)
    c: Horizontal(g8)
    c: DistanceY(g6,g7) = 0.8
    c: Coincident(g9,g10)
    c: Coincident(g10,g11)
    c: Coincident(g11,g12)
    c: Coincident(g12,g9)
    c: Horizontal(g10)
    c: Horizontal(g12)
    c: DistanceY(g10,g11) = 0.8
    c: Tangent(g5,g0)
    c: Tangent(g7,g-5)
    c: Tangent(g9,g0)
    c: Tangent(g11,g-5)
    c: Coincident(g13,g14)
    c: Coincident(g14,g15)
    c: Coincident(g15,g16)
    c: Coincident(g16,g13)
    c: Horizontal(g14)
    c: Horizontal(g16)
    c: DistanceY(g14,g15) = 0.8
    c: Tangent(g13,g0)
    c: Tangent(g15,g-5)
    c: Coincident(g17,g18)
    c: Coincident(g18,g19)
    c: Coincident(g19,g20)
    c: Coincident(g20,g17)
    c: Horizontal(g18)
    c: Horizontal(g20)
    c: DistanceY(g18,g19) = 0.8
    c: Tangent(g17,g0)
    c: Tangent(g19,g-5)
    c: DistanceY(g1,g9) = 1
    c: DistanceY(g9,g17) = 1
    c: DistanceY(g17,g13) = 1
    c: DistanceY(g13,g5) = 1
    c: DistanceY(g0,g1) = 1
FEATURE [PartDesign::Pocket] Pocket004
  BaseFeature = -> Chamfer005
  Direction = (0,-1,2e-16)
  Length = 1
  Length2 = 5
  Profile = -> Sketch111
  ReferenceAxis = -> Sketch111 [N_Axis]
  Refine = true
  Suppressed = false
  Type = 0
FEATURE [PartDesign::Pad] Pad010
  BaseFeature = -> Pocket004
  Direction = (0,1,-2e-16)
  Length = 1.2
  Length2 = 10
  Profile = -> Sketch098
  ReferenceAxis = -> Sketch098 [N_Axis]
  Refine = true
  Suppressed = false
  Type = 0
FEATURE [PartDesign::Chamfer] Chamfer006
  Angle = 45
  Base = -> Pad010 [Edge291]
  BaseFeature = -> Pad010
  ChamferType = 1
  FlipDirection = false
  Refine = true
  Size = 1
  Size2 = 6
  SupportTransform = false
  Suppressed = false
  UseAllEdges = false
FEATURE [Sketcher::SketchObject] Sketch110
  ArcFitTolerance = 1e-06
  AttachmentSupport = -> [Pad010]
  ExternalGeometry = -> [Sketch098]
  FullyConstrained = true
  MakeInternals = false
  MapMode = 5
  Placement = pos=(0,4,-9e-16) rot=(0,0.707107,0.707107;3.14159rad)
  sketch-geometry (8):
    g0: LineSegment StartX=119.69 StartY=34 StartZ=0 EndX=130.69 EndY=34 EndZ=0
    g1: LineSegment StartX=119.95 StartY=33.2 StartZ=0 EndX=130.95 EndY=33.2 EndZ=0
    g2: LineSegment StartX=119.137 StartY=35.7 StartZ=0 EndX=130.137 EndY=35.7 EndZ=0
    g3: LineSegment StartX=118.877 StartY=36.5 StartZ=0 EndX=129.877 EndY=36.5 EndZ=0
    g4: LineSegment StartX=118.877 StartY=36.5 StartZ=0 EndX=119.137 EndY=35.7 EndZ=0
    g5: LineSegment StartX=129.877 StartY=36.5 StartZ=0 EndX=130.137 EndY=35.7 EndZ=0
    g6: LineSegment StartX=119.69 StartY=34 StartZ=0 EndX=119.95 EndY=33.2 EndZ=0
    g7: LineSegment StartX=130.69 StartY=34 StartZ=0 EndX=130.95 EndY=33.2 EndZ=0
  constraints (24):
    c: Horizontal(g0)
    c: Horizontal(g1)
    c: Horizontal(g2)
    c: Horizontal(g3)
    c: Equal(g1,g-5)
    c: Equal(g0,g-5)
    c: Equal(g2,g-5)
    c: Equal(g3,g-5)
    c: PointOnObject(g0,g-3)
    c: PointOnObject(g1,g-3)
    c: PointOnObject(g2,g-3)
    c: PointOnObject(g3,g-3)
    c: Coincident(g4,g3)
    c: Coincident(g4,g2)
    c: Coincident(g5,g3)
    c: Coincident(g5,g2)
    c: Coincident(g6,g0)
    c: Coincident(g6,g1)
    c: Coincident(g7,g0)
    c: Coincident(g7,g1)
    c: DistanceY(g1,g0) = 0.8
    c: DistanceY(g2,g3) = 0.8
    c: DistanceY(g-5,g1) = 2
    c: DistanceY(g-5,g2) = 4.5
FEATURE [PartDesign::Pocket] Pocket003
  BaseFeature = -> Chamfer006
  Direction = (0,-1,2e-16)
  Length = 1
  Length2 = 5
  Profile = -> Sketch110
  ReferenceAxis = -> Sketch110 [N_Axis]
  Refine = true
  Suppressed = false
  Type = 0
FEATURE [PartDesign::SubtractivePipe] SubtractivePipe
  AuxilleryCurvelinear = true
  AuxillerySpineTangent = false
  BaseFeature = -> Pocket003
  Binormal = (0,0,0)
  Mode = 0
  Profile = -> Sketch106
  Refine = true
  Spine = -> Pad008 [Edge215]
  SpineTangent = false
  Suppressed = false
  Transformation = 0
  Transition = 0
FEATURE [PartDesign::SubtractivePipe] SubtractivePipe001
  AuxilleryCurvelinear = true
  AuxillerySpineTangent = false
  BaseFeature = -> SubtractivePipe
  Binormal = (0,0,0)
  Mode = 0
  Profile = -> Sketch107
  Refine = true
  Spine = -> Pad008 [Edge213,Edge216,Edge210]
  SpineTangent = false
  Suppressed = false
  Transformation = 0
  Transition = 0
FEATURE [PartDesign::SubtractiveLoft] SubtractiveLoft
  BaseFeature = -> SubtractivePipe001
  Closed = false
  Profile = -> Sketch099
  Refine = true
  Ruled = false
  Sections = -> [Sketch108]
  Suppressed = false
FEATURE [PartDesign::SubtractiveLoft] SubtractiveLoft001
  BaseFeature = -> SubtractiveLoft
  Closed = false
  Profile = -> Clone2D
  Refine = true
  Ruled = false
  Sections = -> [Sketch109]
  Suppressed = false
FEATURE [Sketcher::SketchObject] Sketch112
  ArcFitTolerance = 1e-06
  AttachmentSupport = -> [Pad008]
  ExternalGeometry = -> [Binder]
  FullyConstrained = true
  MakeInternals = false
  MapMode = 5
  Placement = pos=(0,3.6,0) rot=(0,0.707107,0.707107;3.14159rad)
  sketch-geometry (4):
    g0: LineSegment [constr] StartX=167.782 StartY=-53.0314 StartZ=0 EndX=215.42 EndY=-53.0314 EndZ=0
    g1: GeomPoint [constr] X=191.282 Y=-53.0314 Z=0
    g2: Circle CenterX=191.282 CenterY=-53.0314 CenterZ=0 NormalX=0 NormalY=0 NormalZ=1 AngleXU=0 Radius=11.5
    g3: Circle CenterX=191.282 CenterY=-53.0314 CenterZ=0 NormalX=0 NormalY=0 NormalZ=1 AngleXU=0 Radius=10.7
  constraints (9):
    c: Horizontal(g0)
    c: PointOnObject(g0,g-3)
    c: Diameter(g2) = 23
    c: Coincident(g2,g1)
    c: Diameter(g3) = 21.4
    c: Coincident(g3,g1)
    c: DistanceX(g0,g1) = 23.5
    c: PointOnObject(g1,g0)
    c: Coincident(g0,g-4)
FEATURE [PartDesign::Chamfer] Chamfer016
  Angle = 45
  Base = -> SubtractiveLoft001 [Edge118,Edge117,Edge119,Edge120,Edge109]
  BaseFeature = -> SubtractiveLoft001
  ChamferType = 0
  FlipDirection = false
  Refine = true
  Size = 1.5
  Size2 = 1
  SupportTransform = false
  Suppressed = false
  UseAllEdges = false
FEATURE [PartDesign::Chamfer] Chamfer017
  Angle = 45
  Base = -> Chamfer016 [Edge15]
  BaseFeature = -> Chamfer016
  ChamferType = 0
  FlipDirection = false
  Refine = true
  Size = 3.5
  Size2 = 1
  SupportTransform = false
  Suppressed = false
  UseAllEdges = false
FEATURE [PartDesign::Chamfer] Chamfer018
  Angle = 45
  Base = -> Chamfer017 [Edge10]
  BaseFeature = -> Chamfer017
  ChamferType = 0
  FlipDirection = false
  Refine = true
  Size = 3.5
  Size2 = 1
  SupportTransform = false
  Suppressed = false
  UseAllEdges = false
FEATURE [PartDesign::Chamfer] Chamfer019
  Angle = 45
  Base = -> Chamfer018 [Edge93,Edge140]
  BaseFeature = -> Chamfer018
  ChamferType = 0
  FlipDirection = false
  Refine = true
  Size = 1.9
  Size2 = 1
  SupportTransform = false
  Suppressed = false
  UseAllEdges = false
FEATURE [PartDesign::Fillet] Fillet009
  Base = -> Chamfer019 [Edge84]
  BaseFeature = -> Chamfer019
  Radius = 1.1
  Refine = true
  SupportTransform = false
  Suppressed = false
  UseAllEdges = false
FEATURE [PartDesign::Fillet] Fillet010
  Base = -> Fillet009 [Edge78]
  BaseFeature = -> Fillet009
  Radius = 1.9
  Refine = true
  SupportTransform = false
  Suppressed = false
  UseAllEdges = false
FEATURE [PartDesign::Pocket] Pocket005
  BaseFeature = -> Fillet010
  Direction = (0,-1,2e-16)
  Length = 0.8
  Length2 = 5
  Profile = -> Sketch112
  ReferenceAxis = -> Sketch112 [N_Axis]
  Refine = true
  Suppressed = false
  Type = 0
FEATURE [Part::Mirroring] Part__Mirroring  label="Pocket005 (Mirror #1)"
  Base = (0,0,0)
  Normal = (0,0,1)
  Source = -> Pocket005
FEATURE [Part::Part2DObjectPython] ShapeString001  # Draft 2D object (typed FeaturePython)
  FontFile = <path>
  Fuse = false
  Justification = 6
  JustificationReference = 0
  KeepLeftMargin = false
  MakeFace = true
  ObliqueAngle = 0
  Placement = pos=(-183.5,3.6,-57.5) rot=(0,0.707107,0.707107;3.14159rad)
  ScaleToSize = true
  Size = 10
  String = AS
  Tracking = 0
FEATURE [PartDesign::Pocket] Pocket013
  BaseFeature = -> Pocket005
  Direction = (-1e-16,-1,2e-16)
  Length = 1
  Length2 = 5
  Profile = -> ShapeString001
  ReferenceAxis = -> ShapeString001 [N_Axis]
  Refine = true
  Suppressed = false
  Type = 0
FEATURE [PartDesign::Body] Body006  label="lato SX"
  AllowCompound = false
  Group = -> [Binder,Pad019,Chamfer015,Pocket002,Sketch133,Sketch091,Pad005,Sketch092,Pocket001,Sketch093,Sketch094,Pad006,Sketch095,Pad007,Sketch096,Pad008,Sketch097,Pad009,Chamfer005,Pocket004,Sketch098,Pad010,Chamfer006,Pocket003,SubtractivePipe,SubtractivePipe001,Sketch099,Sketch106,Sketch107,Sketch108,Clone2D,Sketch109,SubtractiveLoft,SubtractiveLoft001,Sketch110,Sketch111,Sketch112,Chamfer016,Chamfer017,+7 more]
  Origin = -> Origin006
  Tip = -> Pocket013
note: 2 file-system paths scrubbed to <path> (originals preserved in the JSON sidecar)
